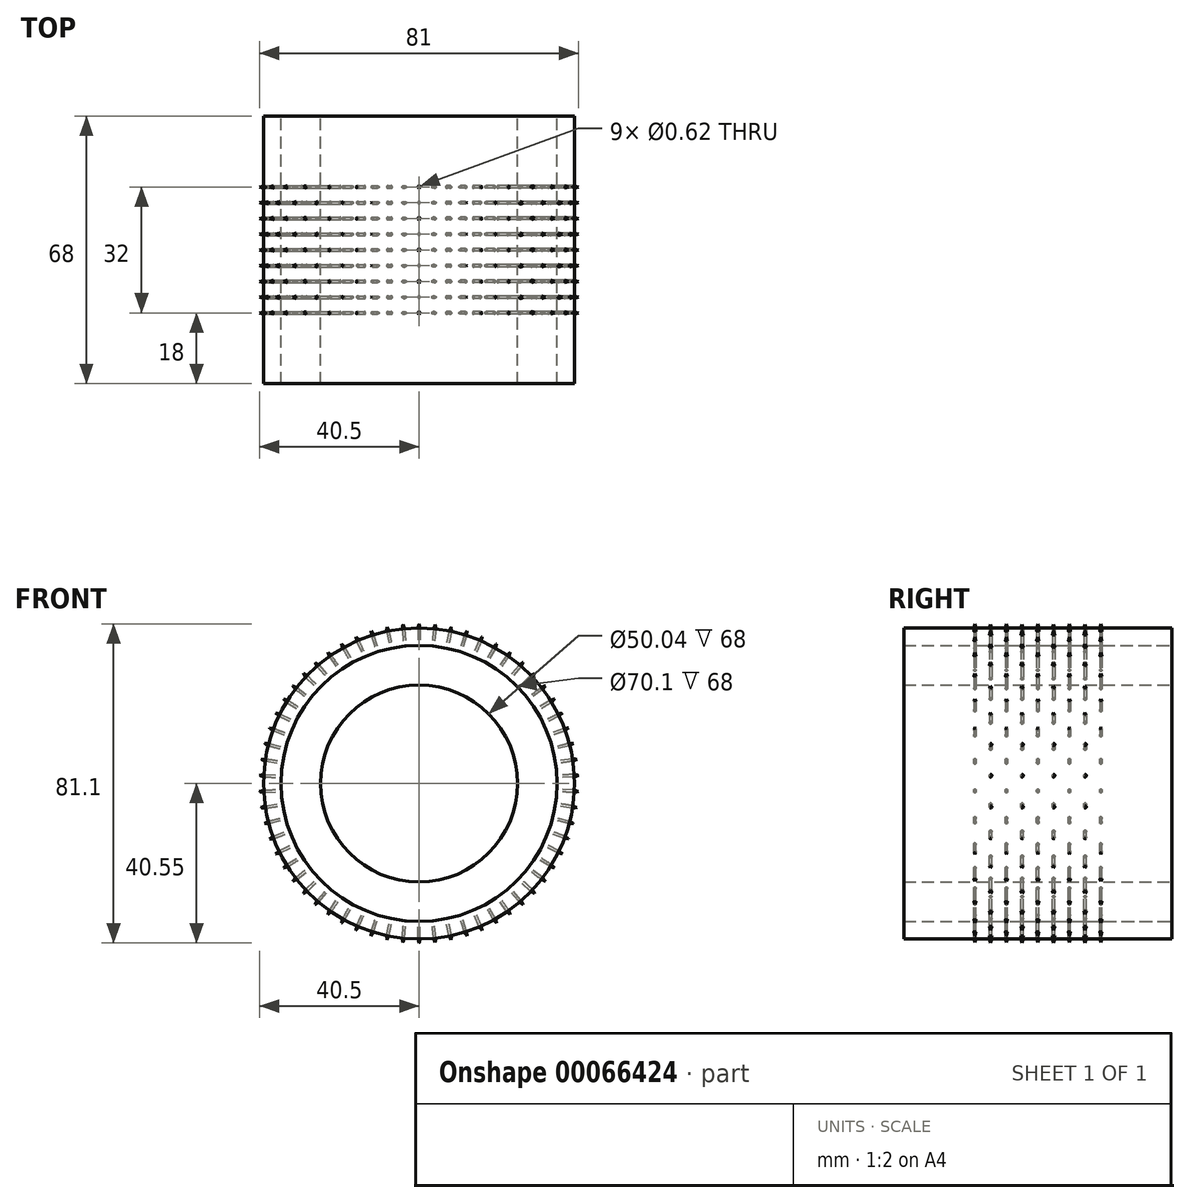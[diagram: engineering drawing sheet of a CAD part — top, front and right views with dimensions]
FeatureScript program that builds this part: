
annotation { "Feature Type Name" : "Feature", "Feature Type Description" : "" }
export const myFeature = defineFeature(function(context is Context, id is Id, definition is map)
    precondition{}
    {
        {
            var Q0;
            Q0=qCreatedBy(makeId("Front.planeOp"),FACE);
            var sketch = newSketch(context, id + "F0", { "sketchPlane" : qUnion([Q0])});
            skCircle(sketch, "E0", {"center": v(0, 0) * mm, "radius": 25.02 * mm});
            skCircle(sketch, "E1", {"center": v(0, 0) * mm, "radius": 35.05 * mm});
            skSolve(sketch);
        }
        {
            var Q0;
            Q0=makeQuery(id+"F0.imprint","IMPRINT",FACE,{"disambiguationData":[TD([[makeQuery(id+"F0.imprint","IMPRINT",EDGE,{"derivedFrom":sQuery(id+"F0.wireOp",EDGE,"E0")}),-1.0]])]});
            extrude(context, id + "F1", {"entities" : qUnion([Q0]), "endBound" : BoundingType.SYMMETRIC, "depth" : 68 * mm});
        }
        {
            var Q0;
            Q0=qCreatedBy(makeId("Front.planeOp"),FACE);
            var sketch = newSketch(context, id + "F2", { "sketchPlane" : qUnion([Q0])});
            skCircle(sketch, "E2.0", {"center": v(0, 0) * mm, "radius": 35.05 * mm});
            skCircle(sketch, "E3", {"center": v(0, 0) * mm, "radius": 39.5 * mm});
            skSolve(sketch);
        }
        {
            var Q0;
            Q0=makeQuery(id+"F2.imprint","IMPRINT",FACE,{"disambiguationData":[TD([[makeQuery(id+"F2.imprint","IMPRINT",EDGE,{"derivedFrom":sQuery(id+"F2.wireOp",EDGE,"E2.0")}),-1.0]])]});
            extrude(context, id + "F3", {"entities" : qUnion([Q0]), "endBound" : BoundingType.SYMMETRIC, "depth" : 68 * mm});
        }
        {
            var Q0;
            Q0=qCreatedBy(makeId("Top.planeOp"),FACE);
            cPlane(context, id + "F4", {"entities" : qUnion([Q0]), "cplaneType" : CPlaneType.OFFSET, "offset" : 70.1 / 2 * mm, "width" : 152.4 * mm, "height" : 152.4 * mm});
        }
        {
            var Q0;
            Q0=qCreatedBy(id+"F4.planeOp",FACE);
            var sketch = newSketch(context, id + "F5", { "sketchPlane" : qUnion([Q0])});
            skCircle(sketch, "E4", {"center": v(0, 0) * mm, "radius": 0.31 * mm});
            skCircle(sketch, "E5.0.1.0", {"center": v(0, 8) * mm, "radius": 0.31 * mm});
            skCircle(sketch, "E5.0.2.0", {"center": v(0, 16) * mm, "radius": 0.31 * mm});
            skCircle(sketch, "E5.0.3.0", {"center": v(0, 24) * mm, "radius": 0.31 * mm});
            skCircle(sketch, "E5.0.4.0", {"center": v(0, 32) * mm, "radius": 0.31 * mm});
            skLineSegment(sketch, "E5.direction1", {"start": v(0, 0) * mm, "end": v(25.4, 0) * mm, "construction": true});
            skLineSegment(sketch, "E5.direction2", {"start": v(0, 0) * mm, "end": v(0, 8) * mm, "construction": true});
            skCircle(sketch, "E6.0.1.0", {"center": v(0, -8) * mm, "radius": 0.31 * mm});
            skCircle(sketch, "E6.0.2.0", {"center": v(0, -16) * mm, "radius": 0.31 * mm});
            skCircle(sketch, "E6.0.3.0", {"center": v(0, -24) * mm, "radius": 0.31 * mm});
            skCircle(sketch, "E6.0.4.0", {"center": v(0, -32) * mm, "radius": 0.31 * mm});
            skLineSegment(sketch, "E6.direction2", {"start": v(0, 0) * mm, "end": v(0, -8) * mm, "construction": true});
            skSolve(sketch);
        }
        {
            var Q0;
            Q0=makeQuery(id+"F5.imprint","IMPRINT",FACE,{"disambiguationData":[TD([[makeQuery(id+"F5.imprint","IMPRINT",EDGE,{"derivedFrom":sQuery(id+"F5.wireOp",EDGE,"E6.0.2.0")}),1.0]])]});
            var Q1;
            Q1=makeQuery(id+"F5.imprint","IMPRINT",FACE,{"disambiguationData":[TD([[makeQuery(id+"F5.imprint","IMPRINT",EDGE,{"derivedFrom":sQuery(id+"F5.wireOp",EDGE,"E6.0.1.0")}),1.0]])]});
            var Q2;
            Q2=makeQuery(id+"F5.imprint","IMPRINT",FACE,{"disambiguationData":[TD([[makeQuery(id+"F5.imprint","IMPRINT",EDGE,{"derivedFrom":sQuery(id+"F5.wireOp",EDGE,"E4")}),1.0]])]});
            var Q3;
            Q3=makeQuery(id+"F5.imprint","IMPRINT",FACE,{"disambiguationData":[TD([[makeQuery(id+"F5.imprint","IMPRINT",EDGE,{"derivedFrom":sQuery(id+"F5.wireOp",EDGE,"E5.0.2.0")}),1.0]])]});
            var Q4;
            Q4=makeQuery(id+"F5.imprint","IMPRINT",FACE,{"disambiguationData":[TD([[makeQuery(id+"F5.imprint","IMPRINT",EDGE,{"derivedFrom":sQuery(id+"F5.wireOp",EDGE,"E5.0.1.0")}),1.0]])]});
            extrude(context, id + "F6", {"entities" : qUnion([Q0, Q1, Q2, Q3, Q4]), "operationType" : NewBodyOperationType.REMOVE, "depth" : 25.4 * mm});
        }
        {
            var Q0;
            Q0=qCreatedBy(makeId("Top.planeOp"),FACE);
            var sketch = newSketch(context, id + "F7", { "sketchPlane" : qUnion([Q0])});
            skLineSegment(sketch, "E7", {"start": v(0, 66.25) * mm, "end": v(0, -72.1) * mm, "construction": true});
            skSolve(sketch);
        }
        {
            var Q0;
            Q0=makeQuery(id+"F5.imprint","IMPRINT",FACE,{"disambiguationData":[TD([[makeQuery(id+"F5.imprint","IMPRINT",EDGE,{"derivedFrom":sQuery(id+"F5.wireOp",EDGE,"E5.0.2.0")}),1.0]])]});
            var Q1;
            Q1=makeQuery(id+"F5.imprint","IMPRINT",FACE,{"disambiguationData":[TD([[makeQuery(id+"F5.imprint","IMPRINT",EDGE,{"derivedFrom":sQuery(id+"F5.wireOp",EDGE,"E5.0.1.0")}),1.0]])]});
            var Q2;
            Q2=makeQuery(id+"F5.imprint","IMPRINT",FACE,{"disambiguationData":[TD([[makeQuery(id+"F5.imprint","IMPRINT",EDGE,{"derivedFrom":sQuery(id+"F5.wireOp",EDGE,"E6.0.1.0")}),1.0]])]});
            var Q3;
            Q3=makeQuery(id+"F5.imprint","IMPRINT",FACE,{"disambiguationData":[TD([[makeQuery(id+"F5.imprint","IMPRINT",EDGE,{"derivedFrom":sQuery(id+"F5.wireOp",EDGE,"E6.0.2.0")}),1.0]])]});
            var Q4;
            Q4=makeQuery(id+"F5.imprint","IMPRINT",FACE,{"disambiguationData":[TD([[makeQuery(id+"F5.imprint","IMPRINT",EDGE,{"derivedFrom":sQuery(id+"F5.wireOp",EDGE,"E4")}),1.0]])]});
            extrude(context, id + "F8", {"entities" : qUnion([Q0, Q1, Q2, Q3, Q4]), "depth" : 5.5 * mm});
        }
        {
            var Q0;
            Q0=makeQuery(id+"F8.opExtrude","CAP_EDGE",EDGE,{"disambiguationData":[OSD([sQuery(id+"F5.wireOp",EDGE,"E6.0.4.0")])],"isStart":false});
            var Q1;
            Q1=makeQuery(id+"F8.opExtrude","CAP_EDGE",EDGE,{"disambiguationData":[OSD([sQuery(id+"F5.wireOp",EDGE,"E6.0.3.0")])],"isStart":false});
            var Q2;
            Q2=makeQuery(id+"F8.opExtrude","CAP_EDGE",EDGE,{"disambiguationData":[OSD([sQuery(id+"F5.wireOp",EDGE,"E6.0.2.0")])],"isStart":false});
            var Q3;
            Q3=makeQuery(id+"F8.opExtrude","CAP_EDGE",EDGE,{"disambiguationData":[OSD([sQuery(id+"F5.wireOp",EDGE,"E6.0.1.0")])],"isStart":false});
            var Q4;
            Q4=makeQuery(id+"F8.opExtrude","CAP_EDGE",EDGE,{"disambiguationData":[OSD([sQuery(id+"F5.wireOp",EDGE,"E4")])],"isStart":false});
            var Q5;
            Q5=makeQuery(id+"F8.opExtrude","CAP_EDGE",EDGE,{"disambiguationData":[OSD([sQuery(id+"F5.wireOp",EDGE,"E5.0.1.0")])],"isStart":false});
            var Q6;
            Q6=makeQuery(id+"F8.opExtrude","CAP_EDGE",EDGE,{"disambiguationData":[OSD([sQuery(id+"F5.wireOp",EDGE,"E5.0.2.0")])],"isStart":false});
            var Q7;
            Q7=makeQuery(id+"F8.opExtrude","CAP_EDGE",EDGE,{"disambiguationData":[OSD([sQuery(id+"F5.wireOp",EDGE,"E5.0.3.0")])],"isStart":false});
            var Q8;
            Q8=makeQuery(id+"F8.opExtrude","CAP_EDGE",EDGE,{"disambiguationData":[OSD([sQuery(id+"F5.wireOp",EDGE,"E5.0.4.0")])],"isStart":false});
            chamfer(context, id + "F9", {"entities" : qUnion([Q0, Q1, Q2, Q3, Q4, Q5, Q6, Q7, Q8]), "chamferType" : ChamferType.TWO_OFFSETS, "width1" : 0.31 * mm, "oppositeDirection" : false, "width2" : 1.1 * mm});
        }
        {
            var Q0;
            Q0=qCreatedBy(makeId("Top.planeOp"),FACE);
            cPlane(context, id + "F10", {"entities" : qUnion([Q0]), "cplaneType" : CPlaneType.OFFSET, "offset" : 70.1 * mm / 2, "oppositeDirection" : true, "width" : 152.4 * mm, "height" : 152.4 * mm});
        }
        {
            var Q0;
            Q0=qCreatedBy(id+"F10.planeOp",FACE);
            var sketch = newSketch(context, id + "F11", { "sketchPlane" : qUnion([Q0])});
            skCircle(sketch, "E8", {"center": v(0, -4) * mm, "radius": 0.31 * mm});
            skCircle(sketch, "E9", {"center": v(0, 4) * mm, "radius": 0.31 * mm});
            skCircle(sketch, "E10.0.1.0", {"center": v(0, -12) * mm, "radius": 0.31 * mm});
            skCircle(sketch, "E10.0.2.0", {"center": v(0, -20) * mm, "radius": 0.31 * mm});
            skCircle(sketch, "E10.0.3.0", {"center": v(0, -28) * mm, "radius": 0.31 * mm});
            skLineSegment(sketch, "E10.direction1", {"start": v(0, -4) * mm, "end": v(20.95, -4) * mm, "construction": true});
            skLineSegment(sketch, "E10.direction2", {"start": v(0, -4) * mm, "end": v(0, -12) * mm, "construction": true});
            skCircle(sketch, "E11.0.1.0", {"center": v(0, 12) * mm, "radius": 0.31 * mm});
            skCircle(sketch, "E11.0.2.0", {"center": v(0, 20) * mm, "radius": 0.31 * mm});
            skCircle(sketch, "E11.0.3.0", {"center": v(0, 28) * mm, "radius": 0.31 * mm});
            skLineSegment(sketch, "E11.direction1", {"start": v(0, 4) * mm, "end": v(25.4, 4) * mm, "construction": true});
            skLineSegment(sketch, "E11.direction2", {"start": v(0, 4) * mm, "end": v(0, 12) * mm, "construction": true});
            skSolve(sketch);
        }
        {
            var Q0;
            Q0=makeQuery(id+"F11.imprint","IMPRINT",FACE,{"disambiguationData":[TD([[makeQuery(id+"F11.imprint","IMPRINT",EDGE,{"derivedFrom":sQuery(id+"F11.wireOp",EDGE,"E8")}),1.0]])]});
            var Q1;
            Q1=makeQuery(id+"F11.imprint","IMPRINT",FACE,{"disambiguationData":[TD([[makeQuery(id+"F11.imprint","IMPRINT",EDGE,{"derivedFrom":sQuery(id+"F11.wireOp",EDGE,"E10.0.1.0")}),1.0]])]});
            var Q2;
            Q2=makeQuery(id+"F11.imprint","IMPRINT",FACE,{"disambiguationData":[TD([[makeQuery(id+"F11.imprint","IMPRINT",EDGE,{"derivedFrom":sQuery(id+"F11.wireOp",EDGE,"E11.0.1.0")}),1.0]])]});
            var Q3;
            Q3=makeQuery(id+"F11.imprint","IMPRINT",FACE,{"disambiguationData":[TD([[makeQuery(id+"F11.imprint","IMPRINT",EDGE,{"derivedFrom":sQuery(id+"F11.wireOp",EDGE,"E9")}),1.0]])]});
            extrude(context, id + "F12", {"entities" : qUnion([Q0, Q1, Q2, Q3]), "operationType" : NewBodyOperationType.REMOVE, "oppositeDirection" : true, "depth" : 25.4 * mm});
        }
        {
            var Q0;
            Q0=makeQuery(id+"F11.imprint","IMPRINT",FACE,{"disambiguationData":[TD([[makeQuery(id+"F11.imprint","IMPRINT",EDGE,{"derivedFrom":sQuery(id+"F11.wireOp",EDGE,"E10.0.1.0")}),1.0]])]});
            var Q1;
            Q1=makeQuery(id+"F11.imprint","IMPRINT",FACE,{"disambiguationData":[TD([[makeQuery(id+"F11.imprint","IMPRINT",EDGE,{"derivedFrom":sQuery(id+"F11.wireOp",EDGE,"E8")}),1.0]])]});
            var Q2;
            Q2=makeQuery(id+"F11.imprint","IMPRINT",FACE,{"disambiguationData":[TD([[makeQuery(id+"F11.imprint","IMPRINT",EDGE,{"derivedFrom":sQuery(id+"F11.wireOp",EDGE,"E9")}),1.0]])]});
            var Q3;
            Q3=makeQuery(id+"F11.imprint","IMPRINT",FACE,{"disambiguationData":[TD([[makeQuery(id+"F11.imprint","IMPRINT",EDGE,{"derivedFrom":sQuery(id+"F11.wireOp",EDGE,"E11.0.1.0")}),1.0]])]});
            extrude(context, id + "F13", {"entities" : qUnion([Q0, Q1, Q2, Q3]), "oppositeDirection" : true, "depth" : 5.5 * mm});
        }
        {
            var Q0;
            Q0=makeQuery(id+"F13.opExtrude","CAP_EDGE",EDGE,{"disambiguationData":[OSD([sQuery(id+"F11.wireOp",EDGE,"E10.0.3.0")])],"isStart":false});
            var Q1;
            Q1=makeQuery(id+"F13.opExtrude","CAP_EDGE",EDGE,{"disambiguationData":[OSD([sQuery(id+"F11.wireOp",EDGE,"E10.0.2.0")])],"isStart":false});
            var Q2;
            Q2=makeQuery(id+"F13.opExtrude","CAP_EDGE",EDGE,{"disambiguationData":[OSD([sQuery(id+"F11.wireOp",EDGE,"E10.0.1.0")])],"isStart":false});
            var Q3;
            Q3=makeQuery(id+"F13.opExtrude","CAP_EDGE",EDGE,{"disambiguationData":[OSD([sQuery(id+"F11.wireOp",EDGE,"E8")])],"isStart":false});
            var Q4;
            Q4=makeQuery(id+"F13.opExtrude","CAP_EDGE",EDGE,{"disambiguationData":[OSD([sQuery(id+"F11.wireOp",EDGE,"E9")])],"isStart":false});
            var Q5;
            Q5=makeQuery(id+"F13.opExtrude","CAP_EDGE",EDGE,{"disambiguationData":[OSD([sQuery(id+"F11.wireOp",EDGE,"E11.0.1.0")])],"isStart":false});
            var Q6;
            Q6=makeQuery(id+"F13.opExtrude","CAP_EDGE",EDGE,{"disambiguationData":[OSD([sQuery(id+"F11.wireOp",EDGE,"E11.0.2.0")])],"isStart":false});
            var Q7;
            Q7=makeQuery(id+"F13.opExtrude","CAP_EDGE",EDGE,{"disambiguationData":[OSD([sQuery(id+"F11.wireOp",EDGE,"E11.0.3.0")])],"isStart":false});
            chamfer(context, id + "F14", {"entities" : qUnion([Q0, Q1, Q2, Q3, Q4, Q5, Q6, Q7]), "chamferType" : ChamferType.TWO_OFFSETS, "width1" : 1.1 * mm, "oppositeDirection" : false, "width2" : 0.31 * mm, "tangentPropagation" : true});
        }
        {
            var Q0;
            Q0=makeQuery(id+"F8.opExtrude","SWEPT_BODY",BODY,{"disambiguationData":[OSD([sQuery(id+"F5.wireOp",EDGE,"E4")])]});
            var Q1;
            Q1=makeQuery(id+"F8.opExtrude","SWEPT_BODY",BODY,{"disambiguationData":[OSD([sQuery(id+"F5.wireOp",EDGE,"E5.0.1.0")])]});
            var Q2;
            Q2=makeQuery(id+"F8.opExtrude","SWEPT_BODY",BODY,{"disambiguationData":[OSD([sQuery(id+"F5.wireOp",EDGE,"E5.0.2.0")])]});
            var Q3;
            Q3=makeQuery(id+"F8.opExtrude","SWEPT_BODY",BODY,{"disambiguationData":[OSD([sQuery(id+"F5.wireOp",EDGE,"E5.0.3.0")])]});
            var Q4;
            Q4=makeQuery(id+"F8.opExtrude","SWEPT_BODY",BODY,{"disambiguationData":[OSD([sQuery(id+"F5.wireOp",EDGE,"E5.0.4.0")])]});
            var Q5;
            Q5=makeQuery(id+"F8.opExtrude","SWEPT_BODY",BODY,{"disambiguationData":[OSD([sQuery(id+"F5.wireOp",EDGE,"E6.0.1.0")])]});
            var Q6;
            Q6=makeQuery(id+"F8.opExtrude","SWEPT_BODY",BODY,{"disambiguationData":[OSD([sQuery(id+"F5.wireOp",EDGE,"E6.0.2.0")])]});
            var Q7;
            Q7=makeQuery(id+"F8.opExtrude","SWEPT_BODY",BODY,{"disambiguationData":[OSD([sQuery(id+"F5.wireOp",EDGE,"E6.0.3.0")])]});
            var Q8;
            Q8=makeQuery(id+"F8.opExtrude","SWEPT_BODY",BODY,{"disambiguationData":[OSD([sQuery(id+"F5.wireOp",EDGE,"E6.0.4.0")])]});
            var Q9;
            Q9=makeQuery(id+"F13.opExtrude","SWEPT_BODY",BODY,{"disambiguationData":[OSD([sQuery(id+"F11.wireOp",EDGE,"E8")])]});
            var Q10;
            Q10=makeQuery(id+"F13.opExtrude","SWEPT_BODY",BODY,{"disambiguationData":[OSD([sQuery(id+"F11.wireOp",EDGE,"E9")])]});
            var Q11;
            Q11=makeQuery(id+"F13.opExtrude","SWEPT_BODY",BODY,{"disambiguationData":[OSD([sQuery(id+"F11.wireOp",EDGE,"E10.0.1.0")])]});
            var Q12;
            Q12=makeQuery(id+"F13.opExtrude","SWEPT_BODY",BODY,{"disambiguationData":[OSD([sQuery(id+"F11.wireOp",EDGE,"E10.0.2.0")])]});
            var Q13;
            Q13=makeQuery(id+"F13.opExtrude","SWEPT_BODY",BODY,{"disambiguationData":[OSD([sQuery(id+"F11.wireOp",EDGE,"E10.0.3.0")])]});
            var Q14;
            Q14=makeQuery(id+"F13.opExtrude","SWEPT_BODY",BODY,{"disambiguationData":[OSD([sQuery(id+"F11.wireOp",EDGE,"E11.0.1.0")])]});
            var Q15;
            Q15=makeQuery(id+"F13.opExtrude","SWEPT_BODY",BODY,{"disambiguationData":[OSD([sQuery(id+"F11.wireOp",EDGE,"E11.0.2.0")])]});
            var Q16;
            Q16=makeQuery(id+"F13.opExtrude","SWEPT_BODY",BODY,{"disambiguationData":[OSD([sQuery(id+"F11.wireOp",EDGE,"E11.0.3.0")])]});
            var Q17;
            Q17=sQuery(id+"F7.wireOp",EDGE,"E7");
            circularPattern(context, id + "F15", {"entities" : qUnion([Q0, Q1, Q2, Q3, Q4, Q5, Q6, Q7, Q8, Q9, Q10, Q11, Q12, Q13, Q14, Q15, Q16]), "axis" : qUnion([Q17]), "angle" : 11.6 * degree, "instanceCount" : round(31)});
        }
        {
            var Q0;
            Q0=makeQuery(id+"F15.opPattern","COPY",BODY,{"derivedFrom":makeQuery(id+"F13.opExtrude","SWEPT_BODY",BODY,{"disambiguationData":[OSD([sQuery(id+"F11.wireOp",EDGE,"E11.0.3.0")])]}),"instanceName":"2"});
            var Q1;
            Q1=makeQuery(id+"F15.opPattern","COPY",BODY,{"derivedFrom":makeQuery(id+"F8.opExtrude","SWEPT_BODY",BODY,{"disambiguationData":[OSD([sQuery(id+"F5.wireOp",EDGE,"E4")])]}),"instanceName":"3"});
            var Q2;
            Q2=makeQuery(id+"F15.opPattern","COPY",BODY,{"derivedFrom":makeQuery(id+"F8.opExtrude","SWEPT_BODY",BODY,{"disambiguationData":[OSD([sQuery(id+"F5.wireOp",EDGE,"E5.0.2.0")])]}),"instanceName":"3"});
            var Q3;
            Q3=makeQuery(id+"F15.opPattern","COPY",BODY,{"derivedFrom":makeQuery(id+"F8.opExtrude","SWEPT_BODY",BODY,{"disambiguationData":[OSD([sQuery(id+"F5.wireOp",EDGE,"E5.0.4.0")])]}),"instanceName":"3"});
            var Q4;
            Q4=makeQuery(id+"F15.opPattern","COPY",BODY,{"derivedFrom":makeQuery(id+"F13.opExtrude","SWEPT_BODY",BODY,{"disambiguationData":[OSD([sQuery(id+"F11.wireOp",EDGE,"E11.0.2.0")])]}),"instanceName":"3"});
            var Q5;
            Q5=makeQuery(id+"F15.opPattern","COPY",BODY,{"derivedFrom":makeQuery(id+"F8.opExtrude","SWEPT_BODY",BODY,{"disambiguationData":[OSD([sQuery(id+"F5.wireOp",EDGE,"E4")])]}),"instanceName":"4"});
            var Q6;
            Q6=makeQuery(id+"F15.opPattern","COPY",BODY,{"derivedFrom":makeQuery(id+"F8.opExtrude","SWEPT_BODY",BODY,{"disambiguationData":[OSD([sQuery(id+"F5.wireOp",EDGE,"E5.0.1.0")])]}),"instanceName":"4"});
            var Q7;
            Q7=makeQuery(id+"F15.opPattern","COPY",BODY,{"derivedFrom":makeQuery(id+"F8.opExtrude","SWEPT_BODY",BODY,{"disambiguationData":[OSD([sQuery(id+"F5.wireOp",EDGE,"E5.0.2.0")])]}),"instanceName":"4"});
            var Q8;
            Q8=makeQuery(id+"F15.opPattern","COPY",BODY,{"derivedFrom":makeQuery(id+"F8.opExtrude","SWEPT_BODY",BODY,{"disambiguationData":[OSD([sQuery(id+"F5.wireOp",EDGE,"E6.0.1.0")])]}),"instanceName":"4"});
            var Q9;
            Q9=makeQuery(id+"F15.opPattern","COPY",BODY,{"derivedFrom":makeQuery(id+"F13.opExtrude","SWEPT_BODY",BODY,{"disambiguationData":[OSD([sQuery(id+"F11.wireOp",EDGE,"E9")])]}),"instanceName":"1"});
            var Q10;
            Q10=makeQuery(id+"F15.opPattern","COPY",BODY,{"derivedFrom":makeQuery(id+"F13.opExtrude","SWEPT_BODY",BODY,{"disambiguationData":[OSD([sQuery(id+"F11.wireOp",EDGE,"E10.0.1.0")])]}),"instanceName":"1"});
            var Q11;
            Q11=makeQuery(id+"F15.opPattern","COPY",BODY,{"derivedFrom":makeQuery(id+"F13.opExtrude","SWEPT_BODY",BODY,{"disambiguationData":[OSD([sQuery(id+"F11.wireOp",EDGE,"E10.0.2.0")])]}),"instanceName":"1"});
            var Q12;
            Q12=makeQuery(id+"F15.opPattern","COPY",BODY,{"derivedFrom":makeQuery(id+"F13.opExtrude","SWEPT_BODY",BODY,{"disambiguationData":[OSD([sQuery(id+"F11.wireOp",EDGE,"E10.0.3.0")])]}),"instanceName":"1"});
            var Q13;
            Q13=makeQuery(id+"F15.opPattern","COPY",BODY,{"derivedFrom":makeQuery(id+"F13.opExtrude","SWEPT_BODY",BODY,{"disambiguationData":[OSD([sQuery(id+"F11.wireOp",EDGE,"E11.0.1.0")])]}),"instanceName":"1"});
            var Q14;
            Q14=makeQuery(id+"F15.opPattern","COPY",BODY,{"derivedFrom":makeQuery(id+"F13.opExtrude","SWEPT_BODY",BODY,{"disambiguationData":[OSD([sQuery(id+"F11.wireOp",EDGE,"E11.0.2.0")])]}),"instanceName":"1"});
            var Q15;
            Q15=makeQuery(id+"F15.opPattern","COPY",BODY,{"derivedFrom":makeQuery(id+"F13.opExtrude","SWEPT_BODY",BODY,{"disambiguationData":[OSD([sQuery(id+"F11.wireOp",EDGE,"E11.0.3.0")])]}),"instanceName":"1"});
            var Q16;
            Q16=makeQuery(id+"F15.opPattern","COPY",BODY,{"derivedFrom":makeQuery(id+"F8.opExtrude","SWEPT_BODY",BODY,{"disambiguationData":[OSD([sQuery(id+"F5.wireOp",EDGE,"E4")])]}),"instanceName":"2"});
            var Q17;
            Q17=makeQuery(id+"F15.opPattern","COPY",BODY,{"derivedFrom":makeQuery(id+"F8.opExtrude","SWEPT_BODY",BODY,{"disambiguationData":[OSD([sQuery(id+"F5.wireOp",EDGE,"E5.0.1.0")])]}),"instanceName":"2"});
            var Q18;
            Q18=makeQuery(id+"F15.opPattern","COPY",BODY,{"derivedFrom":makeQuery(id+"F8.opExtrude","SWEPT_BODY",BODY,{"disambiguationData":[OSD([sQuery(id+"F5.wireOp",EDGE,"E5.0.2.0")])]}),"instanceName":"2"});
            var Q19;
            Q19=makeQuery(id+"F15.opPattern","COPY",BODY,{"derivedFrom":makeQuery(id+"F8.opExtrude","SWEPT_BODY",BODY,{"disambiguationData":[OSD([sQuery(id+"F5.wireOp",EDGE,"E5.0.3.0")])]}),"instanceName":"2"});
            var Q20;
            Q20=makeQuery(id+"F15.opPattern","COPY",BODY,{"derivedFrom":makeQuery(id+"F8.opExtrude","SWEPT_BODY",BODY,{"disambiguationData":[OSD([sQuery(id+"F5.wireOp",EDGE,"E5.0.3.0")])]}),"instanceName":"2"});
            var Q21;
            Q21=makeQuery(id+"F15.opPattern","COPY",BODY,{"derivedFrom":makeQuery(id+"F8.opExtrude","SWEPT_BODY",BODY,{"disambiguationData":[OSD([sQuery(id+"F5.wireOp",EDGE,"E5.0.4.0")])]}),"instanceName":"2"});
            var Q22;
            Q22=makeQuery(id+"F15.opPattern","COPY",BODY,{"derivedFrom":makeQuery(id+"F8.opExtrude","SWEPT_BODY",BODY,{"disambiguationData":[OSD([sQuery(id+"F5.wireOp",EDGE,"E6.0.1.0")])]}),"instanceName":"2"});
            var Q23;
            Q23=makeQuery(id+"F15.opPattern","COPY",BODY,{"derivedFrom":makeQuery(id+"F8.opExtrude","SWEPT_BODY",BODY,{"disambiguationData":[OSD([sQuery(id+"F5.wireOp",EDGE,"E6.0.2.0")])]}),"instanceName":"2"});
            var Q24;
            Q24=makeQuery(id+"F15.opPattern","COPY",BODY,{"derivedFrom":makeQuery(id+"F8.opExtrude","SWEPT_BODY",BODY,{"disambiguationData":[OSD([sQuery(id+"F5.wireOp",EDGE,"E6.0.3.0")])]}),"instanceName":"2"});
            var Q25;
            Q25=makeQuery(id+"F15.opPattern","COPY",BODY,{"derivedFrom":makeQuery(id+"F8.opExtrude","SWEPT_BODY",BODY,{"disambiguationData":[OSD([sQuery(id+"F5.wireOp",EDGE,"E6.0.4.0")])]}),"instanceName":"2"});
            var Q26;
            Q26=makeQuery(id+"F15.opPattern","COPY",BODY,{"derivedFrom":makeQuery(id+"F13.opExtrude","SWEPT_BODY",BODY,{"disambiguationData":[OSD([sQuery(id+"F11.wireOp",EDGE,"E8")])]}),"instanceName":"2"});
            var Q27;
            Q27=makeQuery(id+"F15.opPattern","COPY",BODY,{"derivedFrom":makeQuery(id+"F13.opExtrude","SWEPT_BODY",BODY,{"disambiguationData":[OSD([sQuery(id+"F11.wireOp",EDGE,"E9")])]}),"instanceName":"2"});
            var Q28;
            Q28=makeQuery(id+"F15.opPattern","COPY",BODY,{"derivedFrom":makeQuery(id+"F13.opExtrude","SWEPT_BODY",BODY,{"disambiguationData":[OSD([sQuery(id+"F11.wireOp",EDGE,"E10.0.1.0")])]}),"instanceName":"2"});
            var Q29;
            Q29=makeQuery(id+"F15.opPattern","COPY",BODY,{"derivedFrom":makeQuery(id+"F13.opExtrude","SWEPT_BODY",BODY,{"disambiguationData":[OSD([sQuery(id+"F11.wireOp",EDGE,"E10.0.2.0")])]}),"instanceName":"2"});
            var Q30;
            Q30=makeQuery(id+"F15.opPattern","COPY",BODY,{"derivedFrom":makeQuery(id+"F13.opExtrude","SWEPT_BODY",BODY,{"disambiguationData":[OSD([sQuery(id+"F11.wireOp",EDGE,"E10.0.3.0")])]}),"instanceName":"2"});
            var Q31;
            Q31=makeQuery(id+"F15.opPattern","COPY",BODY,{"derivedFrom":makeQuery(id+"F13.opExtrude","SWEPT_BODY",BODY,{"disambiguationData":[OSD([sQuery(id+"F11.wireOp",EDGE,"E11.0.1.0")])]}),"instanceName":"2"});
            var Q32;
            Q32=makeQuery(id+"F15.opPattern","COPY",BODY,{"derivedFrom":makeQuery(id+"F13.opExtrude","SWEPT_BODY",BODY,{"disambiguationData":[OSD([sQuery(id+"F11.wireOp",EDGE,"E11.0.2.0")])]}),"instanceName":"2"});
            var Q33;
            Q33=makeQuery(id+"F15.opPattern","COPY",BODY,{"derivedFrom":makeQuery(id+"F8.opExtrude","SWEPT_BODY",BODY,{"disambiguationData":[OSD([sQuery(id+"F5.wireOp",EDGE,"E5.0.1.0")])]}),"instanceName":"3"});
            var Q34;
            Q34=makeQuery(id+"F15.opPattern","COPY",BODY,{"derivedFrom":makeQuery(id+"F8.opExtrude","SWEPT_BODY",BODY,{"disambiguationData":[OSD([sQuery(id+"F5.wireOp",EDGE,"E5.0.3.0")])]}),"instanceName":"3"});
            var Q35;
            Q35=makeQuery(id+"F15.opPattern","COPY",BODY,{"derivedFrom":makeQuery(id+"F8.opExtrude","SWEPT_BODY",BODY,{"disambiguationData":[OSD([sQuery(id+"F5.wireOp",EDGE,"E6.0.1.0")])]}),"instanceName":"3"});
            var Q36;
            Q36=makeQuery(id+"F15.opPattern","COPY",BODY,{"derivedFrom":makeQuery(id+"F8.opExtrude","SWEPT_BODY",BODY,{"disambiguationData":[OSD([sQuery(id+"F5.wireOp",EDGE,"E6.0.2.0")])]}),"instanceName":"3"});
            var Q37;
            Q37=makeQuery(id+"F15.opPattern","COPY",BODY,{"derivedFrom":makeQuery(id+"F8.opExtrude","SWEPT_BODY",BODY,{"disambiguationData":[OSD([sQuery(id+"F5.wireOp",EDGE,"E6.0.3.0")])]}),"instanceName":"3"});
            var Q38;
            Q38=makeQuery(id+"F15.opPattern","COPY",BODY,{"derivedFrom":makeQuery(id+"F8.opExtrude","SWEPT_BODY",BODY,{"disambiguationData":[OSD([sQuery(id+"F5.wireOp",EDGE,"E6.0.4.0")])]}),"instanceName":"3"});
            var Q39;
            Q39=makeQuery(id+"F15.opPattern","COPY",BODY,{"derivedFrom":makeQuery(id+"F13.opExtrude","SWEPT_BODY",BODY,{"disambiguationData":[OSD([sQuery(id+"F11.wireOp",EDGE,"E8")])]}),"instanceName":"3"});
            var Q40;
            Q40=makeQuery(id+"F15.opPattern","COPY",BODY,{"derivedFrom":makeQuery(id+"F13.opExtrude","SWEPT_BODY",BODY,{"disambiguationData":[OSD([sQuery(id+"F11.wireOp",EDGE,"E9")])]}),"instanceName":"3"});
            var Q41;
            Q41=makeQuery(id+"F15.opPattern","COPY",BODY,{"derivedFrom":makeQuery(id+"F13.opExtrude","SWEPT_BODY",BODY,{"disambiguationData":[OSD([sQuery(id+"F11.wireOp",EDGE,"E10.0.1.0")])]}),"instanceName":"3"});
            var Q42;
            Q42=makeQuery(id+"F15.opPattern","COPY",BODY,{"derivedFrom":makeQuery(id+"F13.opExtrude","SWEPT_BODY",BODY,{"disambiguationData":[OSD([sQuery(id+"F11.wireOp",EDGE,"E10.0.2.0")])]}),"instanceName":"3"});
            var Q43;
            Q43=makeQuery(id+"F15.opPattern","COPY",BODY,{"derivedFrom":makeQuery(id+"F13.opExtrude","SWEPT_BODY",BODY,{"disambiguationData":[OSD([sQuery(id+"F11.wireOp",EDGE,"E10.0.3.0")])]}),"instanceName":"3"});
            var Q44;
            Q44=makeQuery(id+"F15.opPattern","COPY",BODY,{"derivedFrom":makeQuery(id+"F8.opExtrude","SWEPT_BODY",BODY,{"disambiguationData":[OSD([sQuery(id+"F5.wireOp",EDGE,"E5.0.3.0")])]}),"instanceName":"4"});
            var Q45;
            Q45=makeQuery(id+"F15.opPattern","COPY",BODY,{"derivedFrom":makeQuery(id+"F8.opExtrude","SWEPT_BODY",BODY,{"disambiguationData":[OSD([sQuery(id+"F5.wireOp",EDGE,"E5.0.4.0")])]}),"instanceName":"4"});
            var Q46;
            Q46=makeQuery(id+"F15.opPattern","COPY",BODY,{"derivedFrom":makeQuery(id+"F8.opExtrude","SWEPT_BODY",BODY,{"disambiguationData":[OSD([sQuery(id+"F5.wireOp",EDGE,"E6.0.2.0")])]}),"instanceName":"4"});
            var Q47;
            Q47=makeQuery(id+"F15.opPattern","COPY",BODY,{"derivedFrom":makeQuery(id+"F8.opExtrude","SWEPT_BODY",BODY,{"disambiguationData":[OSD([sQuery(id+"F5.wireOp",EDGE,"E6.0.3.0")])]}),"instanceName":"4"});
            var Q48;
            Q48=makeQuery(id+"F15.opPattern","COPY",BODY,{"derivedFrom":makeQuery(id+"F8.opExtrude","SWEPT_BODY",BODY,{"disambiguationData":[OSD([sQuery(id+"F5.wireOp",EDGE,"E6.0.4.0")])]}),"instanceName":"4"});
            var Q49;
            Q49=makeQuery(id+"F15.opPattern","COPY",BODY,{"derivedFrom":makeQuery(id+"F13.opExtrude","SWEPT_BODY",BODY,{"disambiguationData":[OSD([sQuery(id+"F11.wireOp",EDGE,"E8")])]}),"instanceName":"4"});
            var Q50;
            Q50=makeQuery(id+"F15.opPattern","COPY",BODY,{"derivedFrom":makeQuery(id+"F13.opExtrude","SWEPT_BODY",BODY,{"disambiguationData":[OSD([sQuery(id+"F11.wireOp",EDGE,"E9")])]}),"instanceName":"4"});
            var Q51;
            Q51=makeQuery(id+"F15.opPattern","COPY",BODY,{"derivedFrom":makeQuery(id+"F13.opExtrude","SWEPT_BODY",BODY,{"disambiguationData":[OSD([sQuery(id+"F11.wireOp",EDGE,"E10.0.1.0")])]}),"instanceName":"4"});
            var Q52;
            Q52=makeQuery(id+"F15.opPattern","COPY",BODY,{"derivedFrom":makeQuery(id+"F13.opExtrude","SWEPT_BODY",BODY,{"disambiguationData":[OSD([sQuery(id+"F11.wireOp",EDGE,"E10.0.2.0")])]}),"instanceName":"4"});
            var Q53;
            Q53=makeQuery(id+"F15.opPattern","COPY",BODY,{"derivedFrom":makeQuery(id+"F13.opExtrude","SWEPT_BODY",BODY,{"disambiguationData":[OSD([sQuery(id+"F11.wireOp",EDGE,"E10.0.3.0")])]}),"instanceName":"4"});
            var Q54;
            Q54=makeQuery(id+"F15.opPattern","COPY",BODY,{"derivedFrom":makeQuery(id+"F13.opExtrude","SWEPT_BODY",BODY,{"disambiguationData":[OSD([sQuery(id+"F11.wireOp",EDGE,"E11.0.1.0")])]}),"instanceName":"4"});
            var Q55;
            Q55=makeQuery(id+"F15.opPattern","COPY",BODY,{"derivedFrom":makeQuery(id+"F13.opExtrude","SWEPT_BODY",BODY,{"disambiguationData":[OSD([sQuery(id+"F11.wireOp",EDGE,"E11.0.3.0")])]}),"instanceName":"4"});
            var Q56;
            Q56=makeQuery(id+"F15.opPattern","COPY",BODY,{"derivedFrom":makeQuery(id+"F13.opExtrude","SWEPT_BODY",BODY,{"disambiguationData":[OSD([sQuery(id+"F11.wireOp",EDGE,"E11.0.2.0")])]}),"instanceName":"4"});
            var Q57;
            Q57=makeQuery(id+"F15.opPattern","COPY",BODY,{"derivedFrom":makeQuery(id+"F8.opExtrude","SWEPT_BODY",BODY,{"disambiguationData":[OSD([sQuery(id+"F5.wireOp",EDGE,"E5.0.4.0")])]}),"instanceName":"5"});
            var Q58;
            Q58=makeQuery(id+"F15.opPattern","COPY",BODY,{"derivedFrom":makeQuery(id+"F8.opExtrude","SWEPT_BODY",BODY,{"disambiguationData":[OSD([sQuery(id+"F5.wireOp",EDGE,"E5.0.1.0")])]}),"instanceName":"5"});
            var Q59;
            Q59=makeQuery(id+"F15.opPattern","COPY",BODY,{"derivedFrom":makeQuery(id+"F13.opExtrude","SWEPT_BODY",BODY,{"disambiguationData":[OSD([sQuery(id+"F11.wireOp",EDGE,"E11.0.1.0")])]}),"instanceName":"5"});
            var Q60;
            Q60=makeQuery(id+"F15.opPattern","COPY",BODY,{"derivedFrom":makeQuery(id+"F8.opExtrude","SWEPT_BODY",BODY,{"disambiguationData":[OSD([sQuery(id+"F5.wireOp",EDGE,"E5.0.4.0")])]}),"instanceName":"6"});
            var Q61;
            Q61=makeQuery(id+"F15.opPattern","COPY",BODY,{"derivedFrom":makeQuery(id+"F8.opExtrude","SWEPT_BODY",BODY,{"disambiguationData":[OSD([sQuery(id+"F5.wireOp",EDGE,"E6.0.4.0")])]}),"instanceName":"6"});
            var Q62;
            Q62=makeQuery(id+"F15.opPattern","COPY",BODY,{"derivedFrom":makeQuery(id+"F8.opExtrude","SWEPT_BODY",BODY,{"disambiguationData":[OSD([sQuery(id+"F5.wireOp",EDGE,"E5.0.4.0")])]}),"instanceName":"17"});
            var Q63;
            Q63=makeQuery(id+"F15.opPattern","COPY",BODY,{"derivedFrom":makeQuery(id+"F8.opExtrude","SWEPT_BODY",BODY,{"disambiguationData":[OSD([sQuery(id+"F5.wireOp",EDGE,"E5.0.3.0")])]}),"instanceName":"17"});
            var Q64;
            Q64=makeQuery(id+"F15.opPattern","COPY",BODY,{"derivedFrom":makeQuery(id+"F8.opExtrude","SWEPT_BODY",BODY,{"disambiguationData":[OSD([sQuery(id+"F5.wireOp",EDGE,"E5.0.2.0")])]}),"instanceName":"17"});
            var Q65;
            Q65=makeQuery(id+"F15.opPattern","COPY",BODY,{"derivedFrom":makeQuery(id+"F8.opExtrude","SWEPT_BODY",BODY,{"disambiguationData":[OSD([sQuery(id+"F5.wireOp",EDGE,"E5.0.1.0")])]}),"instanceName":"17"});
            var Q66;
            Q66=makeQuery(id+"F15.opPattern","COPY",BODY,{"derivedFrom":makeQuery(id+"F8.opExtrude","SWEPT_BODY",BODY,{"disambiguationData":[OSD([sQuery(id+"F5.wireOp",EDGE,"E4")])]}),"instanceName":"17"});
            var Q67;
            Q67=makeQuery(id+"F15.opPattern","COPY",BODY,{"derivedFrom":makeQuery(id+"F8.opExtrude","SWEPT_BODY",BODY,{"disambiguationData":[OSD([sQuery(id+"F5.wireOp",EDGE,"E6.0.1.0")])]}),"instanceName":"17"});
            var Q68;
            Q68=makeQuery(id+"F15.opPattern","COPY",BODY,{"derivedFrom":makeQuery(id+"F8.opExtrude","SWEPT_BODY",BODY,{"disambiguationData":[OSD([sQuery(id+"F5.wireOp",EDGE,"E6.0.2.0")])]}),"instanceName":"17"});
            var Q69;
            Q69=makeQuery(id+"F15.opPattern","COPY",BODY,{"derivedFrom":makeQuery(id+"F8.opExtrude","SWEPT_BODY",BODY,{"disambiguationData":[OSD([sQuery(id+"F5.wireOp",EDGE,"E6.0.3.0")])]}),"instanceName":"17"});
            var Q70;
            Q70=makeQuery(id+"F15.opPattern","COPY",BODY,{"derivedFrom":makeQuery(id+"F8.opExtrude","SWEPT_BODY",BODY,{"disambiguationData":[OSD([sQuery(id+"F5.wireOp",EDGE,"E6.0.4.0")])]}),"instanceName":"17"});
            var Q71;
            Q71=makeQuery(id+"F15.opPattern","COPY",BODY,{"derivedFrom":makeQuery(id+"F13.opExtrude","SWEPT_BODY",BODY,{"disambiguationData":[OSD([sQuery(id+"F11.wireOp",EDGE,"E11.0.3.0")])]}),"instanceName":"30"});
            var Q72;
            Q72=makeQuery(id+"F15.opPattern","COPY",BODY,{"derivedFrom":makeQuery(id+"F13.opExtrude","SWEPT_BODY",BODY,{"disambiguationData":[OSD([sQuery(id+"F11.wireOp",EDGE,"E11.0.2.0")])]}),"instanceName":"30"});
            var Q73;
            Q73=makeQuery(id+"F15.opPattern","COPY",BODY,{"derivedFrom":makeQuery(id+"F13.opExtrude","SWEPT_BODY",BODY,{"disambiguationData":[OSD([sQuery(id+"F11.wireOp",EDGE,"E11.0.1.0")])]}),"instanceName":"30"});
            var Q74;
            Q74=makeQuery(id+"F15.opPattern","COPY",BODY,{"derivedFrom":makeQuery(id+"F13.opExtrude","SWEPT_BODY",BODY,{"disambiguationData":[OSD([sQuery(id+"F11.wireOp",EDGE,"E10.0.3.0")])]}),"instanceName":"30"});
            var Q75;
            Q75=makeQuery(id+"F15.opPattern","COPY",BODY,{"derivedFrom":makeQuery(id+"F13.opExtrude","SWEPT_BODY",BODY,{"disambiguationData":[OSD([sQuery(id+"F11.wireOp",EDGE,"E10.0.2.0")])]}),"instanceName":"30"});
            var Q76;
            Q76=makeQuery(id+"F15.opPattern","COPY",BODY,{"derivedFrom":makeQuery(id+"F13.opExtrude","SWEPT_BODY",BODY,{"disambiguationData":[OSD([sQuery(id+"F11.wireOp",EDGE,"E10.0.1.0")])]}),"instanceName":"30"});
            var Q77;
            Q77=makeQuery(id+"F15.opPattern","COPY",BODY,{"derivedFrom":makeQuery(id+"F13.opExtrude","SWEPT_BODY",BODY,{"disambiguationData":[OSD([sQuery(id+"F11.wireOp",EDGE,"E9")])]}),"instanceName":"30"});
            var Q78;
            Q78=makeQuery(id+"F15.opPattern","COPY",BODY,{"derivedFrom":makeQuery(id+"F13.opExtrude","SWEPT_BODY",BODY,{"disambiguationData":[OSD([sQuery(id+"F11.wireOp",EDGE,"E8")])]}),"instanceName":"30"});
            var Q79;
            Q79=makeQuery(id+"F15.opPattern","COPY",BODY,{"derivedFrom":makeQuery(id+"F8.opExtrude","SWEPT_BODY",BODY,{"disambiguationData":[OSD([sQuery(id+"F5.wireOp",EDGE,"E6.0.4.0")])]}),"instanceName":"30"});
            var Q80;
            Q80=makeQuery(id+"F15.opPattern","COPY",BODY,{"derivedFrom":makeQuery(id+"F8.opExtrude","SWEPT_BODY",BODY,{"disambiguationData":[OSD([sQuery(id+"F5.wireOp",EDGE,"E6.0.3.0")])]}),"instanceName":"30"});
            var Q81;
            Q81=makeQuery(id+"F15.opPattern","COPY",BODY,{"derivedFrom":makeQuery(id+"F8.opExtrude","SWEPT_BODY",BODY,{"disambiguationData":[OSD([sQuery(id+"F5.wireOp",EDGE,"E6.0.2.0")])]}),"instanceName":"30"});
            var Q82;
            Q82=makeQuery(id+"F15.opPattern","COPY",BODY,{"derivedFrom":makeQuery(id+"F8.opExtrude","SWEPT_BODY",BODY,{"disambiguationData":[OSD([sQuery(id+"F5.wireOp",EDGE,"E6.0.1.0")])]}),"instanceName":"30"});
            var Q83;
            Q83=makeQuery(id+"F15.opPattern","COPY",BODY,{"derivedFrom":makeQuery(id+"F8.opExtrude","SWEPT_BODY",BODY,{"disambiguationData":[OSD([sQuery(id+"F5.wireOp",EDGE,"E5.0.4.0")])]}),"instanceName":"30"});
            var Q84;
            Q84=makeQuery(id+"F15.opPattern","COPY",BODY,{"derivedFrom":makeQuery(id+"F8.opExtrude","SWEPT_BODY",BODY,{"disambiguationData":[OSD([sQuery(id+"F5.wireOp",EDGE,"E5.0.3.0")])]}),"instanceName":"30"});
            var Q85;
            Q85=makeQuery(id+"F15.opPattern","COPY",BODY,{"derivedFrom":makeQuery(id+"F8.opExtrude","SWEPT_BODY",BODY,{"disambiguationData":[OSD([sQuery(id+"F5.wireOp",EDGE,"E5.0.2.0")])]}),"instanceName":"30"});
            var Q86;
            Q86=makeQuery(id+"F15.opPattern","COPY",BODY,{"derivedFrom":makeQuery(id+"F8.opExtrude","SWEPT_BODY",BODY,{"disambiguationData":[OSD([sQuery(id+"F5.wireOp",EDGE,"E5.0.1.0")])]}),"instanceName":"30"});
            var Q87;
            Q87=makeQuery(id+"F15.opPattern","COPY",BODY,{"derivedFrom":makeQuery(id+"F8.opExtrude","SWEPT_BODY",BODY,{"disambiguationData":[OSD([sQuery(id+"F5.wireOp",EDGE,"E4")])]}),"instanceName":"30"});
            var Q88;
            Q88=makeQuery(id+"F15.opPattern","COPY",BODY,{"derivedFrom":makeQuery(id+"F13.opExtrude","SWEPT_BODY",BODY,{"disambiguationData":[OSD([sQuery(id+"F11.wireOp",EDGE,"E11.0.3.0")])]}),"instanceName":"29"});
            var Q89;
            Q89=makeQuery(id+"F15.opPattern","COPY",BODY,{"derivedFrom":makeQuery(id+"F13.opExtrude","SWEPT_BODY",BODY,{"disambiguationData":[OSD([sQuery(id+"F11.wireOp",EDGE,"E11.0.2.0")])]}),"instanceName":"29"});
            var Q90;
            Q90=makeQuery(id+"F15.opPattern","COPY",BODY,{"derivedFrom":makeQuery(id+"F13.opExtrude","SWEPT_BODY",BODY,{"disambiguationData":[OSD([sQuery(id+"F11.wireOp",EDGE,"E11.0.1.0")])]}),"instanceName":"29"});
            var Q91;
            Q91=makeQuery(id+"F15.opPattern","COPY",BODY,{"derivedFrom":makeQuery(id+"F13.opExtrude","SWEPT_BODY",BODY,{"disambiguationData":[OSD([sQuery(id+"F11.wireOp",EDGE,"E10.0.3.0")])]}),"instanceName":"29"});
            var Q92;
            Q92=makeQuery(id+"F15.opPattern","COPY",BODY,{"derivedFrom":makeQuery(id+"F13.opExtrude","SWEPT_BODY",BODY,{"disambiguationData":[OSD([sQuery(id+"F11.wireOp",EDGE,"E10.0.2.0")])]}),"instanceName":"29"});
            var Q93;
            Q93=makeQuery(id+"F15.opPattern","COPY",BODY,{"derivedFrom":makeQuery(id+"F13.opExtrude","SWEPT_BODY",BODY,{"disambiguationData":[OSD([sQuery(id+"F11.wireOp",EDGE,"E10.0.1.0")])]}),"instanceName":"29"});
            var Q94;
            Q94=makeQuery(id+"F15.opPattern","COPY",BODY,{"derivedFrom":makeQuery(id+"F13.opExtrude","SWEPT_BODY",BODY,{"disambiguationData":[OSD([sQuery(id+"F11.wireOp",EDGE,"E9")])]}),"instanceName":"29"});
            var Q95;
            Q95=makeQuery(id+"F15.opPattern","COPY",BODY,{"derivedFrom":makeQuery(id+"F13.opExtrude","SWEPT_BODY",BODY,{"disambiguationData":[OSD([sQuery(id+"F11.wireOp",EDGE,"E8")])]}),"instanceName":"29"});
            var Q96;
            Q96=makeQuery(id+"F15.opPattern","COPY",BODY,{"derivedFrom":makeQuery(id+"F8.opExtrude","SWEPT_BODY",BODY,{"disambiguationData":[OSD([sQuery(id+"F5.wireOp",EDGE,"E6.0.4.0")])]}),"instanceName":"29"});
            var Q97;
            Q97=makeQuery(id+"F15.opPattern","COPY",BODY,{"derivedFrom":makeQuery(id+"F8.opExtrude","SWEPT_BODY",BODY,{"disambiguationData":[OSD([sQuery(id+"F5.wireOp",EDGE,"E6.0.3.0")])]}),"instanceName":"29"});
            var Q98;
            Q98=makeQuery(id+"F15.opPattern","COPY",BODY,{"derivedFrom":makeQuery(id+"F8.opExtrude","SWEPT_BODY",BODY,{"disambiguationData":[OSD([sQuery(id+"F5.wireOp",EDGE,"E6.0.2.0")])]}),"instanceName":"29"});
            var Q99;
            Q99=makeQuery(id+"F15.opPattern","COPY",BODY,{"derivedFrom":makeQuery(id+"F8.opExtrude","SWEPT_BODY",BODY,{"disambiguationData":[OSD([sQuery(id+"F5.wireOp",EDGE,"E6.0.1.0")])]}),"instanceName":"29"});
            var Q100;
            Q100=makeQuery(id+"F15.opPattern","COPY",BODY,{"derivedFrom":makeQuery(id+"F8.opExtrude","SWEPT_BODY",BODY,{"disambiguationData":[OSD([sQuery(id+"F5.wireOp",EDGE,"E5.0.4.0")])]}),"instanceName":"29"});
            var Q101;
            Q101=makeQuery(id+"F15.opPattern","COPY",BODY,{"derivedFrom":makeQuery(id+"F8.opExtrude","SWEPT_BODY",BODY,{"disambiguationData":[OSD([sQuery(id+"F5.wireOp",EDGE,"E5.0.3.0")])]}),"instanceName":"29"});
            var Q102;
            Q102=makeQuery(id+"F15.opPattern","COPY",BODY,{"derivedFrom":makeQuery(id+"F8.opExtrude","SWEPT_BODY",BODY,{"disambiguationData":[OSD([sQuery(id+"F5.wireOp",EDGE,"E5.0.2.0")])]}),"instanceName":"29"});
            var Q103;
            Q103=makeQuery(id+"F15.opPattern","COPY",BODY,{"derivedFrom":makeQuery(id+"F8.opExtrude","SWEPT_BODY",BODY,{"disambiguationData":[OSD([sQuery(id+"F5.wireOp",EDGE,"E5.0.1.0")])]}),"instanceName":"29"});
            var Q104;
            Q104=makeQuery(id+"F15.opPattern","COPY",BODY,{"derivedFrom":makeQuery(id+"F8.opExtrude","SWEPT_BODY",BODY,{"disambiguationData":[OSD([sQuery(id+"F5.wireOp",EDGE,"E4")])]}),"instanceName":"29"});
            var Q105;
            Q105=makeQuery(id+"F15.opPattern","COPY",BODY,{"derivedFrom":makeQuery(id+"F13.opExtrude","SWEPT_BODY",BODY,{"disambiguationData":[OSD([sQuery(id+"F11.wireOp",EDGE,"E11.0.3.0")])]}),"instanceName":"28"});
            var Q106;
            Q106=makeQuery(id+"F15.opPattern","COPY",BODY,{"derivedFrom":makeQuery(id+"F13.opExtrude","SWEPT_BODY",BODY,{"disambiguationData":[OSD([sQuery(id+"F11.wireOp",EDGE,"E11.0.2.0")])]}),"instanceName":"28"});
            var Q107;
            Q107=makeQuery(id+"F15.opPattern","COPY",BODY,{"derivedFrom":makeQuery(id+"F13.opExtrude","SWEPT_BODY",BODY,{"disambiguationData":[OSD([sQuery(id+"F11.wireOp",EDGE,"E11.0.1.0")])]}),"instanceName":"28"});
            var Q108;
            Q108=makeQuery(id+"F15.opPattern","COPY",BODY,{"derivedFrom":makeQuery(id+"F13.opExtrude","SWEPT_BODY",BODY,{"disambiguationData":[OSD([sQuery(id+"F11.wireOp",EDGE,"E10.0.3.0")])]}),"instanceName":"28"});
            var Q109;
            Q109=makeQuery(id+"F15.opPattern","COPY",BODY,{"derivedFrom":makeQuery(id+"F13.opExtrude","SWEPT_BODY",BODY,{"disambiguationData":[OSD([sQuery(id+"F11.wireOp",EDGE,"E10.0.2.0")])]}),"instanceName":"28"});
            var Q110;
            Q110=makeQuery(id+"F15.opPattern","COPY",BODY,{"derivedFrom":makeQuery(id+"F13.opExtrude","SWEPT_BODY",BODY,{"disambiguationData":[OSD([sQuery(id+"F11.wireOp",EDGE,"E10.0.1.0")])]}),"instanceName":"28"});
            var Q111;
            Q111=makeQuery(id+"F15.opPattern","COPY",BODY,{"derivedFrom":makeQuery(id+"F13.opExtrude","SWEPT_BODY",BODY,{"disambiguationData":[OSD([sQuery(id+"F11.wireOp",EDGE,"E9")])]}),"instanceName":"28"});
            var Q112;
            Q112=makeQuery(id+"F15.opPattern","COPY",BODY,{"derivedFrom":makeQuery(id+"F13.opExtrude","SWEPT_BODY",BODY,{"disambiguationData":[OSD([sQuery(id+"F11.wireOp",EDGE,"E8")])]}),"instanceName":"28"});
            var Q113;
            Q113=makeQuery(id+"F15.opPattern","COPY",BODY,{"derivedFrom":makeQuery(id+"F8.opExtrude","SWEPT_BODY",BODY,{"disambiguationData":[OSD([sQuery(id+"F5.wireOp",EDGE,"E6.0.4.0")])]}),"instanceName":"28"});
            var Q114;
            Q114=makeQuery(id+"F15.opPattern","COPY",BODY,{"derivedFrom":makeQuery(id+"F8.opExtrude","SWEPT_BODY",BODY,{"disambiguationData":[OSD([sQuery(id+"F5.wireOp",EDGE,"E6.0.3.0")])]}),"instanceName":"28"});
            var Q115;
            Q115=makeQuery(id+"F15.opPattern","COPY",BODY,{"derivedFrom":makeQuery(id+"F8.opExtrude","SWEPT_BODY",BODY,{"disambiguationData":[OSD([sQuery(id+"F5.wireOp",EDGE,"E6.0.2.0")])]}),"instanceName":"28"});
            var Q116;
            Q116=makeQuery(id+"F15.opPattern","COPY",BODY,{"derivedFrom":makeQuery(id+"F8.opExtrude","SWEPT_BODY",BODY,{"disambiguationData":[OSD([sQuery(id+"F5.wireOp",EDGE,"E6.0.1.0")])]}),"instanceName":"28"});
            var Q117;
            Q117=makeQuery(id+"F15.opPattern","COPY",BODY,{"derivedFrom":makeQuery(id+"F8.opExtrude","SWEPT_BODY",BODY,{"disambiguationData":[OSD([sQuery(id+"F5.wireOp",EDGE,"E5.0.4.0")])]}),"instanceName":"28"});
            var Q118;
            Q118=makeQuery(id+"F15.opPattern","COPY",BODY,{"derivedFrom":makeQuery(id+"F8.opExtrude","SWEPT_BODY",BODY,{"disambiguationData":[OSD([sQuery(id+"F5.wireOp",EDGE,"E5.0.3.0")])]}),"instanceName":"28"});
            var Q119;
            Q119=makeQuery(id+"F15.opPattern","COPY",BODY,{"derivedFrom":makeQuery(id+"F8.opExtrude","SWEPT_BODY",BODY,{"disambiguationData":[OSD([sQuery(id+"F5.wireOp",EDGE,"E5.0.2.0")])]}),"instanceName":"28"});
            var Q120;
            Q120=makeQuery(id+"F15.opPattern","COPY",BODY,{"derivedFrom":makeQuery(id+"F8.opExtrude","SWEPT_BODY",BODY,{"disambiguationData":[OSD([sQuery(id+"F5.wireOp",EDGE,"E5.0.1.0")])]}),"instanceName":"28"});
            var Q121;
            Q121=makeQuery(id+"F15.opPattern","COPY",BODY,{"derivedFrom":makeQuery(id+"F8.opExtrude","SWEPT_BODY",BODY,{"disambiguationData":[OSD([sQuery(id+"F5.wireOp",EDGE,"E4")])]}),"instanceName":"28"});
            var Q122;
            Q122=makeQuery(id+"F15.opPattern","COPY",BODY,{"derivedFrom":makeQuery(id+"F13.opExtrude","SWEPT_BODY",BODY,{"disambiguationData":[OSD([sQuery(id+"F11.wireOp",EDGE,"E11.0.3.0")])]}),"instanceName":"27"});
            var Q123;
            Q123=makeQuery(id+"F15.opPattern","COPY",BODY,{"derivedFrom":makeQuery(id+"F13.opExtrude","SWEPT_BODY",BODY,{"disambiguationData":[OSD([sQuery(id+"F11.wireOp",EDGE,"E11.0.2.0")])]}),"instanceName":"27"});
            var Q124;
            Q124=makeQuery(id+"F15.opPattern","COPY",BODY,{"derivedFrom":makeQuery(id+"F13.opExtrude","SWEPT_BODY",BODY,{"disambiguationData":[OSD([sQuery(id+"F11.wireOp",EDGE,"E11.0.1.0")])]}),"instanceName":"27"});
            var Q125;
            Q125=makeQuery(id+"F15.opPattern","COPY",BODY,{"derivedFrom":makeQuery(id+"F13.opExtrude","SWEPT_BODY",BODY,{"disambiguationData":[OSD([sQuery(id+"F11.wireOp",EDGE,"E10.0.3.0")])]}),"instanceName":"27"});
            var Q126;
            Q126=makeQuery(id+"F15.opPattern","COPY",BODY,{"derivedFrom":makeQuery(id+"F13.opExtrude","SWEPT_BODY",BODY,{"disambiguationData":[OSD([sQuery(id+"F11.wireOp",EDGE,"E10.0.2.0")])]}),"instanceName":"27"});
            var Q127;
            Q127=makeQuery(id+"F15.opPattern","COPY",BODY,{"derivedFrom":makeQuery(id+"F13.opExtrude","SWEPT_BODY",BODY,{"disambiguationData":[OSD([sQuery(id+"F11.wireOp",EDGE,"E10.0.1.0")])]}),"instanceName":"27"});
            var Q128;
            Q128=makeQuery(id+"F15.opPattern","COPY",BODY,{"derivedFrom":makeQuery(id+"F13.opExtrude","SWEPT_BODY",BODY,{"disambiguationData":[OSD([sQuery(id+"F11.wireOp",EDGE,"E9")])]}),"instanceName":"27"});
            var Q129;
            Q129=makeQuery(id+"F15.opPattern","COPY",BODY,{"derivedFrom":makeQuery(id+"F13.opExtrude","SWEPT_BODY",BODY,{"disambiguationData":[OSD([sQuery(id+"F11.wireOp",EDGE,"E8")])]}),"instanceName":"27"});
            var Q130;
            Q130=makeQuery(id+"F15.opPattern","COPY",BODY,{"derivedFrom":makeQuery(id+"F8.opExtrude","SWEPT_BODY",BODY,{"disambiguationData":[OSD([sQuery(id+"F5.wireOp",EDGE,"E6.0.4.0")])]}),"instanceName":"27"});
            var Q131;
            Q131=makeQuery(id+"F15.opPattern","COPY",BODY,{"derivedFrom":makeQuery(id+"F8.opExtrude","SWEPT_BODY",BODY,{"disambiguationData":[OSD([sQuery(id+"F5.wireOp",EDGE,"E6.0.3.0")])]}),"instanceName":"27"});
            var Q132;
            Q132=makeQuery(id+"F15.opPattern","COPY",BODY,{"derivedFrom":makeQuery(id+"F8.opExtrude","SWEPT_BODY",BODY,{"disambiguationData":[OSD([sQuery(id+"F5.wireOp",EDGE,"E6.0.2.0")])]}),"instanceName":"27"});
            var Q133;
            Q133=makeQuery(id+"F15.opPattern","COPY",BODY,{"derivedFrom":makeQuery(id+"F8.opExtrude","SWEPT_BODY",BODY,{"disambiguationData":[OSD([sQuery(id+"F5.wireOp",EDGE,"E6.0.1.0")])]}),"instanceName":"27"});
            var Q134;
            Q134=makeQuery(id+"F15.opPattern","COPY",BODY,{"derivedFrom":makeQuery(id+"F8.opExtrude","SWEPT_BODY",BODY,{"disambiguationData":[OSD([sQuery(id+"F5.wireOp",EDGE,"E5.0.4.0")])]}),"instanceName":"27"});
            var Q135;
            Q135=makeQuery(id+"F15.opPattern","COPY",BODY,{"derivedFrom":makeQuery(id+"F8.opExtrude","SWEPT_BODY",BODY,{"disambiguationData":[OSD([sQuery(id+"F5.wireOp",EDGE,"E5.0.3.0")])]}),"instanceName":"27"});
            var Q136;
            Q136=makeQuery(id+"F15.opPattern","COPY",BODY,{"derivedFrom":makeQuery(id+"F8.opExtrude","SWEPT_BODY",BODY,{"disambiguationData":[OSD([sQuery(id+"F5.wireOp",EDGE,"E5.0.2.0")])]}),"instanceName":"27"});
            var Q137;
            Q137=makeQuery(id+"F15.opPattern","COPY",BODY,{"derivedFrom":makeQuery(id+"F8.opExtrude","SWEPT_BODY",BODY,{"disambiguationData":[OSD([sQuery(id+"F5.wireOp",EDGE,"E5.0.1.0")])]}),"instanceName":"27"});
            var Q138;
            Q138=makeQuery(id+"F15.opPattern","COPY",BODY,{"derivedFrom":makeQuery(id+"F8.opExtrude","SWEPT_BODY",BODY,{"disambiguationData":[OSD([sQuery(id+"F5.wireOp",EDGE,"E4")])]}),"instanceName":"27"});
            var Q139;
            Q139=makeQuery(id+"F15.opPattern","COPY",BODY,{"derivedFrom":makeQuery(id+"F13.opExtrude","SWEPT_BODY",BODY,{"disambiguationData":[OSD([sQuery(id+"F11.wireOp",EDGE,"E11.0.3.0")])]}),"instanceName":"26"});
            var Q140;
            Q140=makeQuery(id+"F15.opPattern","COPY",BODY,{"derivedFrom":makeQuery(id+"F13.opExtrude","SWEPT_BODY",BODY,{"disambiguationData":[OSD([sQuery(id+"F11.wireOp",EDGE,"E11.0.2.0")])]}),"instanceName":"26"});
            var Q141;
            Q141=makeQuery(id+"F15.opPattern","COPY",BODY,{"derivedFrom":makeQuery(id+"F13.opExtrude","SWEPT_BODY",BODY,{"disambiguationData":[OSD([sQuery(id+"F11.wireOp",EDGE,"E11.0.1.0")])]}),"instanceName":"26"});
            var Q142;
            Q142=makeQuery(id+"F15.opPattern","COPY",BODY,{"derivedFrom":makeQuery(id+"F13.opExtrude","SWEPT_BODY",BODY,{"disambiguationData":[OSD([sQuery(id+"F11.wireOp",EDGE,"E10.0.3.0")])]}),"instanceName":"26"});
            var Q143;
            Q143=makeQuery(id+"F15.opPattern","COPY",BODY,{"derivedFrom":makeQuery(id+"F13.opExtrude","SWEPT_BODY",BODY,{"disambiguationData":[OSD([sQuery(id+"F11.wireOp",EDGE,"E10.0.2.0")])]}),"instanceName":"26"});
            var Q144;
            Q144=makeQuery(id+"F15.opPattern","COPY",BODY,{"derivedFrom":makeQuery(id+"F13.opExtrude","SWEPT_BODY",BODY,{"disambiguationData":[OSD([sQuery(id+"F11.wireOp",EDGE,"E10.0.1.0")])]}),"instanceName":"26"});
            var Q145;
            Q145=makeQuery(id+"F15.opPattern","COPY",BODY,{"derivedFrom":makeQuery(id+"F13.opExtrude","SWEPT_BODY",BODY,{"disambiguationData":[OSD([sQuery(id+"F11.wireOp",EDGE,"E9")])]}),"instanceName":"26"});
            var Q146;
            Q146=makeQuery(id+"F15.opPattern","COPY",BODY,{"derivedFrom":makeQuery(id+"F13.opExtrude","SWEPT_BODY",BODY,{"disambiguationData":[OSD([sQuery(id+"F11.wireOp",EDGE,"E8")])]}),"instanceName":"26"});
            var Q147;
            Q147=makeQuery(id+"F15.opPattern","COPY",BODY,{"derivedFrom":makeQuery(id+"F8.opExtrude","SWEPT_BODY",BODY,{"disambiguationData":[OSD([sQuery(id+"F5.wireOp",EDGE,"E6.0.4.0")])]}),"instanceName":"26"});
            var Q148;
            Q148=makeQuery(id+"F15.opPattern","COPY",BODY,{"derivedFrom":makeQuery(id+"F8.opExtrude","SWEPT_BODY",BODY,{"disambiguationData":[OSD([sQuery(id+"F5.wireOp",EDGE,"E6.0.3.0")])]}),"instanceName":"26"});
            var Q149;
            Q149=makeQuery(id+"F15.opPattern","COPY",BODY,{"derivedFrom":makeQuery(id+"F8.opExtrude","SWEPT_BODY",BODY,{"disambiguationData":[OSD([sQuery(id+"F5.wireOp",EDGE,"E6.0.2.0")])]}),"instanceName":"26"});
            var Q150;
            Q150=makeQuery(id+"F15.opPattern","COPY",BODY,{"derivedFrom":makeQuery(id+"F8.opExtrude","SWEPT_BODY",BODY,{"disambiguationData":[OSD([sQuery(id+"F5.wireOp",EDGE,"E6.0.1.0")])]}),"instanceName":"26"});
            var Q151;
            Q151=makeQuery(id+"F15.opPattern","COPY",BODY,{"derivedFrom":makeQuery(id+"F8.opExtrude","SWEPT_BODY",BODY,{"disambiguationData":[OSD([sQuery(id+"F5.wireOp",EDGE,"E5.0.4.0")])]}),"instanceName":"26"});
            var Q152;
            Q152=makeQuery(id+"F15.opPattern","COPY",BODY,{"derivedFrom":makeQuery(id+"F8.opExtrude","SWEPT_BODY",BODY,{"disambiguationData":[OSD([sQuery(id+"F5.wireOp",EDGE,"E5.0.3.0")])]}),"instanceName":"26"});
            var Q153;
            Q153=makeQuery(id+"F15.opPattern","COPY",BODY,{"derivedFrom":makeQuery(id+"F8.opExtrude","SWEPT_BODY",BODY,{"disambiguationData":[OSD([sQuery(id+"F5.wireOp",EDGE,"E5.0.2.0")])]}),"instanceName":"26"});
            var Q154;
            Q154=makeQuery(id+"F15.opPattern","COPY",BODY,{"derivedFrom":makeQuery(id+"F8.opExtrude","SWEPT_BODY",BODY,{"disambiguationData":[OSD([sQuery(id+"F5.wireOp",EDGE,"E5.0.1.0")])]}),"instanceName":"26"});
            var Q155;
            Q155=makeQuery(id+"F15.opPattern","COPY",BODY,{"derivedFrom":makeQuery(id+"F8.opExtrude","SWEPT_BODY",BODY,{"disambiguationData":[OSD([sQuery(id+"F5.wireOp",EDGE,"E4")])]}),"instanceName":"26"});
            var Q156;
            Q156=makeQuery(id+"F15.opPattern","COPY",BODY,{"derivedFrom":makeQuery(id+"F13.opExtrude","SWEPT_BODY",BODY,{"disambiguationData":[OSD([sQuery(id+"F11.wireOp",EDGE,"E11.0.3.0")])]}),"instanceName":"25"});
            var Q157;
            Q157=makeQuery(id+"F15.opPattern","COPY",BODY,{"derivedFrom":makeQuery(id+"F13.opExtrude","SWEPT_BODY",BODY,{"disambiguationData":[OSD([sQuery(id+"F11.wireOp",EDGE,"E11.0.2.0")])]}),"instanceName":"25"});
            var Q158;
            Q158=makeQuery(id+"F15.opPattern","COPY",BODY,{"derivedFrom":makeQuery(id+"F13.opExtrude","SWEPT_BODY",BODY,{"disambiguationData":[OSD([sQuery(id+"F11.wireOp",EDGE,"E11.0.1.0")])]}),"instanceName":"25"});
            var Q159;
            Q159=makeQuery(id+"F15.opPattern","COPY",BODY,{"derivedFrom":makeQuery(id+"F13.opExtrude","SWEPT_BODY",BODY,{"disambiguationData":[OSD([sQuery(id+"F11.wireOp",EDGE,"E10.0.3.0")])]}),"instanceName":"25"});
            var Q160;
            Q160=makeQuery(id+"F15.opPattern","COPY",BODY,{"derivedFrom":makeQuery(id+"F13.opExtrude","SWEPT_BODY",BODY,{"disambiguationData":[OSD([sQuery(id+"F11.wireOp",EDGE,"E10.0.2.0")])]}),"instanceName":"25"});
            var Q161;
            Q161=makeQuery(id+"F15.opPattern","COPY",BODY,{"derivedFrom":makeQuery(id+"F13.opExtrude","SWEPT_BODY",BODY,{"disambiguationData":[OSD([sQuery(id+"F11.wireOp",EDGE,"E10.0.1.0")])]}),"instanceName":"25"});
            var Q162;
            Q162=makeQuery(id+"F15.opPattern","COPY",BODY,{"derivedFrom":makeQuery(id+"F13.opExtrude","SWEPT_BODY",BODY,{"disambiguationData":[OSD([sQuery(id+"F11.wireOp",EDGE,"E9")])]}),"instanceName":"25"});
            var Q163;
            Q163=makeQuery(id+"F15.opPattern","COPY",BODY,{"derivedFrom":makeQuery(id+"F13.opExtrude","SWEPT_BODY",BODY,{"disambiguationData":[OSD([sQuery(id+"F11.wireOp",EDGE,"E8")])]}),"instanceName":"25"});
            var Q164;
            Q164=makeQuery(id+"F15.opPattern","COPY",BODY,{"derivedFrom":makeQuery(id+"F8.opExtrude","SWEPT_BODY",BODY,{"disambiguationData":[OSD([sQuery(id+"F5.wireOp",EDGE,"E6.0.4.0")])]}),"instanceName":"25"});
            var Q165;
            Q165=makeQuery(id+"F15.opPattern","COPY",BODY,{"derivedFrom":makeQuery(id+"F8.opExtrude","SWEPT_BODY",BODY,{"disambiguationData":[OSD([sQuery(id+"F5.wireOp",EDGE,"E6.0.3.0")])]}),"instanceName":"25"});
            var Q166;
            Q166=makeQuery(id+"F15.opPattern","COPY",BODY,{"derivedFrom":makeQuery(id+"F8.opExtrude","SWEPT_BODY",BODY,{"disambiguationData":[OSD([sQuery(id+"F5.wireOp",EDGE,"E6.0.2.0")])]}),"instanceName":"25"});
            var Q167;
            Q167=makeQuery(id+"F15.opPattern","COPY",BODY,{"derivedFrom":makeQuery(id+"F8.opExtrude","SWEPT_BODY",BODY,{"disambiguationData":[OSD([sQuery(id+"F5.wireOp",EDGE,"E6.0.1.0")])]}),"instanceName":"25"});
            var Q168;
            Q168=makeQuery(id+"F15.opPattern","COPY",BODY,{"derivedFrom":makeQuery(id+"F8.opExtrude","SWEPT_BODY",BODY,{"disambiguationData":[OSD([sQuery(id+"F5.wireOp",EDGE,"E5.0.3.0")])]}),"instanceName":"25"});
            var Q169;
            Q169=makeQuery(id+"F15.opPattern","COPY",BODY,{"derivedFrom":makeQuery(id+"F8.opExtrude","SWEPT_BODY",BODY,{"disambiguationData":[OSD([sQuery(id+"F5.wireOp",EDGE,"E5.0.2.0")])]}),"instanceName":"25"});
            var Q170;
            Q170=makeQuery(id+"F15.opPattern","COPY",BODY,{"derivedFrom":makeQuery(id+"F8.opExtrude","SWEPT_BODY",BODY,{"disambiguationData":[OSD([sQuery(id+"F5.wireOp",EDGE,"E5.0.1.0")])]}),"instanceName":"25"});
            var Q171;
            Q171=makeQuery(id+"F15.opPattern","COPY",BODY,{"derivedFrom":makeQuery(id+"F8.opExtrude","SWEPT_BODY",BODY,{"disambiguationData":[OSD([sQuery(id+"F5.wireOp",EDGE,"E4")])]}),"instanceName":"25"});
            var Q172;
            Q172=makeQuery(id+"F15.opPattern","COPY",BODY,{"derivedFrom":makeQuery(id+"F13.opExtrude","SWEPT_BODY",BODY,{"disambiguationData":[OSD([sQuery(id+"F11.wireOp",EDGE,"E11.0.3.0")])]}),"instanceName":"24"});
            var Q173;
            Q173=makeQuery(id+"F15.opPattern","COPY",BODY,{"derivedFrom":makeQuery(id+"F13.opExtrude","SWEPT_BODY",BODY,{"disambiguationData":[OSD([sQuery(id+"F11.wireOp",EDGE,"E11.0.2.0")])]}),"instanceName":"24"});
            var Q174;
            Q174=makeQuery(id+"F15.opPattern","COPY",BODY,{"derivedFrom":makeQuery(id+"F13.opExtrude","SWEPT_BODY",BODY,{"disambiguationData":[OSD([sQuery(id+"F11.wireOp",EDGE,"E11.0.1.0")])]}),"instanceName":"24"});
            var Q175;
            Q175=makeQuery(id+"F15.opPattern","COPY",BODY,{"derivedFrom":makeQuery(id+"F13.opExtrude","SWEPT_BODY",BODY,{"disambiguationData":[OSD([sQuery(id+"F11.wireOp",EDGE,"E10.0.3.0")])]}),"instanceName":"24"});
            var Q176;
            Q176=makeQuery(id+"F15.opPattern","COPY",BODY,{"derivedFrom":makeQuery(id+"F13.opExtrude","SWEPT_BODY",BODY,{"disambiguationData":[OSD([sQuery(id+"F11.wireOp",EDGE,"E10.0.2.0")])]}),"instanceName":"24"});
            var Q177;
            Q177=makeQuery(id+"F15.opPattern","COPY",BODY,{"derivedFrom":makeQuery(id+"F13.opExtrude","SWEPT_BODY",BODY,{"disambiguationData":[OSD([sQuery(id+"F11.wireOp",EDGE,"E10.0.1.0")])]}),"instanceName":"24"});
            var Q178;
            Q178=makeQuery(id+"F15.opPattern","COPY",BODY,{"derivedFrom":makeQuery(id+"F13.opExtrude","SWEPT_BODY",BODY,{"disambiguationData":[OSD([sQuery(id+"F11.wireOp",EDGE,"E9")])]}),"instanceName":"24"});
            var Q179;
            Q179=makeQuery(id+"F15.opPattern","COPY",BODY,{"derivedFrom":makeQuery(id+"F13.opExtrude","SWEPT_BODY",BODY,{"disambiguationData":[OSD([sQuery(id+"F11.wireOp",EDGE,"E8")])]}),"instanceName":"24"});
            var Q180;
            Q180=makeQuery(id+"F15.opPattern","COPY",BODY,{"derivedFrom":makeQuery(id+"F8.opExtrude","SWEPT_BODY",BODY,{"disambiguationData":[OSD([sQuery(id+"F5.wireOp",EDGE,"E6.0.4.0")])]}),"instanceName":"24"});
            var Q181;
            Q181=makeQuery(id+"F15.opPattern","COPY",BODY,{"derivedFrom":makeQuery(id+"F8.opExtrude","SWEPT_BODY",BODY,{"disambiguationData":[OSD([sQuery(id+"F5.wireOp",EDGE,"E6.0.3.0")])]}),"instanceName":"24"});
            var Q182;
            Q182=makeQuery(id+"F15.opPattern","COPY",BODY,{"derivedFrom":makeQuery(id+"F8.opExtrude","SWEPT_BODY",BODY,{"disambiguationData":[OSD([sQuery(id+"F5.wireOp",EDGE,"E6.0.2.0")])]}),"instanceName":"24"});
            var Q183;
            Q183=makeQuery(id+"F15.opPattern","COPY",BODY,{"derivedFrom":makeQuery(id+"F8.opExtrude","SWEPT_BODY",BODY,{"disambiguationData":[OSD([sQuery(id+"F5.wireOp",EDGE,"E5.0.2.0")])]}),"instanceName":"24"});
            var Q184;
            Q184=makeQuery(id+"F15.opPattern","COPY",BODY,{"derivedFrom":makeQuery(id+"F8.opExtrude","SWEPT_BODY",BODY,{"disambiguationData":[OSD([sQuery(id+"F5.wireOp",EDGE,"E5.0.1.0")])]}),"instanceName":"24"});
            var Q185;
            Q185=makeQuery(id+"F15.opPattern","COPY",BODY,{"derivedFrom":makeQuery(id+"F8.opExtrude","SWEPT_BODY",BODY,{"disambiguationData":[OSD([sQuery(id+"F5.wireOp",EDGE,"E4")])]}),"instanceName":"24"});
            var Q186;
            Q186=makeQuery(id+"F15.opPattern","COPY",BODY,{"derivedFrom":makeQuery(id+"F13.opExtrude","SWEPT_BODY",BODY,{"disambiguationData":[OSD([sQuery(id+"F11.wireOp",EDGE,"E11.0.3.0")])]}),"instanceName":"23"});
            var Q187;
            Q187=makeQuery(id+"F15.opPattern","COPY",BODY,{"derivedFrom":makeQuery(id+"F13.opExtrude","SWEPT_BODY",BODY,{"disambiguationData":[OSD([sQuery(id+"F11.wireOp",EDGE,"E11.0.2.0")])]}),"instanceName":"23"});
            var Q188;
            Q188=makeQuery(id+"F15.opPattern","COPY",BODY,{"derivedFrom":makeQuery(id+"F13.opExtrude","SWEPT_BODY",BODY,{"disambiguationData":[OSD([sQuery(id+"F11.wireOp",EDGE,"E11.0.1.0")])]}),"instanceName":"23"});
            var Q189;
            Q189=makeQuery(id+"F15.opPattern","COPY",BODY,{"derivedFrom":makeQuery(id+"F13.opExtrude","SWEPT_BODY",BODY,{"disambiguationData":[OSD([sQuery(id+"F11.wireOp",EDGE,"E10.0.2.0")])]}),"instanceName":"23"});
            var Q190;
            Q190=makeQuery(id+"F15.opPattern","COPY",BODY,{"derivedFrom":makeQuery(id+"F13.opExtrude","SWEPT_BODY",BODY,{"disambiguationData":[OSD([sQuery(id+"F11.wireOp",EDGE,"E10.0.1.0")])]}),"instanceName":"23"});
            var Q191;
            Q191=makeQuery(id+"F15.opPattern","COPY",BODY,{"derivedFrom":makeQuery(id+"F13.opExtrude","SWEPT_BODY",BODY,{"disambiguationData":[OSD([sQuery(id+"F11.wireOp",EDGE,"E9")])]}),"instanceName":"23"});
            var Q192;
            Q192=makeQuery(id+"F15.opPattern","COPY",BODY,{"derivedFrom":makeQuery(id+"F13.opExtrude","SWEPT_BODY",BODY,{"disambiguationData":[OSD([sQuery(id+"F11.wireOp",EDGE,"E8")])]}),"instanceName":"23"});
            var Q193;
            Q193=makeQuery(id+"F15.opPattern","COPY",BODY,{"derivedFrom":makeQuery(id+"F8.opExtrude","SWEPT_BODY",BODY,{"disambiguationData":[OSD([sQuery(id+"F5.wireOp",EDGE,"E6.0.4.0")])]}),"instanceName":"23"});
            var Q194;
            Q194=makeQuery(id+"F15.opPattern","COPY",BODY,{"derivedFrom":makeQuery(id+"F8.opExtrude","SWEPT_BODY",BODY,{"disambiguationData":[OSD([sQuery(id+"F5.wireOp",EDGE,"E6.0.3.0")])]}),"instanceName":"23"});
            var Q195;
            Q195=makeQuery(id+"F15.opPattern","COPY",BODY,{"derivedFrom":makeQuery(id+"F8.opExtrude","SWEPT_BODY",BODY,{"disambiguationData":[OSD([sQuery(id+"F5.wireOp",EDGE,"E6.0.2.0")])]}),"instanceName":"23"});
            var Q196;
            Q196=makeQuery(id+"F15.opPattern","COPY",BODY,{"derivedFrom":makeQuery(id+"F13.opExtrude","SWEPT_BODY",BODY,{"disambiguationData":[OSD([sQuery(id+"F11.wireOp",EDGE,"E10.0.3.0")])]}),"instanceName":"23"});
            var Q197;
            Q197=makeQuery(id+"F15.opPattern","COPY",BODY,{"derivedFrom":makeQuery(id+"F8.opExtrude","SWEPT_BODY",BODY,{"disambiguationData":[OSD([sQuery(id+"F5.wireOp",EDGE,"E5.0.3.0")])]}),"instanceName":"24"});
            var Q198;
            Q198=makeQuery(id+"F15.opPattern","COPY",BODY,{"derivedFrom":makeQuery(id+"F8.opExtrude","SWEPT_BODY",BODY,{"disambiguationData":[OSD([sQuery(id+"F5.wireOp",EDGE,"E5.0.4.0")])]}),"instanceName":"24"});
            var Q199;
            Q199=makeQuery(id+"F15.opPattern","COPY",BODY,{"derivedFrom":makeQuery(id+"F8.opExtrude","SWEPT_BODY",BODY,{"disambiguationData":[OSD([sQuery(id+"F5.wireOp",EDGE,"E6.0.1.0")])]}),"instanceName":"24"});
            var Q200;
            Q200=makeQuery(id+"F15.opPattern","COPY",BODY,{"derivedFrom":makeQuery(id+"F8.opExtrude","SWEPT_BODY",BODY,{"disambiguationData":[OSD([sQuery(id+"F5.wireOp",EDGE,"E6.0.1.0")])]}),"instanceName":"23"});
            var Q201;
            Q201=makeQuery(id+"F15.opPattern","COPY",BODY,{"derivedFrom":makeQuery(id+"F8.opExtrude","SWEPT_BODY",BODY,{"disambiguationData":[OSD([sQuery(id+"F5.wireOp",EDGE,"E5.0.4.0")])]}),"instanceName":"23"});
            var Q202;
            Q202=makeQuery(id+"F15.opPattern","COPY",BODY,{"derivedFrom":makeQuery(id+"F8.opExtrude","SWEPT_BODY",BODY,{"disambiguationData":[OSD([sQuery(id+"F5.wireOp",EDGE,"E5.0.3.0")])]}),"instanceName":"23"});
            var Q203;
            Q203=makeQuery(id+"F15.opPattern","COPY",BODY,{"derivedFrom":makeQuery(id+"F8.opExtrude","SWEPT_BODY",BODY,{"disambiguationData":[OSD([sQuery(id+"F5.wireOp",EDGE,"E5.0.2.0")])]}),"instanceName":"23"});
            var Q204;
            Q204=makeQuery(id+"F15.opPattern","COPY",BODY,{"derivedFrom":makeQuery(id+"F8.opExtrude","SWEPT_BODY",BODY,{"disambiguationData":[OSD([sQuery(id+"F5.wireOp",EDGE,"E5.0.1.0")])]}),"instanceName":"23"});
            var Q205;
            Q205=makeQuery(id+"F15.opPattern","COPY",BODY,{"derivedFrom":makeQuery(id+"F8.opExtrude","SWEPT_BODY",BODY,{"disambiguationData":[OSD([sQuery(id+"F5.wireOp",EDGE,"E4")])]}),"instanceName":"23"});
            var Q206;
            Q206=makeQuery(id+"F15.opPattern","COPY",BODY,{"derivedFrom":makeQuery(id+"F13.opExtrude","SWEPT_BODY",BODY,{"disambiguationData":[OSD([sQuery(id+"F11.wireOp",EDGE,"E11.0.3.0")])]}),"instanceName":"22"});
            var Q207;
            Q207=makeQuery(id+"F15.opPattern","COPY",BODY,{"derivedFrom":makeQuery(id+"F13.opExtrude","SWEPT_BODY",BODY,{"disambiguationData":[OSD([sQuery(id+"F11.wireOp",EDGE,"E11.0.2.0")])]}),"instanceName":"22"});
            var Q208;
            Q208=makeQuery(id+"F15.opPattern","COPY",BODY,{"derivedFrom":makeQuery(id+"F13.opExtrude","SWEPT_BODY",BODY,{"disambiguationData":[OSD([sQuery(id+"F11.wireOp",EDGE,"E11.0.1.0")])]}),"instanceName":"22"});
            var Q209;
            Q209=makeQuery(id+"F15.opPattern","COPY",BODY,{"derivedFrom":makeQuery(id+"F13.opExtrude","SWEPT_BODY",BODY,{"disambiguationData":[OSD([sQuery(id+"F11.wireOp",EDGE,"E10.0.3.0")])]}),"instanceName":"22"});
            var Q210;
            Q210=makeQuery(id+"F15.opPattern","COPY",BODY,{"derivedFrom":makeQuery(id+"F13.opExtrude","SWEPT_BODY",BODY,{"disambiguationData":[OSD([sQuery(id+"F11.wireOp",EDGE,"E10.0.2.0")])]}),"instanceName":"22"});
            var Q211;
            Q211=makeQuery(id+"F15.opPattern","COPY",BODY,{"derivedFrom":makeQuery(id+"F13.opExtrude","SWEPT_BODY",BODY,{"disambiguationData":[OSD([sQuery(id+"F11.wireOp",EDGE,"E10.0.1.0")])]}),"instanceName":"22"});
            var Q212;
            Q212=makeQuery(id+"F15.opPattern","COPY",BODY,{"derivedFrom":makeQuery(id+"F13.opExtrude","SWEPT_BODY",BODY,{"disambiguationData":[OSD([sQuery(id+"F11.wireOp",EDGE,"E9")])]}),"instanceName":"22"});
            var Q213;
            Q213=makeQuery(id+"F15.opPattern","COPY",BODY,{"derivedFrom":makeQuery(id+"F13.opExtrude","SWEPT_BODY",BODY,{"disambiguationData":[OSD([sQuery(id+"F11.wireOp",EDGE,"E8")])]}),"instanceName":"22"});
            var Q214;
            Q214=makeQuery(id+"F15.opPattern","COPY",BODY,{"derivedFrom":makeQuery(id+"F8.opExtrude","SWEPT_BODY",BODY,{"disambiguationData":[OSD([sQuery(id+"F5.wireOp",EDGE,"E6.0.4.0")])]}),"instanceName":"22"});
            var Q215;
            Q215=makeQuery(id+"F15.opPattern","COPY",BODY,{"derivedFrom":makeQuery(id+"F8.opExtrude","SWEPT_BODY",BODY,{"disambiguationData":[OSD([sQuery(id+"F5.wireOp",EDGE,"E6.0.3.0")])]}),"instanceName":"22"});
            var Q216;
            Q216=makeQuery(id+"F15.opPattern","COPY",BODY,{"derivedFrom":makeQuery(id+"F8.opExtrude","SWEPT_BODY",BODY,{"disambiguationData":[OSD([sQuery(id+"F5.wireOp",EDGE,"E6.0.2.0")])]}),"instanceName":"22"});
            var Q217;
            Q217=makeQuery(id+"F15.opPattern","COPY",BODY,{"derivedFrom":makeQuery(id+"F8.opExtrude","SWEPT_BODY",BODY,{"disambiguationData":[OSD([sQuery(id+"F5.wireOp",EDGE,"E6.0.1.0")])]}),"instanceName":"22"});
            var Q218;
            Q218=makeQuery(id+"F15.opPattern","COPY",BODY,{"derivedFrom":makeQuery(id+"F8.opExtrude","SWEPT_BODY",BODY,{"disambiguationData":[OSD([sQuery(id+"F5.wireOp",EDGE,"E5.0.4.0")])]}),"instanceName":"22"});
            var Q219;
            Q219=makeQuery(id+"F15.opPattern","COPY",BODY,{"derivedFrom":makeQuery(id+"F8.opExtrude","SWEPT_BODY",BODY,{"disambiguationData":[OSD([sQuery(id+"F5.wireOp",EDGE,"E5.0.3.0")])]}),"instanceName":"22"});
            var Q220;
            Q220=makeQuery(id+"F15.opPattern","COPY",BODY,{"derivedFrom":makeQuery(id+"F8.opExtrude","SWEPT_BODY",BODY,{"disambiguationData":[OSD([sQuery(id+"F5.wireOp",EDGE,"E5.0.2.0")])]}),"instanceName":"22"});
            var Q221;
            Q221=makeQuery(id+"F15.opPattern","COPY",BODY,{"derivedFrom":makeQuery(id+"F8.opExtrude","SWEPT_BODY",BODY,{"disambiguationData":[OSD([sQuery(id+"F5.wireOp",EDGE,"E5.0.1.0")])]}),"instanceName":"22"});
            var Q222;
            Q222=makeQuery(id+"F15.opPattern","COPY",BODY,{"derivedFrom":makeQuery(id+"F8.opExtrude","SWEPT_BODY",BODY,{"disambiguationData":[OSD([sQuery(id+"F5.wireOp",EDGE,"E4")])]}),"instanceName":"22"});
            var Q223;
            Q223=makeQuery(id+"F15.opPattern","COPY",BODY,{"derivedFrom":makeQuery(id+"F13.opExtrude","SWEPT_BODY",BODY,{"disambiguationData":[OSD([sQuery(id+"F11.wireOp",EDGE,"E11.0.3.0")])]}),"instanceName":"21"});
            var Q224;
            Q224=makeQuery(id+"F15.opPattern","COPY",BODY,{"derivedFrom":makeQuery(id+"F13.opExtrude","SWEPT_BODY",BODY,{"disambiguationData":[OSD([sQuery(id+"F11.wireOp",EDGE,"E11.0.2.0")])]}),"instanceName":"21"});
            var Q225;
            Q225=makeQuery(id+"F15.opPattern","COPY",BODY,{"derivedFrom":makeQuery(id+"F13.opExtrude","SWEPT_BODY",BODY,{"disambiguationData":[OSD([sQuery(id+"F11.wireOp",EDGE,"E11.0.1.0")])]}),"instanceName":"21"});
            var Q226;
            Q226=makeQuery(id+"F15.opPattern","COPY",BODY,{"derivedFrom":makeQuery(id+"F13.opExtrude","SWEPT_BODY",BODY,{"disambiguationData":[OSD([sQuery(id+"F11.wireOp",EDGE,"E10.0.3.0")])]}),"instanceName":"21"});
            var Q227;
            Q227=makeQuery(id+"F15.opPattern","COPY",BODY,{"derivedFrom":makeQuery(id+"F13.opExtrude","SWEPT_BODY",BODY,{"disambiguationData":[OSD([sQuery(id+"F11.wireOp",EDGE,"E10.0.2.0")])]}),"instanceName":"21"});
            var Q228;
            Q228=makeQuery(id+"F15.opPattern","COPY",BODY,{"derivedFrom":makeQuery(id+"F13.opExtrude","SWEPT_BODY",BODY,{"disambiguationData":[OSD([sQuery(id+"F11.wireOp",EDGE,"E10.0.1.0")])]}),"instanceName":"21"});
            var Q229;
            Q229=makeQuery(id+"F15.opPattern","COPY",BODY,{"derivedFrom":makeQuery(id+"F13.opExtrude","SWEPT_BODY",BODY,{"disambiguationData":[OSD([sQuery(id+"F11.wireOp",EDGE,"E9")])]}),"instanceName":"21"});
            var Q230;
            Q230=makeQuery(id+"F15.opPattern","COPY",BODY,{"derivedFrom":makeQuery(id+"F13.opExtrude","SWEPT_BODY",BODY,{"disambiguationData":[OSD([sQuery(id+"F11.wireOp",EDGE,"E8")])]}),"instanceName":"21"});
            var Q231;
            Q231=makeQuery(id+"F15.opPattern","COPY",BODY,{"derivedFrom":makeQuery(id+"F8.opExtrude","SWEPT_BODY",BODY,{"disambiguationData":[OSD([sQuery(id+"F5.wireOp",EDGE,"E6.0.4.0")])]}),"instanceName":"21"});
            var Q232;
            Q232=makeQuery(id+"F15.opPattern","COPY",BODY,{"derivedFrom":makeQuery(id+"F8.opExtrude","SWEPT_BODY",BODY,{"disambiguationData":[OSD([sQuery(id+"F5.wireOp",EDGE,"E6.0.3.0")])]}),"instanceName":"21"});
            var Q233;
            Q233=makeQuery(id+"F15.opPattern","COPY",BODY,{"derivedFrom":makeQuery(id+"F8.opExtrude","SWEPT_BODY",BODY,{"disambiguationData":[OSD([sQuery(id+"F5.wireOp",EDGE,"E6.0.2.0")])]}),"instanceName":"21"});
            var Q234;
            Q234=makeQuery(id+"F15.opPattern","COPY",BODY,{"derivedFrom":makeQuery(id+"F8.opExtrude","SWEPT_BODY",BODY,{"disambiguationData":[OSD([sQuery(id+"F5.wireOp",EDGE,"E6.0.1.0")])]}),"instanceName":"21"});
            var Q235;
            Q235=makeQuery(id+"F15.opPattern","COPY",BODY,{"derivedFrom":makeQuery(id+"F8.opExtrude","SWEPT_BODY",BODY,{"disambiguationData":[OSD([sQuery(id+"F5.wireOp",EDGE,"E5.0.4.0")])]}),"instanceName":"21"});
            var Q236;
            Q236=makeQuery(id+"F15.opPattern","COPY",BODY,{"derivedFrom":makeQuery(id+"F8.opExtrude","SWEPT_BODY",BODY,{"disambiguationData":[OSD([sQuery(id+"F5.wireOp",EDGE,"E5.0.3.0")])]}),"instanceName":"21"});
            var Q237;
            Q237=makeQuery(id+"F15.opPattern","COPY",BODY,{"derivedFrom":makeQuery(id+"F8.opExtrude","SWEPT_BODY",BODY,{"disambiguationData":[OSD([sQuery(id+"F5.wireOp",EDGE,"E5.0.2.0")])]}),"instanceName":"21"});
            var Q238;
            Q238=makeQuery(id+"F15.opPattern","COPY",BODY,{"derivedFrom":makeQuery(id+"F8.opExtrude","SWEPT_BODY",BODY,{"disambiguationData":[OSD([sQuery(id+"F5.wireOp",EDGE,"E5.0.1.0")])]}),"instanceName":"21"});
            var Q239;
            Q239=makeQuery(id+"F15.opPattern","COPY",BODY,{"derivedFrom":makeQuery(id+"F8.opExtrude","SWEPT_BODY",BODY,{"disambiguationData":[OSD([sQuery(id+"F5.wireOp",EDGE,"E4")])]}),"instanceName":"21"});
            var Q240;
            Q240=makeQuery(id+"F15.opPattern","COPY",BODY,{"derivedFrom":makeQuery(id+"F13.opExtrude","SWEPT_BODY",BODY,{"disambiguationData":[OSD([sQuery(id+"F11.wireOp",EDGE,"E11.0.3.0")])]}),"instanceName":"20"});
            var Q241;
            Q241=makeQuery(id+"F15.opPattern","COPY",BODY,{"derivedFrom":makeQuery(id+"F13.opExtrude","SWEPT_BODY",BODY,{"disambiguationData":[OSD([sQuery(id+"F11.wireOp",EDGE,"E11.0.2.0")])]}),"instanceName":"20"});
            var Q242;
            Q242=makeQuery(id+"F15.opPattern","COPY",BODY,{"derivedFrom":makeQuery(id+"F13.opExtrude","SWEPT_BODY",BODY,{"disambiguationData":[OSD([sQuery(id+"F11.wireOp",EDGE,"E11.0.1.0")])]}),"instanceName":"20"});
            var Q243;
            Q243=makeQuery(id+"F15.opPattern","COPY",BODY,{"derivedFrom":makeQuery(id+"F13.opExtrude","SWEPT_BODY",BODY,{"disambiguationData":[OSD([sQuery(id+"F11.wireOp",EDGE,"E10.0.3.0")])]}),"instanceName":"20"});
            var Q244;
            Q244=makeQuery(id+"F15.opPattern","COPY",BODY,{"derivedFrom":makeQuery(id+"F13.opExtrude","SWEPT_BODY",BODY,{"disambiguationData":[OSD([sQuery(id+"F11.wireOp",EDGE,"E10.0.2.0")])]}),"instanceName":"20"});
            var Q245;
            Q245=makeQuery(id+"F15.opPattern","COPY",BODY,{"derivedFrom":makeQuery(id+"F13.opExtrude","SWEPT_BODY",BODY,{"disambiguationData":[OSD([sQuery(id+"F11.wireOp",EDGE,"E10.0.1.0")])]}),"instanceName":"20"});
            var Q246;
            Q246=makeQuery(id+"F15.opPattern","COPY",BODY,{"derivedFrom":makeQuery(id+"F13.opExtrude","SWEPT_BODY",BODY,{"disambiguationData":[OSD([sQuery(id+"F11.wireOp",EDGE,"E9")])]}),"instanceName":"20"});
            var Q247;
            Q247=makeQuery(id+"F15.opPattern","COPY",BODY,{"derivedFrom":makeQuery(id+"F8.opExtrude","SWEPT_BODY",BODY,{"disambiguationData":[OSD([sQuery(id+"F5.wireOp",EDGE,"E6.0.4.0")])]}),"instanceName":"20"});
            var Q248;
            Q248=makeQuery(id+"F15.opPattern","COPY",BODY,{"derivedFrom":makeQuery(id+"F8.opExtrude","SWEPT_BODY",BODY,{"disambiguationData":[OSD([sQuery(id+"F5.wireOp",EDGE,"E6.0.3.0")])]}),"instanceName":"20"});
            var Q249;
            Q249=makeQuery(id+"F15.opPattern","COPY",BODY,{"derivedFrom":makeQuery(id+"F8.opExtrude","SWEPT_BODY",BODY,{"disambiguationData":[OSD([sQuery(id+"F5.wireOp",EDGE,"E6.0.2.0")])]}),"instanceName":"20"});
            var Q250;
            Q250=makeQuery(id+"F15.opPattern","COPY",BODY,{"derivedFrom":makeQuery(id+"F8.opExtrude","SWEPT_BODY",BODY,{"disambiguationData":[OSD([sQuery(id+"F5.wireOp",EDGE,"E6.0.1.0")])]}),"instanceName":"20"});
            var Q251;
            Q251=makeQuery(id+"F15.opPattern","COPY",BODY,{"derivedFrom":makeQuery(id+"F13.opExtrude","SWEPT_BODY",BODY,{"disambiguationData":[OSD([sQuery(id+"F11.wireOp",EDGE,"E8")])]}),"instanceName":"20"});
            var Q252;
            Q252=makeQuery(id+"F15.opPattern","COPY",BODY,{"derivedFrom":makeQuery(id+"F8.opExtrude","SWEPT_BODY",BODY,{"disambiguationData":[OSD([sQuery(id+"F5.wireOp",EDGE,"E5.0.4.0")])]}),"instanceName":"20"});
            var Q253;
            Q253=makeQuery(id+"F15.opPattern","COPY",BODY,{"derivedFrom":makeQuery(id+"F8.opExtrude","SWEPT_BODY",BODY,{"disambiguationData":[OSD([sQuery(id+"F5.wireOp",EDGE,"E5.0.3.0")])]}),"instanceName":"20"});
            var Q254;
            Q254=makeQuery(id+"F15.opPattern","COPY",BODY,{"derivedFrom":makeQuery(id+"F8.opExtrude","SWEPT_BODY",BODY,{"disambiguationData":[OSD([sQuery(id+"F5.wireOp",EDGE,"E5.0.2.0")])]}),"instanceName":"20"});
            var Q255;
            Q255=makeQuery(id+"F15.opPattern","COPY",BODY,{"derivedFrom":makeQuery(id+"F8.opExtrude","SWEPT_BODY",BODY,{"disambiguationData":[OSD([sQuery(id+"F5.wireOp",EDGE,"E5.0.1.0")])]}),"instanceName":"20"});
            var Q256;
            Q256=makeQuery(id+"F15.opPattern","COPY",BODY,{"derivedFrom":makeQuery(id+"F8.opExtrude","SWEPT_BODY",BODY,{"disambiguationData":[OSD([sQuery(id+"F5.wireOp",EDGE,"E4")])]}),"instanceName":"20"});
            var Q257;
            Q257=makeQuery(id+"F15.opPattern","COPY",BODY,{"derivedFrom":makeQuery(id+"F13.opExtrude","SWEPT_BODY",BODY,{"disambiguationData":[OSD([sQuery(id+"F11.wireOp",EDGE,"E11.0.3.0")])]}),"instanceName":"19"});
            var Q258;
            Q258=makeQuery(id+"F15.opPattern","COPY",BODY,{"derivedFrom":makeQuery(id+"F13.opExtrude","SWEPT_BODY",BODY,{"disambiguationData":[OSD([sQuery(id+"F11.wireOp",EDGE,"E11.0.2.0")])]}),"instanceName":"19"});
            var Q259;
            Q259=makeQuery(id+"F15.opPattern","COPY",BODY,{"derivedFrom":makeQuery(id+"F13.opExtrude","SWEPT_BODY",BODY,{"disambiguationData":[OSD([sQuery(id+"F11.wireOp",EDGE,"E11.0.1.0")])]}),"instanceName":"19"});
            var Q260;
            Q260=makeQuery(id+"F15.opPattern","COPY",BODY,{"derivedFrom":makeQuery(id+"F13.opExtrude","SWEPT_BODY",BODY,{"disambiguationData":[OSD([sQuery(id+"F11.wireOp",EDGE,"E10.0.3.0")])]}),"instanceName":"19"});
            var Q261;
            Q261=makeQuery(id+"F15.opPattern","COPY",BODY,{"derivedFrom":makeQuery(id+"F13.opExtrude","SWEPT_BODY",BODY,{"disambiguationData":[OSD([sQuery(id+"F11.wireOp",EDGE,"E10.0.2.0")])]}),"instanceName":"19"});
            var Q262;
            Q262=makeQuery(id+"F15.opPattern","COPY",BODY,{"derivedFrom":makeQuery(id+"F13.opExtrude","SWEPT_BODY",BODY,{"disambiguationData":[OSD([sQuery(id+"F11.wireOp",EDGE,"E10.0.1.0")])]}),"instanceName":"19"});
            var Q263;
            Q263=makeQuery(id+"F15.opPattern","COPY",BODY,{"derivedFrom":makeQuery(id+"F13.opExtrude","SWEPT_BODY",BODY,{"disambiguationData":[OSD([sQuery(id+"F11.wireOp",EDGE,"E9")])]}),"instanceName":"19"});
            var Q264;
            Q264=makeQuery(id+"F15.opPattern","COPY",BODY,{"derivedFrom":makeQuery(id+"F13.opExtrude","SWEPT_BODY",BODY,{"disambiguationData":[OSD([sQuery(id+"F11.wireOp",EDGE,"E8")])]}),"instanceName":"19"});
            var Q265;
            Q265=makeQuery(id+"F15.opPattern","COPY",BODY,{"derivedFrom":makeQuery(id+"F8.opExtrude","SWEPT_BODY",BODY,{"disambiguationData":[OSD([sQuery(id+"F5.wireOp",EDGE,"E6.0.4.0")])]}),"instanceName":"19"});
            var Q266;
            Q266=makeQuery(id+"F15.opPattern","COPY",BODY,{"derivedFrom":makeQuery(id+"F8.opExtrude","SWEPT_BODY",BODY,{"disambiguationData":[OSD([sQuery(id+"F5.wireOp",EDGE,"E6.0.3.0")])]}),"instanceName":"19"});
            var Q267;
            Q267=makeQuery(id+"F15.opPattern","COPY",BODY,{"derivedFrom":makeQuery(id+"F8.opExtrude","SWEPT_BODY",BODY,{"disambiguationData":[OSD([sQuery(id+"F5.wireOp",EDGE,"E6.0.2.0")])]}),"instanceName":"19"});
            var Q268;
            Q268=makeQuery(id+"F15.opPattern","COPY",BODY,{"derivedFrom":makeQuery(id+"F8.opExtrude","SWEPT_BODY",BODY,{"disambiguationData":[OSD([sQuery(id+"F5.wireOp",EDGE,"E6.0.1.0")])]}),"instanceName":"19"});
            var Q269;
            Q269=makeQuery(id+"F15.opPattern","COPY",BODY,{"derivedFrom":makeQuery(id+"F8.opExtrude","SWEPT_BODY",BODY,{"disambiguationData":[OSD([sQuery(id+"F5.wireOp",EDGE,"E5.0.3.0")])]}),"instanceName":"19"});
            var Q270;
            Q270=makeQuery(id+"F15.opPattern","COPY",BODY,{"derivedFrom":makeQuery(id+"F8.opExtrude","SWEPT_BODY",BODY,{"disambiguationData":[OSD([sQuery(id+"F5.wireOp",EDGE,"E5.0.2.0")])]}),"instanceName":"19"});
            var Q271;
            Q271=makeQuery(id+"F15.opPattern","COPY",BODY,{"derivedFrom":makeQuery(id+"F8.opExtrude","SWEPT_BODY",BODY,{"disambiguationData":[OSD([sQuery(id+"F5.wireOp",EDGE,"E5.0.1.0")])]}),"instanceName":"19"});
            var Q272;
            Q272=makeQuery(id+"F15.opPattern","COPY",BODY,{"derivedFrom":makeQuery(id+"F8.opExtrude","SWEPT_BODY",BODY,{"disambiguationData":[OSD([sQuery(id+"F5.wireOp",EDGE,"E4")])]}),"instanceName":"19"});
            var Q273;
            Q273=makeQuery(id+"F15.opPattern","COPY",BODY,{"derivedFrom":makeQuery(id+"F13.opExtrude","SWEPT_BODY",BODY,{"disambiguationData":[OSD([sQuery(id+"F11.wireOp",EDGE,"E11.0.3.0")])]}),"instanceName":"18"});
            var Q274;
            Q274=makeQuery(id+"F15.opPattern","COPY",BODY,{"derivedFrom":makeQuery(id+"F13.opExtrude","SWEPT_BODY",BODY,{"disambiguationData":[OSD([sQuery(id+"F11.wireOp",EDGE,"E11.0.2.0")])]}),"instanceName":"18"});
            var Q275;
            Q275=makeQuery(id+"F15.opPattern","COPY",BODY,{"derivedFrom":makeQuery(id+"F13.opExtrude","SWEPT_BODY",BODY,{"disambiguationData":[OSD([sQuery(id+"F11.wireOp",EDGE,"E11.0.1.0")])]}),"instanceName":"18"});
            var Q276;
            Q276=makeQuery(id+"F15.opPattern","COPY",BODY,{"derivedFrom":makeQuery(id+"F13.opExtrude","SWEPT_BODY",BODY,{"disambiguationData":[OSD([sQuery(id+"F11.wireOp",EDGE,"E10.0.3.0")])]}),"instanceName":"18"});
            var Q277;
            Q277=makeQuery(id+"F15.opPattern","COPY",BODY,{"derivedFrom":makeQuery(id+"F13.opExtrude","SWEPT_BODY",BODY,{"disambiguationData":[OSD([sQuery(id+"F11.wireOp",EDGE,"E10.0.2.0")])]}),"instanceName":"18"});
            var Q278;
            Q278=makeQuery(id+"F15.opPattern","COPY",BODY,{"derivedFrom":makeQuery(id+"F8.opExtrude","SWEPT_BODY",BODY,{"disambiguationData":[OSD([sQuery(id+"F5.wireOp",EDGE,"E5.0.4.0")])]}),"instanceName":"19"});
            var Q279;
            Q279=makeQuery(id+"F15.opPattern","COPY",BODY,{"derivedFrom":makeQuery(id+"F13.opExtrude","SWEPT_BODY",BODY,{"disambiguationData":[OSD([sQuery(id+"F11.wireOp",EDGE,"E10.0.1.0")])]}),"instanceName":"18"});
            var Q280;
            Q280=makeQuery(id+"F15.opPattern","COPY",BODY,{"derivedFrom":makeQuery(id+"F13.opExtrude","SWEPT_BODY",BODY,{"disambiguationData":[OSD([sQuery(id+"F11.wireOp",EDGE,"E9")])]}),"instanceName":"18"});
            var Q281;
            Q281=makeQuery(id+"F15.opPattern","COPY",BODY,{"derivedFrom":makeQuery(id+"F13.opExtrude","SWEPT_BODY",BODY,{"disambiguationData":[OSD([sQuery(id+"F11.wireOp",EDGE,"E8")])]}),"instanceName":"18"});
            var Q282;
            Q282=makeQuery(id+"F15.opPattern","COPY",BODY,{"derivedFrom":makeQuery(id+"F8.opExtrude","SWEPT_BODY",BODY,{"disambiguationData":[OSD([sQuery(id+"F5.wireOp",EDGE,"E6.0.4.0")])]}),"instanceName":"18"});
            var Q283;
            Q283=makeQuery(id+"F15.opPattern","COPY",BODY,{"derivedFrom":makeQuery(id+"F8.opExtrude","SWEPT_BODY",BODY,{"disambiguationData":[OSD([sQuery(id+"F5.wireOp",EDGE,"E6.0.3.0")])]}),"instanceName":"18"});
            var Q284;
            Q284=makeQuery(id+"F15.opPattern","COPY",BODY,{"derivedFrom":makeQuery(id+"F8.opExtrude","SWEPT_BODY",BODY,{"disambiguationData":[OSD([sQuery(id+"F5.wireOp",EDGE,"E6.0.2.0")])]}),"instanceName":"18"});
            var Q285;
            Q285=makeQuery(id+"F15.opPattern","COPY",BODY,{"derivedFrom":makeQuery(id+"F8.opExtrude","SWEPT_BODY",BODY,{"disambiguationData":[OSD([sQuery(id+"F5.wireOp",EDGE,"E6.0.1.0")])]}),"instanceName":"18"});
            var Q286;
            Q286=makeQuery(id+"F15.opPattern","COPY",BODY,{"derivedFrom":makeQuery(id+"F13.opExtrude","SWEPT_BODY",BODY,{"disambiguationData":[OSD([sQuery(id+"F11.wireOp",EDGE,"E8")])]}),"instanceName":"17"});
            var Q287;
            Q287=makeQuery(id+"F15.opPattern","COPY",BODY,{"derivedFrom":makeQuery(id+"F13.opExtrude","SWEPT_BODY",BODY,{"disambiguationData":[OSD([sQuery(id+"F11.wireOp",EDGE,"E9")])]}),"instanceName":"17"});
            var Q288;
            Q288=makeQuery(id+"F15.opPattern","COPY",BODY,{"derivedFrom":makeQuery(id+"F13.opExtrude","SWEPT_BODY",BODY,{"disambiguationData":[OSD([sQuery(id+"F11.wireOp",EDGE,"E10.0.1.0")])]}),"instanceName":"17"});
            var Q289;
            Q289=makeQuery(id+"F15.opPattern","COPY",BODY,{"derivedFrom":makeQuery(id+"F13.opExtrude","SWEPT_BODY",BODY,{"disambiguationData":[OSD([sQuery(id+"F11.wireOp",EDGE,"E10.0.2.0")])]}),"instanceName":"17"});
            var Q290;
            Q290=makeQuery(id+"F15.opPattern","COPY",BODY,{"derivedFrom":makeQuery(id+"F13.opExtrude","SWEPT_BODY",BODY,{"disambiguationData":[OSD([sQuery(id+"F11.wireOp",EDGE,"E10.0.3.0")])]}),"instanceName":"17"});
            var Q291;
            Q291=makeQuery(id+"F15.opPattern","COPY",BODY,{"derivedFrom":makeQuery(id+"F13.opExtrude","SWEPT_BODY",BODY,{"disambiguationData":[OSD([sQuery(id+"F11.wireOp",EDGE,"E11.0.1.0")])]}),"instanceName":"17"});
            var Q292;
            Q292=makeQuery(id+"F15.opPattern","COPY",BODY,{"derivedFrom":makeQuery(id+"F13.opExtrude","SWEPT_BODY",BODY,{"disambiguationData":[OSD([sQuery(id+"F11.wireOp",EDGE,"E11.0.2.0")])]}),"instanceName":"17"});
            var Q293;
            Q293=makeQuery(id+"F15.opPattern","COPY",BODY,{"derivedFrom":makeQuery(id+"F13.opExtrude","SWEPT_BODY",BODY,{"disambiguationData":[OSD([sQuery(id+"F11.wireOp",EDGE,"E11.0.3.0")])]}),"instanceName":"17"});
            var Q294;
            Q294=makeQuery(id+"F15.opPattern","COPY",BODY,{"derivedFrom":makeQuery(id+"F8.opExtrude","SWEPT_BODY",BODY,{"disambiguationData":[OSD([sQuery(id+"F5.wireOp",EDGE,"E4")])]}),"instanceName":"18"});
            var Q295;
            Q295=makeQuery(id+"F15.opPattern","COPY",BODY,{"derivedFrom":makeQuery(id+"F8.opExtrude","SWEPT_BODY",BODY,{"disambiguationData":[OSD([sQuery(id+"F5.wireOp",EDGE,"E5.0.1.0")])]}),"instanceName":"18"});
            var Q296;
            Q296=makeQuery(id+"F15.opPattern","COPY",BODY,{"derivedFrom":makeQuery(id+"F8.opExtrude","SWEPT_BODY",BODY,{"disambiguationData":[OSD([sQuery(id+"F5.wireOp",EDGE,"E5.0.2.0")])]}),"instanceName":"18"});
            var Q297;
            Q297=makeQuery(id+"F15.opPattern","COPY",BODY,{"derivedFrom":makeQuery(id+"F8.opExtrude","SWEPT_BODY",BODY,{"disambiguationData":[OSD([sQuery(id+"F5.wireOp",EDGE,"E5.0.3.0")])]}),"instanceName":"18"});
            var Q298;
            Q298=makeQuery(id+"F15.opPattern","COPY",BODY,{"derivedFrom":makeQuery(id+"F8.opExtrude","SWEPT_BODY",BODY,{"disambiguationData":[OSD([sQuery(id+"F5.wireOp",EDGE,"E5.0.4.0")])]}),"instanceName":"18"});
            var Q299;
            Q299=makeQuery(id+"F15.opPattern","COPY",BODY,{"derivedFrom":makeQuery(id+"F13.opExtrude","SWEPT_BODY",BODY,{"disambiguationData":[OSD([sQuery(id+"F11.wireOp",EDGE,"E11.0.3.0")])]}),"instanceName":"16"});
            var Q300;
            Q300=makeQuery(id+"F15.opPattern","COPY",BODY,{"derivedFrom":makeQuery(id+"F13.opExtrude","SWEPT_BODY",BODY,{"disambiguationData":[OSD([sQuery(id+"F11.wireOp",EDGE,"E11.0.2.0")])]}),"instanceName":"16"});
            var Q301;
            Q301=makeQuery(id+"F15.opPattern","COPY",BODY,{"derivedFrom":makeQuery(id+"F13.opExtrude","SWEPT_BODY",BODY,{"disambiguationData":[OSD([sQuery(id+"F11.wireOp",EDGE,"E11.0.1.0")])]}),"instanceName":"16"});
            var Q302;
            Q302=makeQuery(id+"F15.opPattern","COPY",BODY,{"derivedFrom":makeQuery(id+"F13.opExtrude","SWEPT_BODY",BODY,{"disambiguationData":[OSD([sQuery(id+"F11.wireOp",EDGE,"E10.0.3.0")])]}),"instanceName":"16"});
            var Q303;
            Q303=makeQuery(id+"F15.opPattern","COPY",BODY,{"derivedFrom":makeQuery(id+"F13.opExtrude","SWEPT_BODY",BODY,{"disambiguationData":[OSD([sQuery(id+"F11.wireOp",EDGE,"E10.0.2.0")])]}),"instanceName":"16"});
            var Q304;
            Q304=makeQuery(id+"F15.opPattern","COPY",BODY,{"derivedFrom":makeQuery(id+"F13.opExtrude","SWEPT_BODY",BODY,{"disambiguationData":[OSD([sQuery(id+"F11.wireOp",EDGE,"E10.0.1.0")])]}),"instanceName":"16"});
            var Q305;
            Q305=makeQuery(id+"F15.opPattern","COPY",BODY,{"derivedFrom":makeQuery(id+"F13.opExtrude","SWEPT_BODY",BODY,{"disambiguationData":[OSD([sQuery(id+"F11.wireOp",EDGE,"E9")])]}),"instanceName":"16"});
            var Q306;
            Q306=makeQuery(id+"F15.opPattern","COPY",BODY,{"derivedFrom":makeQuery(id+"F13.opExtrude","SWEPT_BODY",BODY,{"disambiguationData":[OSD([sQuery(id+"F11.wireOp",EDGE,"E8")])]}),"instanceName":"16"});
            var Q307;
            Q307=makeQuery(id+"F15.opPattern","COPY",BODY,{"derivedFrom":makeQuery(id+"F8.opExtrude","SWEPT_BODY",BODY,{"disambiguationData":[OSD([sQuery(id+"F5.wireOp",EDGE,"E6.0.4.0")])]}),"instanceName":"16"});
            var Q308;
            Q308=makeQuery(id+"F15.opPattern","COPY",BODY,{"derivedFrom":makeQuery(id+"F8.opExtrude","SWEPT_BODY",BODY,{"disambiguationData":[OSD([sQuery(id+"F5.wireOp",EDGE,"E6.0.3.0")])]}),"instanceName":"16"});
            var Q309;
            Q309=makeQuery(id+"F15.opPattern","COPY",BODY,{"derivedFrom":makeQuery(id+"F8.opExtrude","SWEPT_BODY",BODY,{"disambiguationData":[OSD([sQuery(id+"F5.wireOp",EDGE,"E6.0.2.0")])]}),"instanceName":"16"});
            var Q310;
            Q310=makeQuery(id+"F15.opPattern","COPY",BODY,{"derivedFrom":makeQuery(id+"F8.opExtrude","SWEPT_BODY",BODY,{"disambiguationData":[OSD([sQuery(id+"F5.wireOp",EDGE,"E6.0.1.0")])]}),"instanceName":"16"});
            var Q311;
            Q311=makeQuery(id+"F15.opPattern","COPY",BODY,{"derivedFrom":makeQuery(id+"F8.opExtrude","SWEPT_BODY",BODY,{"disambiguationData":[OSD([sQuery(id+"F5.wireOp",EDGE,"E5.0.4.0")])]}),"instanceName":"16"});
            var Q312;
            Q312=makeQuery(id+"F15.opPattern","COPY",BODY,{"derivedFrom":makeQuery(id+"F8.opExtrude","SWEPT_BODY",BODY,{"disambiguationData":[OSD([sQuery(id+"F5.wireOp",EDGE,"E5.0.3.0")])]}),"instanceName":"16"});
            var Q313;
            Q313=makeQuery(id+"F15.opPattern","COPY",BODY,{"derivedFrom":makeQuery(id+"F8.opExtrude","SWEPT_BODY",BODY,{"disambiguationData":[OSD([sQuery(id+"F5.wireOp",EDGE,"E5.0.2.0")])]}),"instanceName":"16"});
            var Q314;
            Q314=makeQuery(id+"F15.opPattern","COPY",BODY,{"derivedFrom":makeQuery(id+"F8.opExtrude","SWEPT_BODY",BODY,{"disambiguationData":[OSD([sQuery(id+"F5.wireOp",EDGE,"E5.0.1.0")])]}),"instanceName":"16"});
            var Q315;
            Q315=makeQuery(id+"F15.opPattern","COPY",BODY,{"derivedFrom":makeQuery(id+"F8.opExtrude","SWEPT_BODY",BODY,{"disambiguationData":[OSD([sQuery(id+"F5.wireOp",EDGE,"E4")])]}),"instanceName":"16"});
            var Q316;
            Q316=makeQuery(id+"F15.opPattern","COPY",BODY,{"derivedFrom":makeQuery(id+"F13.opExtrude","SWEPT_BODY",BODY,{"disambiguationData":[OSD([sQuery(id+"F11.wireOp",EDGE,"E11.0.3.0")])]}),"instanceName":"15"});
            var Q317;
            Q317=makeQuery(id+"F15.opPattern","COPY",BODY,{"derivedFrom":makeQuery(id+"F13.opExtrude","SWEPT_BODY",BODY,{"disambiguationData":[OSD([sQuery(id+"F11.wireOp",EDGE,"E11.0.2.0")])]}),"instanceName":"15"});
            var Q318;
            Q318=makeQuery(id+"F15.opPattern","COPY",BODY,{"derivedFrom":makeQuery(id+"F13.opExtrude","SWEPT_BODY",BODY,{"disambiguationData":[OSD([sQuery(id+"F11.wireOp",EDGE,"E11.0.1.0")])]}),"instanceName":"15"});
            var Q319;
            Q319=makeQuery(id+"F15.opPattern","COPY",BODY,{"derivedFrom":makeQuery(id+"F13.opExtrude","SWEPT_BODY",BODY,{"disambiguationData":[OSD([sQuery(id+"F11.wireOp",EDGE,"E10.0.3.0")])]}),"instanceName":"15"});
            var Q320;
            Q320=makeQuery(id+"F15.opPattern","COPY",BODY,{"derivedFrom":makeQuery(id+"F13.opExtrude","SWEPT_BODY",BODY,{"disambiguationData":[OSD([sQuery(id+"F11.wireOp",EDGE,"E10.0.2.0")])]}),"instanceName":"15"});
            var Q321;
            Q321=makeQuery(id+"F15.opPattern","COPY",BODY,{"derivedFrom":makeQuery(id+"F13.opExtrude","SWEPT_BODY",BODY,{"disambiguationData":[OSD([sQuery(id+"F11.wireOp",EDGE,"E10.0.1.0")])]}),"instanceName":"15"});
            var Q322;
            Q322=makeQuery(id+"F15.opPattern","COPY",BODY,{"derivedFrom":makeQuery(id+"F13.opExtrude","SWEPT_BODY",BODY,{"disambiguationData":[OSD([sQuery(id+"F11.wireOp",EDGE,"E9")])]}),"instanceName":"15"});
            var Q323;
            Q323=makeQuery(id+"F15.opPattern","COPY",BODY,{"derivedFrom":makeQuery(id+"F13.opExtrude","SWEPT_BODY",BODY,{"disambiguationData":[OSD([sQuery(id+"F11.wireOp",EDGE,"E8")])]}),"instanceName":"15"});
            var Q324;
            Q324=makeQuery(id+"F15.opPattern","COPY",BODY,{"derivedFrom":makeQuery(id+"F8.opExtrude","SWEPT_BODY",BODY,{"disambiguationData":[OSD([sQuery(id+"F5.wireOp",EDGE,"E6.0.4.0")])]}),"instanceName":"15"});
            var Q325;
            Q325=makeQuery(id+"F15.opPattern","COPY",BODY,{"derivedFrom":makeQuery(id+"F8.opExtrude","SWEPT_BODY",BODY,{"disambiguationData":[OSD([sQuery(id+"F5.wireOp",EDGE,"E6.0.3.0")])]}),"instanceName":"15"});
            var Q326;
            Q326=makeQuery(id+"F15.opPattern","COPY",BODY,{"derivedFrom":makeQuery(id+"F8.opExtrude","SWEPT_BODY",BODY,{"disambiguationData":[OSD([sQuery(id+"F5.wireOp",EDGE,"E6.0.2.0")])]}),"instanceName":"15"});
            var Q327;
            Q327=makeQuery(id+"F15.opPattern","COPY",BODY,{"derivedFrom":makeQuery(id+"F8.opExtrude","SWEPT_BODY",BODY,{"disambiguationData":[OSD([sQuery(id+"F5.wireOp",EDGE,"E6.0.1.0")])]}),"instanceName":"15"});
            var Q328;
            Q328=makeQuery(id+"F15.opPattern","COPY",BODY,{"derivedFrom":makeQuery(id+"F8.opExtrude","SWEPT_BODY",BODY,{"disambiguationData":[OSD([sQuery(id+"F5.wireOp",EDGE,"E5.0.4.0")])]}),"instanceName":"15"});
            var Q329;
            Q329=makeQuery(id+"F15.opPattern","COPY",BODY,{"derivedFrom":makeQuery(id+"F8.opExtrude","SWEPT_BODY",BODY,{"disambiguationData":[OSD([sQuery(id+"F5.wireOp",EDGE,"E5.0.3.0")])]}),"instanceName":"15"});
            var Q330;
            Q330=makeQuery(id+"F15.opPattern","COPY",BODY,{"derivedFrom":makeQuery(id+"F8.opExtrude","SWEPT_BODY",BODY,{"disambiguationData":[OSD([sQuery(id+"F5.wireOp",EDGE,"E5.0.2.0")])]}),"instanceName":"15"});
            var Q331;
            Q331=makeQuery(id+"F15.opPattern","COPY",BODY,{"derivedFrom":makeQuery(id+"F8.opExtrude","SWEPT_BODY",BODY,{"disambiguationData":[OSD([sQuery(id+"F5.wireOp",EDGE,"E5.0.1.0")])]}),"instanceName":"15"});
            var Q332;
            Q332=makeQuery(id+"F15.opPattern","COPY",BODY,{"derivedFrom":makeQuery(id+"F8.opExtrude","SWEPT_BODY",BODY,{"disambiguationData":[OSD([sQuery(id+"F5.wireOp",EDGE,"E4")])]}),"instanceName":"15"});
            var Q333;
            Q333=makeQuery(id+"F15.opPattern","COPY",BODY,{"derivedFrom":makeQuery(id+"F13.opExtrude","SWEPT_BODY",BODY,{"disambiguationData":[OSD([sQuery(id+"F11.wireOp",EDGE,"E11.0.3.0")])]}),"instanceName":"14"});
            var Q334;
            Q334=makeQuery(id+"F15.opPattern","COPY",BODY,{"derivedFrom":makeQuery(id+"F13.opExtrude","SWEPT_BODY",BODY,{"disambiguationData":[OSD([sQuery(id+"F11.wireOp",EDGE,"E11.0.2.0")])]}),"instanceName":"14"});
            var Q335;
            Q335=makeQuery(id+"F15.opPattern","COPY",BODY,{"derivedFrom":makeQuery(id+"F13.opExtrude","SWEPT_BODY",BODY,{"disambiguationData":[OSD([sQuery(id+"F11.wireOp",EDGE,"E11.0.1.0")])]}),"instanceName":"14"});
            var Q336;
            Q336=makeQuery(id+"F15.opPattern","COPY",BODY,{"derivedFrom":makeQuery(id+"F13.opExtrude","SWEPT_BODY",BODY,{"disambiguationData":[OSD([sQuery(id+"F11.wireOp",EDGE,"E10.0.3.0")])]}),"instanceName":"14"});
            var Q337;
            Q337=makeQuery(id+"F15.opPattern","COPY",BODY,{"derivedFrom":makeQuery(id+"F13.opExtrude","SWEPT_BODY",BODY,{"disambiguationData":[OSD([sQuery(id+"F11.wireOp",EDGE,"E10.0.2.0")])]}),"instanceName":"14"});
            var Q338;
            Q338=makeQuery(id+"F15.opPattern","COPY",BODY,{"derivedFrom":makeQuery(id+"F13.opExtrude","SWEPT_BODY",BODY,{"disambiguationData":[OSD([sQuery(id+"F11.wireOp",EDGE,"E10.0.1.0")])]}),"instanceName":"14"});
            var Q339;
            Q339=makeQuery(id+"F15.opPattern","COPY",BODY,{"derivedFrom":makeQuery(id+"F13.opExtrude","SWEPT_BODY",BODY,{"disambiguationData":[OSD([sQuery(id+"F11.wireOp",EDGE,"E9")])]}),"instanceName":"14"});
            var Q340;
            Q340=makeQuery(id+"F15.opPattern","COPY",BODY,{"derivedFrom":makeQuery(id+"F13.opExtrude","SWEPT_BODY",BODY,{"disambiguationData":[OSD([sQuery(id+"F11.wireOp",EDGE,"E8")])]}),"instanceName":"14"});
            var Q341;
            Q341=makeQuery(id+"F15.opPattern","COPY",BODY,{"derivedFrom":makeQuery(id+"F8.opExtrude","SWEPT_BODY",BODY,{"disambiguationData":[OSD([sQuery(id+"F5.wireOp",EDGE,"E6.0.4.0")])]}),"instanceName":"14"});
            var Q342;
            Q342=makeQuery(id+"F15.opPattern","COPY",BODY,{"derivedFrom":makeQuery(id+"F8.opExtrude","SWEPT_BODY",BODY,{"disambiguationData":[OSD([sQuery(id+"F5.wireOp",EDGE,"E6.0.3.0")])]}),"instanceName":"14"});
            var Q343;
            Q343=makeQuery(id+"F15.opPattern","COPY",BODY,{"derivedFrom":makeQuery(id+"F8.opExtrude","SWEPT_BODY",BODY,{"disambiguationData":[OSD([sQuery(id+"F5.wireOp",EDGE,"E6.0.2.0")])]}),"instanceName":"14"});
            var Q344;
            Q344=makeQuery(id+"F15.opPattern","COPY",BODY,{"derivedFrom":makeQuery(id+"F8.opExtrude","SWEPT_BODY",BODY,{"disambiguationData":[OSD([sQuery(id+"F5.wireOp",EDGE,"E6.0.1.0")])]}),"instanceName":"14"});
            var Q345;
            Q345=makeQuery(id+"F15.opPattern","COPY",BODY,{"derivedFrom":makeQuery(id+"F8.opExtrude","SWEPT_BODY",BODY,{"disambiguationData":[OSD([sQuery(id+"F5.wireOp",EDGE,"E5.0.4.0")])]}),"instanceName":"14"});
            var Q346;
            Q346=makeQuery(id+"F15.opPattern","COPY",BODY,{"derivedFrom":makeQuery(id+"F8.opExtrude","SWEPT_BODY",BODY,{"disambiguationData":[OSD([sQuery(id+"F5.wireOp",EDGE,"E5.0.3.0")])]}),"instanceName":"14"});
            var Q347;
            Q347=makeQuery(id+"F15.opPattern","COPY",BODY,{"derivedFrom":makeQuery(id+"F8.opExtrude","SWEPT_BODY",BODY,{"disambiguationData":[OSD([sQuery(id+"F5.wireOp",EDGE,"E5.0.2.0")])]}),"instanceName":"14"});
            var Q348;
            Q348=makeQuery(id+"F15.opPattern","COPY",BODY,{"derivedFrom":makeQuery(id+"F8.opExtrude","SWEPT_BODY",BODY,{"disambiguationData":[OSD([sQuery(id+"F5.wireOp",EDGE,"E5.0.1.0")])]}),"instanceName":"14"});
            var Q349;
            Q349=makeQuery(id+"F15.opPattern","COPY",BODY,{"derivedFrom":makeQuery(id+"F8.opExtrude","SWEPT_BODY",BODY,{"disambiguationData":[OSD([sQuery(id+"F5.wireOp",EDGE,"E4")])]}),"instanceName":"14"});
            var Q350;
            Q350=makeQuery(id+"F15.opPattern","COPY",BODY,{"derivedFrom":makeQuery(id+"F13.opExtrude","SWEPT_BODY",BODY,{"disambiguationData":[OSD([sQuery(id+"F11.wireOp",EDGE,"E11.0.3.0")])]}),"instanceName":"13"});
            var Q351;
            Q351=makeQuery(id+"F15.opPattern","COPY",BODY,{"derivedFrom":makeQuery(id+"F13.opExtrude","SWEPT_BODY",BODY,{"disambiguationData":[OSD([sQuery(id+"F11.wireOp",EDGE,"E11.0.2.0")])]}),"instanceName":"13"});
            var Q352;
            Q352=makeQuery(id+"F15.opPattern","COPY",BODY,{"derivedFrom":makeQuery(id+"F13.opExtrude","SWEPT_BODY",BODY,{"disambiguationData":[OSD([sQuery(id+"F11.wireOp",EDGE,"E11.0.1.0")])]}),"instanceName":"13"});
            var Q353;
            Q353=makeQuery(id+"F15.opPattern","COPY",BODY,{"derivedFrom":makeQuery(id+"F13.opExtrude","SWEPT_BODY",BODY,{"disambiguationData":[OSD([sQuery(id+"F11.wireOp",EDGE,"E10.0.3.0")])]}),"instanceName":"13"});
            var Q354;
            Q354=makeQuery(id+"F15.opPattern","COPY",BODY,{"derivedFrom":makeQuery(id+"F13.opExtrude","SWEPT_BODY",BODY,{"disambiguationData":[OSD([sQuery(id+"F11.wireOp",EDGE,"E10.0.2.0")])]}),"instanceName":"13"});
            var Q355;
            Q355=makeQuery(id+"F15.opPattern","COPY",BODY,{"derivedFrom":makeQuery(id+"F13.opExtrude","SWEPT_BODY",BODY,{"disambiguationData":[OSD([sQuery(id+"F11.wireOp",EDGE,"E10.0.1.0")])]}),"instanceName":"13"});
            var Q356;
            Q356=makeQuery(id+"F15.opPattern","COPY",BODY,{"derivedFrom":makeQuery(id+"F13.opExtrude","SWEPT_BODY",BODY,{"disambiguationData":[OSD([sQuery(id+"F11.wireOp",EDGE,"E9")])]}),"instanceName":"13"});
            var Q357;
            Q357=makeQuery(id+"F15.opPattern","COPY",BODY,{"derivedFrom":makeQuery(id+"F13.opExtrude","SWEPT_BODY",BODY,{"disambiguationData":[OSD([sQuery(id+"F11.wireOp",EDGE,"E8")])]}),"instanceName":"13"});
            var Q358;
            Q358=makeQuery(id+"F15.opPattern","COPY",BODY,{"derivedFrom":makeQuery(id+"F8.opExtrude","SWEPT_BODY",BODY,{"disambiguationData":[OSD([sQuery(id+"F5.wireOp",EDGE,"E6.0.4.0")])]}),"instanceName":"13"});
            var Q359;
            Q359=makeQuery(id+"F15.opPattern","COPY",BODY,{"derivedFrom":makeQuery(id+"F8.opExtrude","SWEPT_BODY",BODY,{"disambiguationData":[OSD([sQuery(id+"F5.wireOp",EDGE,"E6.0.3.0")])]}),"instanceName":"13"});
            var Q360;
            Q360=makeQuery(id+"F15.opPattern","COPY",BODY,{"derivedFrom":makeQuery(id+"F8.opExtrude","SWEPT_BODY",BODY,{"disambiguationData":[OSD([sQuery(id+"F5.wireOp",EDGE,"E6.0.2.0")])]}),"instanceName":"13"});
            var Q361;
            Q361=makeQuery(id+"F15.opPattern","COPY",BODY,{"derivedFrom":makeQuery(id+"F8.opExtrude","SWEPT_BODY",BODY,{"disambiguationData":[OSD([sQuery(id+"F5.wireOp",EDGE,"E6.0.1.0")])]}),"instanceName":"13"});
            var Q362;
            Q362=makeQuery(id+"F15.opPattern","COPY",BODY,{"derivedFrom":makeQuery(id+"F13.opExtrude","SWEPT_BODY",BODY,{"disambiguationData":[OSD([sQuery(id+"F11.wireOp",EDGE,"E10.0.3.0")])]}),"instanceName":"9"});
            var Q363;
            Q363=makeQuery(id+"F15.opPattern","COPY",BODY,{"derivedFrom":makeQuery(id+"F13.opExtrude","SWEPT_BODY",BODY,{"disambiguationData":[OSD([sQuery(id+"F11.wireOp",EDGE,"E10.0.2.0")])]}),"instanceName":"9"});
            var Q364;
            Q364=makeQuery(id+"F15.opPattern","COPY",BODY,{"derivedFrom":makeQuery(id+"F13.opExtrude","SWEPT_BODY",BODY,{"disambiguationData":[OSD([sQuery(id+"F11.wireOp",EDGE,"E10.0.1.0")])]}),"instanceName":"9"});
            var Q365;
            Q365=makeQuery(id+"F15.opPattern","COPY",BODY,{"derivedFrom":makeQuery(id+"F13.opExtrude","SWEPT_BODY",BODY,{"disambiguationData":[OSD([sQuery(id+"F11.wireOp",EDGE,"E8")])]}),"instanceName":"9"});
            var Q366;
            Q366=makeQuery(id+"F15.opPattern","COPY",BODY,{"derivedFrom":makeQuery(id+"F13.opExtrude","SWEPT_BODY",BODY,{"disambiguationData":[OSD([sQuery(id+"F11.wireOp",EDGE,"E9")])]}),"instanceName":"9"});
            var Q367;
            Q367=makeQuery(id+"F15.opPattern","COPY",BODY,{"derivedFrom":makeQuery(id+"F13.opExtrude","SWEPT_BODY",BODY,{"disambiguationData":[OSD([sQuery(id+"F11.wireOp",EDGE,"E11.0.1.0")])]}),"instanceName":"9"});
            var Q368;
            Q368=makeQuery(id+"F15.opPattern","COPY",BODY,{"derivedFrom":makeQuery(id+"F13.opExtrude","SWEPT_BODY",BODY,{"disambiguationData":[OSD([sQuery(id+"F11.wireOp",EDGE,"E11.0.2.0")])]}),"instanceName":"9"});
            var Q369;
            Q369=makeQuery(id+"F15.opPattern","COPY",BODY,{"derivedFrom":makeQuery(id+"F13.opExtrude","SWEPT_BODY",BODY,{"disambiguationData":[OSD([sQuery(id+"F11.wireOp",EDGE,"E11.0.3.0")])]}),"instanceName":"9"});
            var Q370;
            Q370=makeQuery(id+"F15.opPattern","COPY",BODY,{"derivedFrom":makeQuery(id+"F13.opExtrude","SWEPT_BODY",BODY,{"disambiguationData":[OSD([sQuery(id+"F11.wireOp",EDGE,"E10.0.3.0")])]}),"instanceName":"8"});
            var Q371;
            Q371=makeQuery(id+"F15.opPattern","COPY",BODY,{"derivedFrom":makeQuery(id+"F13.opExtrude","SWEPT_BODY",BODY,{"disambiguationData":[OSD([sQuery(id+"F11.wireOp",EDGE,"E10.0.2.0")])]}),"instanceName":"8"});
            var Q372;
            Q372=makeQuery(id+"F15.opPattern","COPY",BODY,{"derivedFrom":makeQuery(id+"F13.opExtrude","SWEPT_BODY",BODY,{"disambiguationData":[OSD([sQuery(id+"F11.wireOp",EDGE,"E10.0.1.0")])]}),"instanceName":"8"});
            var Q373;
            Q373=makeQuery(id+"F15.opPattern","COPY",BODY,{"derivedFrom":makeQuery(id+"F13.opExtrude","SWEPT_BODY",BODY,{"disambiguationData":[OSD([sQuery(id+"F11.wireOp",EDGE,"E8")])]}),"instanceName":"8"});
            var Q374;
            Q374=makeQuery(id+"F15.opPattern","COPY",BODY,{"derivedFrom":makeQuery(id+"F13.opExtrude","SWEPT_BODY",BODY,{"disambiguationData":[OSD([sQuery(id+"F11.wireOp",EDGE,"E9")])]}),"instanceName":"8"});
            var Q375;
            Q375=makeQuery(id+"F15.opPattern","COPY",BODY,{"derivedFrom":makeQuery(id+"F13.opExtrude","SWEPT_BODY",BODY,{"disambiguationData":[OSD([sQuery(id+"F11.wireOp",EDGE,"E11.0.1.0")])]}),"instanceName":"8"});
            var Q376;
            Q376=makeQuery(id+"F15.opPattern","COPY",BODY,{"derivedFrom":makeQuery(id+"F13.opExtrude","SWEPT_BODY",BODY,{"disambiguationData":[OSD([sQuery(id+"F11.wireOp",EDGE,"E11.0.2.0")])]}),"instanceName":"8"});
            var Q377;
            Q377=makeQuery(id+"F15.opPattern","COPY",BODY,{"derivedFrom":makeQuery(id+"F13.opExtrude","SWEPT_BODY",BODY,{"disambiguationData":[OSD([sQuery(id+"F11.wireOp",EDGE,"E11.0.3.0")])]}),"instanceName":"8"});
            var Q378;
            Q378=makeQuery(id+"F15.opPattern","COPY",BODY,{"derivedFrom":makeQuery(id+"F13.opExtrude","SWEPT_BODY",BODY,{"disambiguationData":[OSD([sQuery(id+"F11.wireOp",EDGE,"E11.0.3.0")])]}),"instanceName":"7"});
            var Q379;
            Q379=makeQuery(id+"F15.opPattern","COPY",BODY,{"derivedFrom":makeQuery(id+"F13.opExtrude","SWEPT_BODY",BODY,{"disambiguationData":[OSD([sQuery(id+"F11.wireOp",EDGE,"E11.0.2.0")])]}),"instanceName":"7"});
            var Q380;
            Q380=makeQuery(id+"F15.opPattern","COPY",BODY,{"derivedFrom":makeQuery(id+"F13.opExtrude","SWEPT_BODY",BODY,{"disambiguationData":[OSD([sQuery(id+"F11.wireOp",EDGE,"E11.0.1.0")])]}),"instanceName":"7"});
            var Q381;
            Q381=makeQuery(id+"F15.opPattern","COPY",BODY,{"derivedFrom":makeQuery(id+"F13.opExtrude","SWEPT_BODY",BODY,{"disambiguationData":[OSD([sQuery(id+"F11.wireOp",EDGE,"E9")])]}),"instanceName":"7"});
            var Q382;
            Q382=makeQuery(id+"F15.opPattern","COPY",BODY,{"derivedFrom":makeQuery(id+"F13.opExtrude","SWEPT_BODY",BODY,{"disambiguationData":[OSD([sQuery(id+"F11.wireOp",EDGE,"E8")])]}),"instanceName":"7"});
            var Q383;
            Q383=makeQuery(id+"F15.opPattern","COPY",BODY,{"derivedFrom":makeQuery(id+"F13.opExtrude","SWEPT_BODY",BODY,{"disambiguationData":[OSD([sQuery(id+"F11.wireOp",EDGE,"E10.0.1.0")])]}),"instanceName":"7"});
            var Q384;
            Q384=makeQuery(id+"F15.opPattern","COPY",BODY,{"derivedFrom":makeQuery(id+"F13.opExtrude","SWEPT_BODY",BODY,{"disambiguationData":[OSD([sQuery(id+"F11.wireOp",EDGE,"E10.0.2.0")])]}),"instanceName":"7"});
            var Q385;
            Q385=makeQuery(id+"F15.opPattern","COPY",BODY,{"derivedFrom":makeQuery(id+"F13.opExtrude","SWEPT_BODY",BODY,{"disambiguationData":[OSD([sQuery(id+"F11.wireOp",EDGE,"E10.0.3.0")])]}),"instanceName":"7"});
            var Q386;
            Q386=makeQuery(id+"F15.opPattern","COPY",BODY,{"derivedFrom":makeQuery(id+"F13.opExtrude","SWEPT_BODY",BODY,{"disambiguationData":[OSD([sQuery(id+"F11.wireOp",EDGE,"E11.0.3.0")])]}),"instanceName":"6"});
            var Q387;
            Q387=makeQuery(id+"F15.opPattern","COPY",BODY,{"derivedFrom":makeQuery(id+"F13.opExtrude","SWEPT_BODY",BODY,{"disambiguationData":[OSD([sQuery(id+"F11.wireOp",EDGE,"E11.0.2.0")])]}),"instanceName":"6"});
            var Q388;
            Q388=makeQuery(id+"F15.opPattern","COPY",BODY,{"derivedFrom":makeQuery(id+"F13.opExtrude","SWEPT_BODY",BODY,{"disambiguationData":[OSD([sQuery(id+"F11.wireOp",EDGE,"E11.0.1.0")])]}),"instanceName":"6"});
            var Q389;
            Q389=makeQuery(id+"F15.opPattern","COPY",BODY,{"derivedFrom":makeQuery(id+"F13.opExtrude","SWEPT_BODY",BODY,{"disambiguationData":[OSD([sQuery(id+"F11.wireOp",EDGE,"E9")])]}),"instanceName":"6"});
            var Q390;
            Q390=makeQuery(id+"F15.opPattern","COPY",BODY,{"derivedFrom":makeQuery(id+"F13.opExtrude","SWEPT_BODY",BODY,{"disambiguationData":[OSD([sQuery(id+"F11.wireOp",EDGE,"E8")])]}),"instanceName":"6"});
            var Q391;
            Q391=makeQuery(id+"F15.opPattern","COPY",BODY,{"derivedFrom":makeQuery(id+"F13.opExtrude","SWEPT_BODY",BODY,{"disambiguationData":[OSD([sQuery(id+"F11.wireOp",EDGE,"E10.0.1.0")])]}),"instanceName":"6"});
            var Q392;
            Q392=makeQuery(id+"F15.opPattern","COPY",BODY,{"derivedFrom":makeQuery(id+"F13.opExtrude","SWEPT_BODY",BODY,{"disambiguationData":[OSD([sQuery(id+"F11.wireOp",EDGE,"E10.0.2.0")])]}),"instanceName":"6"});
            var Q393;
            Q393=makeQuery(id+"F15.opPattern","COPY",BODY,{"derivedFrom":makeQuery(id+"F13.opExtrude","SWEPT_BODY",BODY,{"disambiguationData":[OSD([sQuery(id+"F11.wireOp",EDGE,"E10.0.3.0")])]}),"instanceName":"6"});
            var Q394;
            Q394=makeQuery(id+"F15.opPattern","COPY",BODY,{"derivedFrom":makeQuery(id+"F13.opExtrude","SWEPT_BODY",BODY,{"disambiguationData":[OSD([sQuery(id+"F11.wireOp",EDGE,"E10.0.3.0")])]}),"instanceName":"10"});
            var Q395;
            Q395=makeQuery(id+"F15.opPattern","COPY",BODY,{"derivedFrom":makeQuery(id+"F13.opExtrude","SWEPT_BODY",BODY,{"disambiguationData":[OSD([sQuery(id+"F11.wireOp",EDGE,"E10.0.2.0")])]}),"instanceName":"10"});
            var Q396;
            Q396=makeQuery(id+"F15.opPattern","COPY",BODY,{"derivedFrom":makeQuery(id+"F13.opExtrude","SWEPT_BODY",BODY,{"disambiguationData":[OSD([sQuery(id+"F11.wireOp",EDGE,"E10.0.1.0")])]}),"instanceName":"10"});
            var Q397;
            Q397=makeQuery(id+"F15.opPattern","COPY",BODY,{"derivedFrom":makeQuery(id+"F13.opExtrude","SWEPT_BODY",BODY,{"disambiguationData":[OSD([sQuery(id+"F11.wireOp",EDGE,"E8")])]}),"instanceName":"10"});
            var Q398;
            Q398=makeQuery(id+"F15.opPattern","COPY",BODY,{"derivedFrom":makeQuery(id+"F13.opExtrude","SWEPT_BODY",BODY,{"disambiguationData":[OSD([sQuery(id+"F11.wireOp",EDGE,"E9")])]}),"instanceName":"10"});
            var Q399;
            Q399=makeQuery(id+"F15.opPattern","COPY",BODY,{"derivedFrom":makeQuery(id+"F13.opExtrude","SWEPT_BODY",BODY,{"disambiguationData":[OSD([sQuery(id+"F11.wireOp",EDGE,"E11.0.1.0")])]}),"instanceName":"10"});
            var Q400;
            Q400=makeQuery(id+"F15.opPattern","COPY",BODY,{"derivedFrom":makeQuery(id+"F8.opExtrude","SWEPT_BODY",BODY,{"disambiguationData":[OSD([sQuery(id+"F5.wireOp",EDGE,"E5.0.4.0")])]}),"instanceName":"25"});
            var Q401;
            Q401=makeQuery(id+"F15.opPattern","COPY",BODY,{"derivedFrom":makeQuery(id+"F13.opExtrude","SWEPT_BODY",BODY,{"disambiguationData":[OSD([sQuery(id+"F11.wireOp",EDGE,"E11.0.3.0")])]}),"instanceName":"10"});
            var Q402;
            Q402=makeQuery(id+"F1.opExtrude","SWEPT_BODY",BODY,{"disambiguationData":[OSD([sQuery(id+"F0.wireOp",EDGE,"E0"),sQuery(id+"F0.wireOp",EDGE,"E1")])]});
            var Q403;
            Q403=makeQuery(id+"F15.opPattern","COPY",BODY,{"derivedFrom":makeQuery(id+"F13.opExtrude","SWEPT_BODY",BODY,{"disambiguationData":[OSD([sQuery(id+"F11.wireOp",EDGE,"E11.0.2.0")])]}),"instanceName":"10"});
            var Q404;
            Q404=makeQuery(id+"F15.opPattern","COPY",BODY,{"derivedFrom":makeQuery(id+"F13.opExtrude","SWEPT_BODY",BODY,{"disambiguationData":[OSD([sQuery(id+"F11.wireOp",EDGE,"E10.0.3.0")])]}),"instanceName":"11"});
            var Q405;
            Q405=makeQuery(id+"F15.opPattern","COPY",BODY,{"derivedFrom":makeQuery(id+"F13.opExtrude","SWEPT_BODY",BODY,{"disambiguationData":[OSD([sQuery(id+"F11.wireOp",EDGE,"E10.0.2.0")])]}),"instanceName":"11"});
            var Q406;
            Q406=makeQuery(id+"F15.opPattern","COPY",BODY,{"derivedFrom":makeQuery(id+"F13.opExtrude","SWEPT_BODY",BODY,{"disambiguationData":[OSD([sQuery(id+"F11.wireOp",EDGE,"E10.0.1.0")])]}),"instanceName":"11"});
            var Q407;
            Q407=makeQuery(id+"F15.opPattern","COPY",BODY,{"derivedFrom":makeQuery(id+"F13.opExtrude","SWEPT_BODY",BODY,{"disambiguationData":[OSD([sQuery(id+"F11.wireOp",EDGE,"E8")])]}),"instanceName":"11"});
            var Q408;
            Q408=makeQuery(id+"F15.opPattern","COPY",BODY,{"derivedFrom":makeQuery(id+"F13.opExtrude","SWEPT_BODY",BODY,{"disambiguationData":[OSD([sQuery(id+"F11.wireOp",EDGE,"E9")])]}),"instanceName":"11"});
            var Q409;
            Q409=makeQuery(id+"F15.opPattern","COPY",BODY,{"derivedFrom":makeQuery(id+"F13.opExtrude","SWEPT_BODY",BODY,{"disambiguationData":[OSD([sQuery(id+"F11.wireOp",EDGE,"E11.0.1.0")])]}),"instanceName":"11"});
            var Q410;
            Q410=makeQuery(id+"F15.opPattern","COPY",BODY,{"derivedFrom":makeQuery(id+"F13.opExtrude","SWEPT_BODY",BODY,{"disambiguationData":[OSD([sQuery(id+"F11.wireOp",EDGE,"E11.0.2.0")])]}),"instanceName":"11"});
            var Q411;
            Q411=makeQuery(id+"F15.opPattern","COPY",BODY,{"derivedFrom":makeQuery(id+"F13.opExtrude","SWEPT_BODY",BODY,{"disambiguationData":[OSD([sQuery(id+"F11.wireOp",EDGE,"E11.0.3.0")])]}),"instanceName":"11"});
            var Q412;
            Q412=makeQuery(id+"F15.opPattern","COPY",BODY,{"derivedFrom":makeQuery(id+"F13.opExtrude","SWEPT_BODY",BODY,{"disambiguationData":[OSD([sQuery(id+"F11.wireOp",EDGE,"E11.0.3.0")])]}),"instanceName":"12"});
            var Q413;
            Q413=makeQuery(id+"F15.opPattern","COPY",BODY,{"derivedFrom":makeQuery(id+"F13.opExtrude","SWEPT_BODY",BODY,{"disambiguationData":[OSD([sQuery(id+"F11.wireOp",EDGE,"E10.0.3.0")])]}),"instanceName":"12"});
            var Q414;
            Q414=makeQuery(id+"F15.opPattern","COPY",BODY,{"derivedFrom":makeQuery(id+"F13.opExtrude","SWEPT_BODY",BODY,{"disambiguationData":[OSD([sQuery(id+"F11.wireOp",EDGE,"E10.0.2.0")])]}),"instanceName":"12"});
            var Q415;
            Q415=makeQuery(id+"F15.opPattern","COPY",BODY,{"derivedFrom":makeQuery(id+"F13.opExtrude","SWEPT_BODY",BODY,{"disambiguationData":[OSD([sQuery(id+"F11.wireOp",EDGE,"E10.0.3.0")])]}),"instanceName":"12"});
            var Q416;
            Q416=makeQuery(id+"F15.opPattern","COPY",BODY,{"derivedFrom":makeQuery(id+"F13.opExtrude","SWEPT_BODY",BODY,{"disambiguationData":[OSD([sQuery(id+"F11.wireOp",EDGE,"E10.0.1.0")])]}),"instanceName":"12"});
            var Q417;
            Q417=makeQuery(id+"F15.opPattern","COPY",BODY,{"derivedFrom":makeQuery(id+"F13.opExtrude","SWEPT_BODY",BODY,{"disambiguationData":[OSD([sQuery(id+"F11.wireOp",EDGE,"E8")])]}),"instanceName":"12"});
            var Q418;
            Q418=makeQuery(id+"F15.opPattern","COPY",BODY,{"derivedFrom":makeQuery(id+"F13.opExtrude","SWEPT_BODY",BODY,{"disambiguationData":[OSD([sQuery(id+"F11.wireOp",EDGE,"E9")])]}),"instanceName":"12"});
            var Q419;
            Q419=makeQuery(id+"F15.opPattern","COPY",BODY,{"derivedFrom":makeQuery(id+"F13.opExtrude","SWEPT_BODY",BODY,{"disambiguationData":[OSD([sQuery(id+"F11.wireOp",EDGE,"E11.0.1.0")])]}),"instanceName":"12"});
            var Q420;
            Q420=makeQuery(id+"F15.opPattern","COPY",BODY,{"derivedFrom":makeQuery(id+"F13.opExtrude","SWEPT_BODY",BODY,{"disambiguationData":[OSD([sQuery(id+"F11.wireOp",EDGE,"E11.0.2.0")])]}),"instanceName":"12"});
            var Q421;
            Q421=makeQuery(id+"F15.opPattern","COPY",BODY,{"derivedFrom":makeQuery(id+"F8.opExtrude","SWEPT_BODY",BODY,{"disambiguationData":[OSD([sQuery(id+"F5.wireOp",EDGE,"E5.0.3.0")])]}),"instanceName":"5"});
            var Q422;
            Q422=makeQuery(id+"F15.opPattern","COPY",BODY,{"derivedFrom":makeQuery(id+"F8.opExtrude","SWEPT_BODY",BODY,{"disambiguationData":[OSD([sQuery(id+"F5.wireOp",EDGE,"E5.0.2.0")])]}),"instanceName":"5"});
            var Q423;
            Q423=makeQuery(id+"F15.opPattern","COPY",BODY,{"derivedFrom":makeQuery(id+"F8.opExtrude","SWEPT_BODY",BODY,{"disambiguationData":[OSD([sQuery(id+"F5.wireOp",EDGE,"E4")])]}),"instanceName":"5"});
            var Q424;
            Q424=makeQuery(id+"F15.opPattern","COPY",BODY,{"derivedFrom":makeQuery(id+"F8.opExtrude","SWEPT_BODY",BODY,{"disambiguationData":[OSD([sQuery(id+"F5.wireOp",EDGE,"E6.0.1.0")])]}),"instanceName":"5"});
            var Q425;
            Q425=makeQuery(id+"F15.opPattern","COPY",BODY,{"derivedFrom":makeQuery(id+"F8.opExtrude","SWEPT_BODY",BODY,{"disambiguationData":[OSD([sQuery(id+"F5.wireOp",EDGE,"E6.0.2.0")])]}),"instanceName":"5"});
            var Q426;
            Q426=makeQuery(id+"F15.opPattern","COPY",BODY,{"derivedFrom":makeQuery(id+"F8.opExtrude","SWEPT_BODY",BODY,{"disambiguationData":[OSD([sQuery(id+"F5.wireOp",EDGE,"E6.0.3.0")])]}),"instanceName":"5"});
            var Q427;
            Q427=makeQuery(id+"F15.opPattern","COPY",BODY,{"derivedFrom":makeQuery(id+"F8.opExtrude","SWEPT_BODY",BODY,{"disambiguationData":[OSD([sQuery(id+"F5.wireOp",EDGE,"E6.0.4.0")])]}),"instanceName":"5"});
            var Q428;
            Q428=makeQuery(id+"F15.opPattern","COPY",BODY,{"derivedFrom":makeQuery(id+"F8.opExtrude","SWEPT_BODY",BODY,{"disambiguationData":[OSD([sQuery(id+"F5.wireOp",EDGE,"E5.0.3.0")])]}),"instanceName":"6"});
            var Q429;
            Q429=makeQuery(id+"F15.opPattern","COPY",BODY,{"derivedFrom":makeQuery(id+"F8.opExtrude","SWEPT_BODY",BODY,{"disambiguationData":[OSD([sQuery(id+"F5.wireOp",EDGE,"E5.0.2.0")])]}),"instanceName":"6"});
            var Q430;
            Q430=makeQuery(id+"F15.opPattern","COPY",BODY,{"derivedFrom":makeQuery(id+"F8.opExtrude","SWEPT_BODY",BODY,{"disambiguationData":[OSD([sQuery(id+"F5.wireOp",EDGE,"E5.0.1.0")])]}),"instanceName":"6"});
            var Q431;
            Q431=makeQuery(id+"F15.opPattern","COPY",BODY,{"derivedFrom":makeQuery(id+"F8.opExtrude","SWEPT_BODY",BODY,{"disambiguationData":[OSD([sQuery(id+"F5.wireOp",EDGE,"E6.0.1.0")])]}),"instanceName":"6"});
            var Q432;
            Q432=makeQuery(id+"F15.opPattern","COPY",BODY,{"derivedFrom":makeQuery(id+"F8.opExtrude","SWEPT_BODY",BODY,{"disambiguationData":[OSD([sQuery(id+"F5.wireOp",EDGE,"E4")])]}),"instanceName":"6"});
            var Q433;
            Q433=makeQuery(id+"F15.opPattern","COPY",BODY,{"derivedFrom":makeQuery(id+"F8.opExtrude","SWEPT_BODY",BODY,{"disambiguationData":[OSD([sQuery(id+"F5.wireOp",EDGE,"E6.0.2.0")])]}),"instanceName":"6"});
            var Q434;
            Q434=makeQuery(id+"F15.opPattern","COPY",BODY,{"derivedFrom":makeQuery(id+"F8.opExtrude","SWEPT_BODY",BODY,{"disambiguationData":[OSD([sQuery(id+"F5.wireOp",EDGE,"E6.0.3.0")])]}),"instanceName":"6"});
            var Q435;
            Q435=makeQuery(id+"F15.opPattern","COPY",BODY,{"derivedFrom":makeQuery(id+"F8.opExtrude","SWEPT_BODY",BODY,{"disambiguationData":[OSD([sQuery(id+"F5.wireOp",EDGE,"E5.0.4.0")])]}),"instanceName":"7"});
            var Q436;
            Q436=makeQuery(id+"F15.opPattern","COPY",BODY,{"derivedFrom":makeQuery(id+"F8.opExtrude","SWEPT_BODY",BODY,{"disambiguationData":[OSD([sQuery(id+"F5.wireOp",EDGE,"E5.0.3.0")])]}),"instanceName":"7"});
            var Q437;
            Q437=makeQuery(id+"F15.opPattern","COPY",BODY,{"derivedFrom":makeQuery(id+"F8.opExtrude","SWEPT_BODY",BODY,{"disambiguationData":[OSD([sQuery(id+"F5.wireOp",EDGE,"E5.0.2.0")])]}),"instanceName":"7"});
            var Q438;
            Q438=makeQuery(id+"F15.opPattern","COPY",BODY,{"derivedFrom":makeQuery(id+"F8.opExtrude","SWEPT_BODY",BODY,{"disambiguationData":[OSD([sQuery(id+"F5.wireOp",EDGE,"E5.0.1.0")])]}),"instanceName":"7"});
            var Q439;
            Q439=makeQuery(id+"F15.opPattern","COPY",BODY,{"derivedFrom":makeQuery(id+"F8.opExtrude","SWEPT_BODY",BODY,{"disambiguationData":[OSD([sQuery(id+"F5.wireOp",EDGE,"E4")])]}),"instanceName":"7"});
            var Q440;
            Q440=makeQuery(id+"F15.opPattern","COPY",BODY,{"derivedFrom":makeQuery(id+"F8.opExtrude","SWEPT_BODY",BODY,{"disambiguationData":[OSD([sQuery(id+"F5.wireOp",EDGE,"E6.0.1.0")])]}),"instanceName":"7"});
            var Q441;
            Q441=makeQuery(id+"F15.opPattern","COPY",BODY,{"derivedFrom":makeQuery(id+"F8.opExtrude","SWEPT_BODY",BODY,{"disambiguationData":[OSD([sQuery(id+"F5.wireOp",EDGE,"E6.0.2.0")])]}),"instanceName":"7"});
            var Q442;
            Q442=makeQuery(id+"F15.opPattern","COPY",BODY,{"derivedFrom":makeQuery(id+"F8.opExtrude","SWEPT_BODY",BODY,{"disambiguationData":[OSD([sQuery(id+"F5.wireOp",EDGE,"E6.0.3.0")])]}),"instanceName":"7"});
            var Q443;
            Q443=makeQuery(id+"F15.opPattern","COPY",BODY,{"derivedFrom":makeQuery(id+"F8.opExtrude","SWEPT_BODY",BODY,{"disambiguationData":[OSD([sQuery(id+"F5.wireOp",EDGE,"E6.0.4.0")])]}),"instanceName":"7"});
            var Q444;
            Q444=makeQuery(id+"F15.opPattern","COPY",BODY,{"derivedFrom":makeQuery(id+"F8.opExtrude","SWEPT_BODY",BODY,{"disambiguationData":[OSD([sQuery(id+"F5.wireOp",EDGE,"E5.0.3.0")])]}),"instanceName":"8"});
            var Q445;
            Q445=makeQuery(id+"F15.opPattern","COPY",BODY,{"derivedFrom":makeQuery(id+"F8.opExtrude","SWEPT_BODY",BODY,{"disambiguationData":[OSD([sQuery(id+"F5.wireOp",EDGE,"E5.0.2.0")])]}),"instanceName":"8"});
            var Q446;
            Q446=makeQuery(id+"F15.opPattern","COPY",BODY,{"derivedFrom":makeQuery(id+"F8.opExtrude","SWEPT_BODY",BODY,{"disambiguationData":[OSD([sQuery(id+"F5.wireOp",EDGE,"E4")])]}),"instanceName":"8"});
            var Q447;
            Q447=makeQuery(id+"F15.opPattern","COPY",BODY,{"derivedFrom":makeQuery(id+"F8.opExtrude","SWEPT_BODY",BODY,{"disambiguationData":[OSD([sQuery(id+"F5.wireOp",EDGE,"E5.0.1.0")])]}),"instanceName":"8"});
            var Q448;
            Q448=makeQuery(id+"F15.opPattern","COPY",BODY,{"derivedFrom":makeQuery(id+"F8.opExtrude","SWEPT_BODY",BODY,{"disambiguationData":[OSD([sQuery(id+"F5.wireOp",EDGE,"E6.0.1.0")])]}),"instanceName":"8"});
            var Q449;
            Q449=makeQuery(id+"F15.opPattern","COPY",BODY,{"derivedFrom":makeQuery(id+"F8.opExtrude","SWEPT_BODY",BODY,{"disambiguationData":[OSD([sQuery(id+"F5.wireOp",EDGE,"E6.0.2.0")])]}),"instanceName":"8"});
            var Q450;
            Q450=makeQuery(id+"F15.opPattern","COPY",BODY,{"derivedFrom":makeQuery(id+"F8.opExtrude","SWEPT_BODY",BODY,{"disambiguationData":[OSD([sQuery(id+"F5.wireOp",EDGE,"E6.0.3.0")])]}),"instanceName":"8"});
            var Q451;
            Q451=makeQuery(id+"F15.opPattern","COPY",BODY,{"derivedFrom":makeQuery(id+"F8.opExtrude","SWEPT_BODY",BODY,{"disambiguationData":[OSD([sQuery(id+"F5.wireOp",EDGE,"E6.0.4.0")])]}),"instanceName":"8"});
            var Q452;
            Q452=makeQuery(id+"F15.opPattern","COPY",BODY,{"derivedFrom":makeQuery(id+"F8.opExtrude","SWEPT_BODY",BODY,{"disambiguationData":[OSD([sQuery(id+"F5.wireOp",EDGE,"E5.0.4.0")])]}),"instanceName":"8"});
            var Q453;
            Q453=makeQuery(id+"F15.opPattern","COPY",BODY,{"derivedFrom":makeQuery(id+"F8.opExtrude","SWEPT_BODY",BODY,{"disambiguationData":[OSD([sQuery(id+"F5.wireOp",EDGE,"E5.0.4.0")])]}),"instanceName":"9"});
            var Q454;
            Q454=makeQuery(id+"F15.opPattern","COPY",BODY,{"derivedFrom":makeQuery(id+"F8.opExtrude","SWEPT_BODY",BODY,{"disambiguationData":[OSD([sQuery(id+"F5.wireOp",EDGE,"E5.0.3.0")])]}),"instanceName":"9"});
            var Q455;
            Q455=makeQuery(id+"F15.opPattern","COPY",BODY,{"derivedFrom":makeQuery(id+"F8.opExtrude","SWEPT_BODY",BODY,{"disambiguationData":[OSD([sQuery(id+"F5.wireOp",EDGE,"E5.0.2.0")])]}),"instanceName":"9"});
            var Q456;
            Q456=makeQuery(id+"F15.opPattern","COPY",BODY,{"derivedFrom":makeQuery(id+"F8.opExtrude","SWEPT_BODY",BODY,{"disambiguationData":[OSD([sQuery(id+"F5.wireOp",EDGE,"E5.0.1.0")])]}),"instanceName":"9"});
            var Q457;
            Q457=makeQuery(id+"F15.opPattern","COPY",BODY,{"derivedFrom":makeQuery(id+"F8.opExtrude","SWEPT_BODY",BODY,{"disambiguationData":[OSD([sQuery(id+"F5.wireOp",EDGE,"E4")])]}),"instanceName":"9"});
            var Q458;
            Q458=makeQuery(id+"F15.opPattern","COPY",BODY,{"derivedFrom":makeQuery(id+"F8.opExtrude","SWEPT_BODY",BODY,{"disambiguationData":[OSD([sQuery(id+"F5.wireOp",EDGE,"E6.0.1.0")])]}),"instanceName":"9"});
            var Q459;
            Q459=makeQuery(id+"F15.opPattern","COPY",BODY,{"derivedFrom":makeQuery(id+"F8.opExtrude","SWEPT_BODY",BODY,{"disambiguationData":[OSD([sQuery(id+"F5.wireOp",EDGE,"E6.0.2.0")])]}),"instanceName":"9"});
            var Q460;
            Q460=makeQuery(id+"F15.opPattern","COPY",BODY,{"derivedFrom":makeQuery(id+"F8.opExtrude","SWEPT_BODY",BODY,{"disambiguationData":[OSD([sQuery(id+"F5.wireOp",EDGE,"E6.0.3.0")])]}),"instanceName":"9"});
            var Q461;
            Q461=makeQuery(id+"F15.opPattern","COPY",BODY,{"derivedFrom":makeQuery(id+"F8.opExtrude","SWEPT_BODY",BODY,{"disambiguationData":[OSD([sQuery(id+"F5.wireOp",EDGE,"E6.0.4.0")])]}),"instanceName":"9"});
            var Q462;
            Q462=makeQuery(id+"F15.opPattern","COPY",BODY,{"derivedFrom":makeQuery(id+"F8.opExtrude","SWEPT_BODY",BODY,{"disambiguationData":[OSD([sQuery(id+"F5.wireOp",EDGE,"E5.0.4.0")])]}),"instanceName":"10"});
            var Q463;
            Q463=makeQuery(id+"F15.opPattern","COPY",BODY,{"derivedFrom":makeQuery(id+"F8.opExtrude","SWEPT_BODY",BODY,{"disambiguationData":[OSD([sQuery(id+"F5.wireOp",EDGE,"E5.0.3.0")])]}),"instanceName":"10"});
            var Q464;
            Q464=makeQuery(id+"F15.opPattern","COPY",BODY,{"derivedFrom":makeQuery(id+"F8.opExtrude","SWEPT_BODY",BODY,{"disambiguationData":[OSD([sQuery(id+"F5.wireOp",EDGE,"E5.0.2.0")])]}),"instanceName":"10"});
            var Q465;
            Q465=makeQuery(id+"F15.opPattern","COPY",BODY,{"derivedFrom":makeQuery(id+"F8.opExtrude","SWEPT_BODY",BODY,{"disambiguationData":[OSD([sQuery(id+"F5.wireOp",EDGE,"E5.0.1.0")])]}),"instanceName":"10"});
            var Q466;
            Q466=makeQuery(id+"F15.opPattern","COPY",BODY,{"derivedFrom":makeQuery(id+"F8.opExtrude","SWEPT_BODY",BODY,{"disambiguationData":[OSD([sQuery(id+"F5.wireOp",EDGE,"E4")])]}),"instanceName":"10"});
            var Q467;
            Q467=makeQuery(id+"F15.opPattern","COPY",BODY,{"derivedFrom":makeQuery(id+"F8.opExtrude","SWEPT_BODY",BODY,{"disambiguationData":[OSD([sQuery(id+"F5.wireOp",EDGE,"E6.0.1.0")])]}),"instanceName":"10"});
            var Q468;
            Q468=makeQuery(id+"F15.opPattern","COPY",BODY,{"derivedFrom":makeQuery(id+"F8.opExtrude","SWEPT_BODY",BODY,{"disambiguationData":[OSD([sQuery(id+"F5.wireOp",EDGE,"E6.0.2.0")])]}),"instanceName":"10"});
            var Q469;
            Q469=makeQuery(id+"F15.opPattern","COPY",BODY,{"derivedFrom":makeQuery(id+"F8.opExtrude","SWEPT_BODY",BODY,{"disambiguationData":[OSD([sQuery(id+"F5.wireOp",EDGE,"E6.0.3.0")])]}),"instanceName":"10"});
            var Q470;
            Q470=makeQuery(id+"F15.opPattern","COPY",BODY,{"derivedFrom":makeQuery(id+"F8.opExtrude","SWEPT_BODY",BODY,{"disambiguationData":[OSD([sQuery(id+"F5.wireOp",EDGE,"E6.0.4.0")])]}),"instanceName":"10"});
            var Q471;
            Q471=makeQuery(id+"F15.opPattern","COPY",BODY,{"derivedFrom":makeQuery(id+"F8.opExtrude","SWEPT_BODY",BODY,{"disambiguationData":[OSD([sQuery(id+"F5.wireOp",EDGE,"E6.0.4.0")])]}),"instanceName":"11"});
            var Q472;
            Q472=makeQuery(id+"F15.opPattern","COPY",BODY,{"derivedFrom":makeQuery(id+"F8.opExtrude","SWEPT_BODY",BODY,{"disambiguationData":[OSD([sQuery(id+"F5.wireOp",EDGE,"E6.0.3.0")])]}),"instanceName":"11"});
            var Q473;
            Q473=makeQuery(id+"F15.opPattern","COPY",BODY,{"derivedFrom":makeQuery(id+"F8.opExtrude","SWEPT_BODY",BODY,{"disambiguationData":[OSD([sQuery(id+"F5.wireOp",EDGE,"E6.0.2.0")])]}),"instanceName":"11"});
            var Q474;
            Q474=makeQuery(id+"F15.opPattern","COPY",BODY,{"derivedFrom":makeQuery(id+"F8.opExtrude","SWEPT_BODY",BODY,{"disambiguationData":[OSD([sQuery(id+"F5.wireOp",EDGE,"E6.0.1.0")])]}),"instanceName":"11"});
            var Q475;
            Q475=makeQuery(id+"F15.opPattern","COPY",BODY,{"derivedFrom":makeQuery(id+"F8.opExtrude","SWEPT_BODY",BODY,{"disambiguationData":[OSD([sQuery(id+"F5.wireOp",EDGE,"E4")])]}),"instanceName":"11"});
            var Q476;
            Q476=makeQuery(id+"F15.opPattern","COPY",BODY,{"derivedFrom":makeQuery(id+"F8.opExtrude","SWEPT_BODY",BODY,{"disambiguationData":[OSD([sQuery(id+"F5.wireOp",EDGE,"E5.0.3.0")])]}),"instanceName":"11"});
            var Q477;
            Q477=makeQuery(id+"F15.opPattern","COPY",BODY,{"derivedFrom":makeQuery(id+"F8.opExtrude","SWEPT_BODY",BODY,{"disambiguationData":[OSD([sQuery(id+"F5.wireOp",EDGE,"E5.0.4.0")])]}),"instanceName":"11"});
            var Q478;
            Q478=makeQuery(id+"F15.opPattern","COPY",BODY,{"derivedFrom":makeQuery(id+"F8.opExtrude","SWEPT_BODY",BODY,{"disambiguationData":[OSD([sQuery(id+"F5.wireOp",EDGE,"E5.0.2.0")])]}),"instanceName":"11"});
            var Q479;
            Q479=makeQuery(id+"F15.opPattern","COPY",BODY,{"derivedFrom":makeQuery(id+"F8.opExtrude","SWEPT_BODY",BODY,{"disambiguationData":[OSD([sQuery(id+"F5.wireOp",EDGE,"E5.0.1.0")])]}),"instanceName":"11"});
            var Q480;
            Q480=makeQuery(id+"F15.opPattern","COPY",BODY,{"derivedFrom":makeQuery(id+"F8.opExtrude","SWEPT_BODY",BODY,{"disambiguationData":[OSD([sQuery(id+"F5.wireOp",EDGE,"E5.0.4.0")])]}),"instanceName":"12"});
            var Q481;
            Q481=makeQuery(id+"F15.opPattern","COPY",BODY,{"derivedFrom":makeQuery(id+"F8.opExtrude","SWEPT_BODY",BODY,{"disambiguationData":[OSD([sQuery(id+"F5.wireOp",EDGE,"E5.0.3.0")])]}),"instanceName":"12"});
            var Q482;
            Q482=makeQuery(id+"F15.opPattern","COPY",BODY,{"derivedFrom":makeQuery(id+"F8.opExtrude","SWEPT_BODY",BODY,{"disambiguationData":[OSD([sQuery(id+"F5.wireOp",EDGE,"E5.0.2.0")])]}),"instanceName":"12"});
            var Q483;
            Q483=makeQuery(id+"F15.opPattern","COPY",BODY,{"derivedFrom":makeQuery(id+"F8.opExtrude","SWEPT_BODY",BODY,{"disambiguationData":[OSD([sQuery(id+"F5.wireOp",EDGE,"E5.0.1.0")])]}),"instanceName":"12"});
            var Q484;
            Q484=makeQuery(id+"F15.opPattern","COPY",BODY,{"derivedFrom":makeQuery(id+"F8.opExtrude","SWEPT_BODY",BODY,{"disambiguationData":[OSD([sQuery(id+"F5.wireOp",EDGE,"E4")])]}),"instanceName":"12"});
            var Q485;
            Q485=makeQuery(id+"F15.opPattern","COPY",BODY,{"derivedFrom":makeQuery(id+"F8.opExtrude","SWEPT_BODY",BODY,{"disambiguationData":[OSD([sQuery(id+"F5.wireOp",EDGE,"E6.0.1.0")])]}),"instanceName":"12"});
            var Q486;
            Q486=makeQuery(id+"F15.opPattern","COPY",BODY,{"derivedFrom":makeQuery(id+"F8.opExtrude","SWEPT_BODY",BODY,{"disambiguationData":[OSD([sQuery(id+"F5.wireOp",EDGE,"E6.0.2.0")])]}),"instanceName":"12"});
            var Q487;
            Q487=makeQuery(id+"F15.opPattern","COPY",BODY,{"derivedFrom":makeQuery(id+"F8.opExtrude","SWEPT_BODY",BODY,{"disambiguationData":[OSD([sQuery(id+"F5.wireOp",EDGE,"E6.0.4.0")])]}),"instanceName":"12"});
            var Q488;
            Q488=makeQuery(id+"F15.opPattern","COPY",BODY,{"derivedFrom":makeQuery(id+"F8.opExtrude","SWEPT_BODY",BODY,{"disambiguationData":[OSD([sQuery(id+"F5.wireOp",EDGE,"E6.0.3.0")])]}),"instanceName":"12"});
            var Q489;
            Q489=makeQuery(id+"F15.opPattern","COPY",BODY,{"derivedFrom":makeQuery(id+"F8.opExtrude","SWEPT_BODY",BODY,{"disambiguationData":[OSD([sQuery(id+"F5.wireOp",EDGE,"E5.0.4.0")])]}),"instanceName":"13"});
            var Q490;
            Q490=makeQuery(id+"F15.opPattern","COPY",BODY,{"derivedFrom":makeQuery(id+"F8.opExtrude","SWEPT_BODY",BODY,{"disambiguationData":[OSD([sQuery(id+"F5.wireOp",EDGE,"E5.0.4.0")])]}),"instanceName":"13"});
            var Q491;
            Q491=makeQuery(id+"F15.opPattern","COPY",BODY,{"derivedFrom":makeQuery(id+"F8.opExtrude","SWEPT_BODY",BODY,{"disambiguationData":[OSD([sQuery(id+"F5.wireOp",EDGE,"E5.0.3.0")])]}),"instanceName":"13"});
            var Q492;
            Q492=makeQuery(id+"F15.opPattern","COPY",BODY,{"derivedFrom":makeQuery(id+"F8.opExtrude","SWEPT_BODY",BODY,{"disambiguationData":[OSD([sQuery(id+"F5.wireOp",EDGE,"E5.0.3.0")])]}),"instanceName":"13"});
            var Q493;
            Q493=makeQuery(id+"F15.opPattern","COPY",BODY,{"derivedFrom":makeQuery(id+"F8.opExtrude","SWEPT_BODY",BODY,{"disambiguationData":[OSD([sQuery(id+"F5.wireOp",EDGE,"E5.0.2.0")])]}),"instanceName":"13"});
            var Q494;
            Q494=makeQuery(id+"F15.opPattern","COPY",BODY,{"derivedFrom":makeQuery(id+"F8.opExtrude","SWEPT_BODY",BODY,{"disambiguationData":[OSD([sQuery(id+"F5.wireOp",EDGE,"E5.0.1.0")])]}),"instanceName":"13"});
            var Q495;
            Q495=makeQuery(id+"F15.opPattern","COPY",BODY,{"derivedFrom":makeQuery(id+"F8.opExtrude","SWEPT_BODY",BODY,{"disambiguationData":[OSD([sQuery(id+"F5.wireOp",EDGE,"E4")])]}),"instanceName":"13"});
            var Q496;
            Q496=makeQuery(id+"F13.opExtrude","SWEPT_BODY",BODY,{"disambiguationData":[OSD([sQuery(id+"F11.wireOp",EDGE,"E11.0.3.0")])]});
            var Q497;
            Q497=makeQuery(id+"F13.opExtrude","SWEPT_BODY",BODY,{"disambiguationData":[OSD([sQuery(id+"F11.wireOp",EDGE,"E11.0.2.0")])]});
            var Q498;
            Q498=makeQuery(id+"F15.opPattern","COPY",BODY,{"derivedFrom":makeQuery(id+"F8.opExtrude","SWEPT_BODY",BODY,{"disambiguationData":[OSD([sQuery(id+"F5.wireOp",EDGE,"E5.0.2.0")])]}),"instanceName":"13"});
            var Q499;
            Q499=makeQuery(id+"F13.opExtrude","SWEPT_BODY",BODY,{"disambiguationData":[OSD([sQuery(id+"F11.wireOp",EDGE,"E11.0.1.0")])]});
            var Q500;
            Q500=makeQuery(id+"F13.opExtrude","SWEPT_BODY",BODY,{"disambiguationData":[OSD([sQuery(id+"F11.wireOp",EDGE,"E9")])]});
            var Q501;
            Q501=makeQuery(id+"F13.opExtrude","SWEPT_BODY",BODY,{"disambiguationData":[OSD([sQuery(id+"F11.wireOp",EDGE,"E8")])]});
            var Q502;
            Q502=makeQuery(id+"F13.opExtrude","SWEPT_BODY",BODY,{"disambiguationData":[OSD([sQuery(id+"F11.wireOp",EDGE,"E10.0.1.0")])]});
            var Q503;
            Q503=makeQuery(id+"F13.opExtrude","SWEPT_BODY",BODY,{"disambiguationData":[OSD([sQuery(id+"F11.wireOp",EDGE,"E10.0.2.0")])]});
            var Q504;
            Q504=makeQuery(id+"F13.opExtrude","SWEPT_BODY",BODY,{"disambiguationData":[OSD([sQuery(id+"F11.wireOp",EDGE,"E10.0.3.0")])]});
            var Q505;
            Q505=makeQuery(id+"F15.opPattern","COPY",BODY,{"derivedFrom":makeQuery(id+"F13.opExtrude","SWEPT_BODY",BODY,{"disambiguationData":[OSD([sQuery(id+"F11.wireOp",EDGE,"E8")])]}),"instanceName":"1"});
            var Q506;
            Q506=makeQuery(id+"F1.opExtrude","SWEPT_BODY",BODY,{"disambiguationData":[OSD([sQuery(id+"F0.wireOp",EDGE,"E0"),sQuery(id+"F0.wireOp",EDGE,"E1")])]});
            var Q507;
            Q507=makeQuery(id+"F15.opPattern","COPY",BODY,{"derivedFrom":makeQuery(id+"F8.opExtrude","SWEPT_BODY",BODY,{"disambiguationData":[OSD([sQuery(id+"F5.wireOp",EDGE,"E5.0.1.0")])]}),"instanceName":"13"});
            var Q508;
            Q508=makeQuery(id+"F15.opPattern","COPY",BODY,{"derivedFrom":makeQuery(id+"F13.opExtrude","SWEPT_BODY",BODY,{"disambiguationData":[OSD([sQuery(id+"F11.wireOp",EDGE,"E11.0.3.0")])]}),"instanceName":"12"});
            var Q509;
            Q509=makeQuery(id+"F15.opPattern","COPY",BODY,{"derivedFrom":makeQuery(id+"F13.opExtrude","SWEPT_BODY",BODY,{"disambiguationData":[OSD([sQuery(id+"F11.wireOp",EDGE,"E11.0.2.0")])]}),"instanceName":"12"});
            var Q510;
            Q510=makeQuery(id+"F15.opPattern","COPY",BODY,{"derivedFrom":makeQuery(id+"F13.opExtrude","SWEPT_BODY",BODY,{"disambiguationData":[OSD([sQuery(id+"F11.wireOp",EDGE,"E11.0.1.0")])]}),"instanceName":"12"});
            var Q511;
            Q511=makeQuery(id+"F15.opPattern","COPY",BODY,{"derivedFrom":makeQuery(id+"F13.opExtrude","SWEPT_BODY",BODY,{"disambiguationData":[OSD([sQuery(id+"F11.wireOp",EDGE,"E10.0.2.0")])]}),"instanceName":"12"});
            var Q512;
            Q512=makeQuery(id+"F15.opPattern","COPY",BODY,{"derivedFrom":makeQuery(id+"F13.opExtrude","SWEPT_BODY",BODY,{"disambiguationData":[OSD([sQuery(id+"F11.wireOp",EDGE,"E10.0.1.0")])]}),"instanceName":"12"});
            var Q513;
            Q513=makeQuery(id+"F15.opPattern","COPY",BODY,{"derivedFrom":makeQuery(id+"F13.opExtrude","SWEPT_BODY",BODY,{"disambiguationData":[OSD([sQuery(id+"F11.wireOp",EDGE,"E9")])]}),"instanceName":"12"});
            var Q514;
            Q514=makeQuery(id+"F15.opPattern","COPY",BODY,{"derivedFrom":makeQuery(id+"F13.opExtrude","SWEPT_BODY",BODY,{"disambiguationData":[OSD([sQuery(id+"F11.wireOp",EDGE,"E8")])]}),"instanceName":"12"});
            var Q515;
            Q515=makeQuery(id+"F15.opPattern","COPY",BODY,{"derivedFrom":makeQuery(id+"F8.opExtrude","SWEPT_BODY",BODY,{"disambiguationData":[OSD([sQuery(id+"F5.wireOp",EDGE,"E4")])]}),"instanceName":"13"});
            var Q516;
            Q516=makeQuery(id+"F15.opPattern","COPY",BODY,{"derivedFrom":makeQuery(id+"F13.opExtrude","SWEPT_BODY",BODY,{"disambiguationData":[OSD([sQuery(id+"F11.wireOp",EDGE,"E10.0.3.0")])]}),"instanceName":"12"});
            var Q517;
            Q517=makeQuery(id+"F15.opPattern","COPY",BODY,{"derivedFrom":makeQuery(id+"F8.opExtrude","SWEPT_BODY",BODY,{"disambiguationData":[OSD([sQuery(id+"F5.wireOp",EDGE,"E6.0.4.0")])]}),"instanceName":"12"});
            var Q518;
            Q518=makeQuery(id+"F15.opPattern","COPY",BODY,{"derivedFrom":makeQuery(id+"F8.opExtrude","SWEPT_BODY",BODY,{"disambiguationData":[OSD([sQuery(id+"F5.wireOp",EDGE,"E6.0.3.0")])]}),"instanceName":"12"});
            var Q519;
            Q519=makeQuery(id+"F15.opPattern","COPY",BODY,{"derivedFrom":makeQuery(id+"F8.opExtrude","SWEPT_BODY",BODY,{"disambiguationData":[OSD([sQuery(id+"F5.wireOp",EDGE,"E6.0.2.0")])]}),"instanceName":"12"});
            var Q520;
            Q520=makeQuery(id+"F15.opPattern","COPY",BODY,{"derivedFrom":makeQuery(id+"F8.opExtrude","SWEPT_BODY",BODY,{"disambiguationData":[OSD([sQuery(id+"F5.wireOp",EDGE,"E6.0.1.0")])]}),"instanceName":"12"});
            var Q521;
            Q521=makeQuery(id+"F15.opPattern","COPY",BODY,{"derivedFrom":makeQuery(id+"F8.opExtrude","SWEPT_BODY",BODY,{"disambiguationData":[OSD([sQuery(id+"F5.wireOp",EDGE,"E5.0.4.0")])]}),"instanceName":"12"});
            var Q522;
            Q522=makeQuery(id+"F15.opPattern","COPY",BODY,{"derivedFrom":makeQuery(id+"F8.opExtrude","SWEPT_BODY",BODY,{"disambiguationData":[OSD([sQuery(id+"F5.wireOp",EDGE,"E5.0.3.0")])]}),"instanceName":"12"});
            var Q523;
            Q523=makeQuery(id+"F15.opPattern","COPY",BODY,{"derivedFrom":makeQuery(id+"F8.opExtrude","SWEPT_BODY",BODY,{"disambiguationData":[OSD([sQuery(id+"F5.wireOp",EDGE,"E5.0.2.0")])]}),"instanceName":"12"});
            var Q524;
            Q524=makeQuery(id+"F15.opPattern","COPY",BODY,{"derivedFrom":makeQuery(id+"F8.opExtrude","SWEPT_BODY",BODY,{"disambiguationData":[OSD([sQuery(id+"F5.wireOp",EDGE,"E5.0.1.0")])]}),"instanceName":"12"});
            var Q525;
            Q525=makeQuery(id+"F15.opPattern","COPY",BODY,{"derivedFrom":makeQuery(id+"F8.opExtrude","SWEPT_BODY",BODY,{"disambiguationData":[OSD([sQuery(id+"F5.wireOp",EDGE,"E4")])]}),"instanceName":"12"});
            var Q526;
            Q526=makeQuery(id+"F15.opPattern","COPY",BODY,{"derivedFrom":makeQuery(id+"F13.opExtrude","SWEPT_BODY",BODY,{"disambiguationData":[OSD([sQuery(id+"F11.wireOp",EDGE,"E11.0.3.0")])]}),"instanceName":"11"});
            var Q527;
            Q527=makeQuery(id+"F15.opPattern","COPY",BODY,{"derivedFrom":makeQuery(id+"F13.opExtrude","SWEPT_BODY",BODY,{"disambiguationData":[OSD([sQuery(id+"F11.wireOp",EDGE,"E11.0.2.0")])]}),"instanceName":"11"});
            var Q528;
            Q528=makeQuery(id+"F15.opPattern","COPY",BODY,{"derivedFrom":makeQuery(id+"F13.opExtrude","SWEPT_BODY",BODY,{"disambiguationData":[OSD([sQuery(id+"F11.wireOp",EDGE,"E11.0.1.0")])]}),"instanceName":"11"});
            var Q529;
            Q529=makeQuery(id+"F15.opPattern","COPY",BODY,{"derivedFrom":makeQuery(id+"F13.opExtrude","SWEPT_BODY",BODY,{"disambiguationData":[OSD([sQuery(id+"F11.wireOp",EDGE,"E10.0.3.0")])]}),"instanceName":"11"});
            var Q530;
            Q530=makeQuery(id+"F15.opPattern","COPY",BODY,{"derivedFrom":makeQuery(id+"F13.opExtrude","SWEPT_BODY",BODY,{"disambiguationData":[OSD([sQuery(id+"F11.wireOp",EDGE,"E10.0.2.0")])]}),"instanceName":"11"});
            var Q531;
            Q531=makeQuery(id+"F15.opPattern","COPY",BODY,{"derivedFrom":makeQuery(id+"F13.opExtrude","SWEPT_BODY",BODY,{"disambiguationData":[OSD([sQuery(id+"F11.wireOp",EDGE,"E10.0.1.0")])]}),"instanceName":"11"});
            var Q532;
            Q532=makeQuery(id+"F15.opPattern","COPY",BODY,{"derivedFrom":makeQuery(id+"F13.opExtrude","SWEPT_BODY",BODY,{"disambiguationData":[OSD([sQuery(id+"F11.wireOp",EDGE,"E9")])]}),"instanceName":"11"});
            var Q533;
            Q533=makeQuery(id+"F15.opPattern","COPY",BODY,{"derivedFrom":makeQuery(id+"F13.opExtrude","SWEPT_BODY",BODY,{"disambiguationData":[OSD([sQuery(id+"F11.wireOp",EDGE,"E8")])]}),"instanceName":"11"});
            var Q534;
            Q534=makeQuery(id+"F15.opPattern","COPY",BODY,{"derivedFrom":makeQuery(id+"F8.opExtrude","SWEPT_BODY",BODY,{"disambiguationData":[OSD([sQuery(id+"F5.wireOp",EDGE,"E6.0.4.0")])]}),"instanceName":"11"});
            var Q535;
            Q535=makeQuery(id+"F15.opPattern","COPY",BODY,{"derivedFrom":makeQuery(id+"F8.opExtrude","SWEPT_BODY",BODY,{"disambiguationData":[OSD([sQuery(id+"F5.wireOp",EDGE,"E6.0.3.0")])]}),"instanceName":"11"});
            var Q536;
            Q536=makeQuery(id+"F15.opPattern","COPY",BODY,{"derivedFrom":makeQuery(id+"F8.opExtrude","SWEPT_BODY",BODY,{"disambiguationData":[OSD([sQuery(id+"F5.wireOp",EDGE,"E6.0.2.0")])]}),"instanceName":"11"});
            var Q537;
            Q537=makeQuery(id+"F15.opPattern","COPY",BODY,{"derivedFrom":makeQuery(id+"F8.opExtrude","SWEPT_BODY",BODY,{"disambiguationData":[OSD([sQuery(id+"F5.wireOp",EDGE,"E6.0.1.0")])]}),"instanceName":"11"});
            var Q538;
            Q538=makeQuery(id+"F15.opPattern","COPY",BODY,{"derivedFrom":makeQuery(id+"F8.opExtrude","SWEPT_BODY",BODY,{"disambiguationData":[OSD([sQuery(id+"F5.wireOp",EDGE,"E5.0.4.0")])]}),"instanceName":"11"});
            var Q539;
            Q539=makeQuery(id+"F15.opPattern","COPY",BODY,{"derivedFrom":makeQuery(id+"F8.opExtrude","SWEPT_BODY",BODY,{"disambiguationData":[OSD([sQuery(id+"F5.wireOp",EDGE,"E5.0.3.0")])]}),"instanceName":"11"});
            var Q540;
            Q540=makeQuery(id+"F15.opPattern","COPY",BODY,{"derivedFrom":makeQuery(id+"F8.opExtrude","SWEPT_BODY",BODY,{"disambiguationData":[OSD([sQuery(id+"F5.wireOp",EDGE,"E5.0.2.0")])]}),"instanceName":"11"});
            var Q541;
            Q541=makeQuery(id+"F15.opPattern","COPY",BODY,{"derivedFrom":makeQuery(id+"F8.opExtrude","SWEPT_BODY",BODY,{"disambiguationData":[OSD([sQuery(id+"F5.wireOp",EDGE,"E5.0.1.0")])]}),"instanceName":"11"});
            var Q542;
            Q542=makeQuery(id+"F15.opPattern","COPY",BODY,{"derivedFrom":makeQuery(id+"F8.opExtrude","SWEPT_BODY",BODY,{"disambiguationData":[OSD([sQuery(id+"F5.wireOp",EDGE,"E4")])]}),"instanceName":"11"});
            var Q543;
            Q543=makeQuery(id+"F15.opPattern","COPY",BODY,{"derivedFrom":makeQuery(id+"F13.opExtrude","SWEPT_BODY",BODY,{"disambiguationData":[OSD([sQuery(id+"F11.wireOp",EDGE,"E11.0.3.0")])]}),"instanceName":"10"});
            var Q544;
            Q544=makeQuery(id+"F15.opPattern","COPY",BODY,{"derivedFrom":makeQuery(id+"F13.opExtrude","SWEPT_BODY",BODY,{"disambiguationData":[OSD([sQuery(id+"F11.wireOp",EDGE,"E11.0.2.0")])]}),"instanceName":"10"});
            var Q545;
            Q545=makeQuery(id+"F15.opPattern","COPY",BODY,{"derivedFrom":makeQuery(id+"F13.opExtrude","SWEPT_BODY",BODY,{"disambiguationData":[OSD([sQuery(id+"F11.wireOp",EDGE,"E11.0.1.0")])]}),"instanceName":"10"});
            var Q546;
            Q546=makeQuery(id+"F15.opPattern","COPY",BODY,{"derivedFrom":makeQuery(id+"F13.opExtrude","SWEPT_BODY",BODY,{"disambiguationData":[OSD([sQuery(id+"F11.wireOp",EDGE,"E10.0.3.0")])]}),"instanceName":"10"});
            var Q547;
            Q547=makeQuery(id+"F15.opPattern","COPY",BODY,{"derivedFrom":makeQuery(id+"F13.opExtrude","SWEPT_BODY",BODY,{"disambiguationData":[OSD([sQuery(id+"F11.wireOp",EDGE,"E10.0.1.0")])]}),"instanceName":"10"});
            var Q548;
            Q548=makeQuery(id+"F15.opPattern","COPY",BODY,{"derivedFrom":makeQuery(id+"F13.opExtrude","SWEPT_BODY",BODY,{"disambiguationData":[OSD([sQuery(id+"F11.wireOp",EDGE,"E9")])]}),"instanceName":"10"});
            var Q549;
            Q549=makeQuery(id+"F15.opPattern","COPY",BODY,{"derivedFrom":makeQuery(id+"F8.opExtrude","SWEPT_BODY",BODY,{"disambiguationData":[OSD([sQuery(id+"F5.wireOp",EDGE,"E6.0.4.0")])]}),"instanceName":"10"});
            var Q550;
            Q550=makeQuery(id+"F15.opPattern","COPY",BODY,{"derivedFrom":makeQuery(id+"F8.opExtrude","SWEPT_BODY",BODY,{"disambiguationData":[OSD([sQuery(id+"F5.wireOp",EDGE,"E6.0.3.0")])]}),"instanceName":"10"});
            var Q551;
            Q551=makeQuery(id+"F15.opPattern","COPY",BODY,{"derivedFrom":makeQuery(id+"F13.opExtrude","SWEPT_BODY",BODY,{"disambiguationData":[OSD([sQuery(id+"F11.wireOp",EDGE,"E8")])]}),"instanceName":"10"});
            var Q552;
            Q552=makeQuery(id+"F15.opPattern","COPY",BODY,{"derivedFrom":makeQuery(id+"F13.opExtrude","SWEPT_BODY",BODY,{"disambiguationData":[OSD([sQuery(id+"F11.wireOp",EDGE,"E10.0.2.0")])]}),"instanceName":"10"});
            var Q553;
            Q553=makeQuery(id+"F15.opPattern","COPY",BODY,{"derivedFrom":makeQuery(id+"F8.opExtrude","SWEPT_BODY",BODY,{"disambiguationData":[OSD([sQuery(id+"F5.wireOp",EDGE,"E6.0.2.0")])]}),"instanceName":"10"});
            var Q554;
            Q554=makeQuery(id+"F15.opPattern","COPY",BODY,{"derivedFrom":makeQuery(id+"F8.opExtrude","SWEPT_BODY",BODY,{"disambiguationData":[OSD([sQuery(id+"F5.wireOp",EDGE,"E6.0.1.0")])]}),"instanceName":"10"});
            var Q555;
            Q555=makeQuery(id+"F15.opPattern","COPY",BODY,{"derivedFrom":makeQuery(id+"F8.opExtrude","SWEPT_BODY",BODY,{"disambiguationData":[OSD([sQuery(id+"F5.wireOp",EDGE,"E5.0.4.0")])]}),"instanceName":"10"});
            var Q556;
            Q556=makeQuery(id+"F15.opPattern","COPY",BODY,{"derivedFrom":makeQuery(id+"F8.opExtrude","SWEPT_BODY",BODY,{"disambiguationData":[OSD([sQuery(id+"F5.wireOp",EDGE,"E5.0.3.0")])]}),"instanceName":"10"});
            var Q557;
            Q557=makeQuery(id+"F15.opPattern","COPY",BODY,{"derivedFrom":makeQuery(id+"F8.opExtrude","SWEPT_BODY",BODY,{"disambiguationData":[OSD([sQuery(id+"F5.wireOp",EDGE,"E5.0.2.0")])]}),"instanceName":"10"});
            var Q558;
            Q558=makeQuery(id+"F15.opPattern","COPY",BODY,{"derivedFrom":makeQuery(id+"F8.opExtrude","SWEPT_BODY",BODY,{"disambiguationData":[OSD([sQuery(id+"F5.wireOp",EDGE,"E5.0.1.0")])]}),"instanceName":"10"});
            var Q559;
            Q559=makeQuery(id+"F15.opPattern","COPY",BODY,{"derivedFrom":makeQuery(id+"F8.opExtrude","SWEPT_BODY",BODY,{"disambiguationData":[OSD([sQuery(id+"F5.wireOp",EDGE,"E4")])]}),"instanceName":"10"});
            var Q560;
            Q560=makeQuery(id+"F15.opPattern","COPY",BODY,{"derivedFrom":makeQuery(id+"F13.opExtrude","SWEPT_BODY",BODY,{"disambiguationData":[OSD([sQuery(id+"F11.wireOp",EDGE,"E11.0.3.0")])]}),"instanceName":"9"});
            var Q561;
            Q561=makeQuery(id+"F15.opPattern","COPY",BODY,{"derivedFrom":makeQuery(id+"F13.opExtrude","SWEPT_BODY",BODY,{"disambiguationData":[OSD([sQuery(id+"F11.wireOp",EDGE,"E11.0.2.0")])]}),"instanceName":"9"});
            var Q562;
            Q562=makeQuery(id+"F15.opPattern","COPY",BODY,{"derivedFrom":makeQuery(id+"F13.opExtrude","SWEPT_BODY",BODY,{"disambiguationData":[OSD([sQuery(id+"F11.wireOp",EDGE,"E11.0.1.0")])]}),"instanceName":"9"});
            var Q563;
            Q563=makeQuery(id+"F15.opPattern","COPY",BODY,{"derivedFrom":makeQuery(id+"F13.opExtrude","SWEPT_BODY",BODY,{"disambiguationData":[OSD([sQuery(id+"F11.wireOp",EDGE,"E10.0.3.0")])]}),"instanceName":"9"});
            var Q564;
            Q564=makeQuery(id+"F15.opPattern","COPY",BODY,{"derivedFrom":makeQuery(id+"F13.opExtrude","SWEPT_BODY",BODY,{"disambiguationData":[OSD([sQuery(id+"F11.wireOp",EDGE,"E10.0.2.0")])]}),"instanceName":"9"});
            var Q565;
            Q565=makeQuery(id+"F15.opPattern","COPY",BODY,{"derivedFrom":makeQuery(id+"F13.opExtrude","SWEPT_BODY",BODY,{"disambiguationData":[OSD([sQuery(id+"F11.wireOp",EDGE,"E10.0.1.0")])]}),"instanceName":"9"});
            var Q566;
            Q566=makeQuery(id+"F15.opPattern","COPY",BODY,{"derivedFrom":makeQuery(id+"F13.opExtrude","SWEPT_BODY",BODY,{"disambiguationData":[OSD([sQuery(id+"F11.wireOp",EDGE,"E9")])]}),"instanceName":"9"});
            var Q567;
            Q567=makeQuery(id+"F15.opPattern","COPY",BODY,{"derivedFrom":makeQuery(id+"F13.opExtrude","SWEPT_BODY",BODY,{"disambiguationData":[OSD([sQuery(id+"F11.wireOp",EDGE,"E8")])]}),"instanceName":"9"});
            var Q568;
            Q568=makeQuery(id+"F15.opPattern","COPY",BODY,{"derivedFrom":makeQuery(id+"F8.opExtrude","SWEPT_BODY",BODY,{"disambiguationData":[OSD([sQuery(id+"F5.wireOp",EDGE,"E6.0.4.0")])]}),"instanceName":"9"});
            var Q569;
            Q569=makeQuery(id+"F15.opPattern","COPY",BODY,{"derivedFrom":makeQuery(id+"F8.opExtrude","SWEPT_BODY",BODY,{"disambiguationData":[OSD([sQuery(id+"F5.wireOp",EDGE,"E6.0.3.0")])]}),"instanceName":"9"});
            var Q570;
            Q570=makeQuery(id+"F15.opPattern","COPY",BODY,{"derivedFrom":makeQuery(id+"F8.opExtrude","SWEPT_BODY",BODY,{"disambiguationData":[OSD([sQuery(id+"F5.wireOp",EDGE,"E6.0.2.0")])]}),"instanceName":"9"});
            var Q571;
            Q571=makeQuery(id+"F15.opPattern","COPY",BODY,{"derivedFrom":makeQuery(id+"F8.opExtrude","SWEPT_BODY",BODY,{"disambiguationData":[OSD([sQuery(id+"F5.wireOp",EDGE,"E6.0.1.0")])]}),"instanceName":"9"});
            var Q572;
            Q572=makeQuery(id+"F15.opPattern","COPY",BODY,{"derivedFrom":makeQuery(id+"F8.opExtrude","SWEPT_BODY",BODY,{"disambiguationData":[OSD([sQuery(id+"F5.wireOp",EDGE,"E5.0.4.0")])]}),"instanceName":"9"});
            var Q573;
            Q573=makeQuery(id+"F15.opPattern","COPY",BODY,{"derivedFrom":makeQuery(id+"F8.opExtrude","SWEPT_BODY",BODY,{"disambiguationData":[OSD([sQuery(id+"F5.wireOp",EDGE,"E4")])]}),"instanceName":"9"});
            var Q574;
            Q574=makeQuery(id+"F15.opPattern","COPY",BODY,{"derivedFrom":makeQuery(id+"F13.opExtrude","SWEPT_BODY",BODY,{"disambiguationData":[OSD([sQuery(id+"F11.wireOp",EDGE,"E11.0.3.0")])]}),"instanceName":"8"});
            var Q575;
            Q575=makeQuery(id+"F15.opPattern","COPY",BODY,{"derivedFrom":makeQuery(id+"F13.opExtrude","SWEPT_BODY",BODY,{"disambiguationData":[OSD([sQuery(id+"F11.wireOp",EDGE,"E11.0.2.0")])]}),"instanceName":"8"});
            var Q576;
            Q576=makeQuery(id+"F15.opPattern","COPY",BODY,{"derivedFrom":makeQuery(id+"F8.opExtrude","SWEPT_BODY",BODY,{"disambiguationData":[OSD([sQuery(id+"F5.wireOp",EDGE,"E5.0.4.0")])]}),"instanceName":"8"});
            var Q577;
            Q577=makeQuery(id+"F15.opPattern","COPY",BODY,{"derivedFrom":makeQuery(id+"F8.opExtrude","SWEPT_BODY",BODY,{"disambiguationData":[OSD([sQuery(id+"F5.wireOp",EDGE,"E4")])]}),"instanceName":"8"});
            var Q578;
            Q578=makeQuery(id+"F15.opPattern","COPY",BODY,{"derivedFrom":makeQuery(id+"F8.opExtrude","SWEPT_BODY",BODY,{"disambiguationData":[OSD([sQuery(id+"F5.wireOp",EDGE,"E5.0.1.0")])]}),"instanceName":"9"});
            var Q579;
            Q579=makeQuery(id+"F15.opPattern","COPY",BODY,{"derivedFrom":makeQuery(id+"F8.opExtrude","SWEPT_BODY",BODY,{"disambiguationData":[OSD([sQuery(id+"F5.wireOp",EDGE,"E5.0.2.0")])]}),"instanceName":"9"});
            var Q580;
            Q580=makeQuery(id+"F15.opPattern","COPY",BODY,{"derivedFrom":makeQuery(id+"F8.opExtrude","SWEPT_BODY",BODY,{"disambiguationData":[OSD([sQuery(id+"F5.wireOp",EDGE,"E5.0.3.0")])]}),"instanceName":"9"});
            var Q581;
            Q581=makeQuery(id+"F15.opPattern","COPY",BODY,{"derivedFrom":makeQuery(id+"F13.opExtrude","SWEPT_BODY",BODY,{"disambiguationData":[OSD([sQuery(id+"F11.wireOp",EDGE,"E11.0.1.0")])]}),"instanceName":"8"});
            var Q582;
            Q582=makeQuery(id+"F15.opPattern","COPY",BODY,{"derivedFrom":makeQuery(id+"F13.opExtrude","SWEPT_BODY",BODY,{"disambiguationData":[OSD([sQuery(id+"F11.wireOp",EDGE,"E10.0.3.0")])]}),"instanceName":"8"});
            var Q583;
            Q583=makeQuery(id+"F15.opPattern","COPY",BODY,{"derivedFrom":makeQuery(id+"F13.opExtrude","SWEPT_BODY",BODY,{"disambiguationData":[OSD([sQuery(id+"F11.wireOp",EDGE,"E10.0.2.0")])]}),"instanceName":"8"});
            var Q584;
            Q584=makeQuery(id+"F15.opPattern","COPY",BODY,{"derivedFrom":makeQuery(id+"F13.opExtrude","SWEPT_BODY",BODY,{"disambiguationData":[OSD([sQuery(id+"F11.wireOp",EDGE,"E10.0.1.0")])]}),"instanceName":"8"});
            var Q585;
            Q585=makeQuery(id+"F15.opPattern","COPY",BODY,{"derivedFrom":makeQuery(id+"F13.opExtrude","SWEPT_BODY",BODY,{"disambiguationData":[OSD([sQuery(id+"F11.wireOp",EDGE,"E9")])]}),"instanceName":"8"});
            var Q586;
            Q586=makeQuery(id+"F15.opPattern","COPY",BODY,{"derivedFrom":makeQuery(id+"F13.opExtrude","SWEPT_BODY",BODY,{"disambiguationData":[OSD([sQuery(id+"F11.wireOp",EDGE,"E8")])]}),"instanceName":"8"});
            var Q587;
            Q587=makeQuery(id+"F15.opPattern","COPY",BODY,{"derivedFrom":makeQuery(id+"F8.opExtrude","SWEPT_BODY",BODY,{"disambiguationData":[OSD([sQuery(id+"F5.wireOp",EDGE,"E6.0.4.0")])]}),"instanceName":"8"});
            var Q588;
            Q588=makeQuery(id+"F15.opPattern","COPY",BODY,{"derivedFrom":makeQuery(id+"F8.opExtrude","SWEPT_BODY",BODY,{"disambiguationData":[OSD([sQuery(id+"F5.wireOp",EDGE,"E6.0.3.0")])]}),"instanceName":"8"});
            var Q589;
            Q589=makeQuery(id+"F15.opPattern","COPY",BODY,{"derivedFrom":makeQuery(id+"F8.opExtrude","SWEPT_BODY",BODY,{"disambiguationData":[OSD([sQuery(id+"F5.wireOp",EDGE,"E6.0.2.0")])]}),"instanceName":"8"});
            var Q590;
            Q590=makeQuery(id+"F15.opPattern","COPY",BODY,{"derivedFrom":makeQuery(id+"F8.opExtrude","SWEPT_BODY",BODY,{"disambiguationData":[OSD([sQuery(id+"F5.wireOp",EDGE,"E6.0.1.0")])]}),"instanceName":"8"});
            var Q591;
            Q591=makeQuery(id+"F15.opPattern","COPY",BODY,{"derivedFrom":makeQuery(id+"F8.opExtrude","SWEPT_BODY",BODY,{"disambiguationData":[OSD([sQuery(id+"F5.wireOp",EDGE,"E5.0.3.0")])]}),"instanceName":"8"});
            var Q592;
            Q592=makeQuery(id+"F15.opPattern","COPY",BODY,{"derivedFrom":makeQuery(id+"F8.opExtrude","SWEPT_BODY",BODY,{"disambiguationData":[OSD([sQuery(id+"F5.wireOp",EDGE,"E5.0.2.0")])]}),"instanceName":"8"});
            var Q593;
            Q593=makeQuery(id+"F15.opPattern","COPY",BODY,{"derivedFrom":makeQuery(id+"F8.opExtrude","SWEPT_BODY",BODY,{"disambiguationData":[OSD([sQuery(id+"F5.wireOp",EDGE,"E5.0.1.0")])]}),"instanceName":"8"});
            var Q594;
            Q594=makeQuery(id+"F15.opPattern","COPY",BODY,{"derivedFrom":makeQuery(id+"F13.opExtrude","SWEPT_BODY",BODY,{"disambiguationData":[OSD([sQuery(id+"F11.wireOp",EDGE,"E11.0.3.0")])]}),"instanceName":"7"});
            var Q595;
            Q595=makeQuery(id+"F15.opPattern","COPY",BODY,{"derivedFrom":makeQuery(id+"F13.opExtrude","SWEPT_BODY",BODY,{"disambiguationData":[OSD([sQuery(id+"F11.wireOp",EDGE,"E11.0.2.0")])]}),"instanceName":"7"});
            var Q596;
            Q596=makeQuery(id+"F15.opPattern","COPY",BODY,{"derivedFrom":makeQuery(id+"F13.opExtrude","SWEPT_BODY",BODY,{"disambiguationData":[OSD([sQuery(id+"F11.wireOp",EDGE,"E11.0.1.0")])]}),"instanceName":"7"});
            var Q597;
            Q597=makeQuery(id+"F15.opPattern","COPY",BODY,{"derivedFrom":makeQuery(id+"F13.opExtrude","SWEPT_BODY",BODY,{"disambiguationData":[OSD([sQuery(id+"F11.wireOp",EDGE,"E10.0.3.0")])]}),"instanceName":"7"});
            var Q598;
            Q598=makeQuery(id+"F15.opPattern","COPY",BODY,{"derivedFrom":makeQuery(id+"F13.opExtrude","SWEPT_BODY",BODY,{"disambiguationData":[OSD([sQuery(id+"F11.wireOp",EDGE,"E10.0.2.0")])]}),"instanceName":"7"});
            var Q599;
            Q599=makeQuery(id+"F15.opPattern","COPY",BODY,{"derivedFrom":makeQuery(id+"F13.opExtrude","SWEPT_BODY",BODY,{"disambiguationData":[OSD([sQuery(id+"F11.wireOp",EDGE,"E10.0.1.0")])]}),"instanceName":"7"});
            var Q600;
            Q600=makeQuery(id+"F15.opPattern","COPY",BODY,{"derivedFrom":makeQuery(id+"F13.opExtrude","SWEPT_BODY",BODY,{"disambiguationData":[OSD([sQuery(id+"F11.wireOp",EDGE,"E9")])]}),"instanceName":"7"});
            var Q601;
            Q601=makeQuery(id+"F15.opPattern","COPY",BODY,{"derivedFrom":makeQuery(id+"F13.opExtrude","SWEPT_BODY",BODY,{"disambiguationData":[OSD([sQuery(id+"F11.wireOp",EDGE,"E8")])]}),"instanceName":"7"});
            var Q602;
            Q602=makeQuery(id+"F15.opPattern","COPY",BODY,{"derivedFrom":makeQuery(id+"F8.opExtrude","SWEPT_BODY",BODY,{"disambiguationData":[OSD([sQuery(id+"F5.wireOp",EDGE,"E6.0.4.0")])]}),"instanceName":"7"});
            var Q603;
            Q603=makeQuery(id+"F15.opPattern","COPY",BODY,{"derivedFrom":makeQuery(id+"F8.opExtrude","SWEPT_BODY",BODY,{"disambiguationData":[OSD([sQuery(id+"F5.wireOp",EDGE,"E6.0.3.0")])]}),"instanceName":"7"});
            var Q604;
            Q604=makeQuery(id+"F15.opPattern","COPY",BODY,{"derivedFrom":makeQuery(id+"F8.opExtrude","SWEPT_BODY",BODY,{"disambiguationData":[OSD([sQuery(id+"F5.wireOp",EDGE,"E6.0.2.0")])]}),"instanceName":"7"});
            var Q605;
            Q605=makeQuery(id+"F15.opPattern","COPY",BODY,{"derivedFrom":makeQuery(id+"F8.opExtrude","SWEPT_BODY",BODY,{"disambiguationData":[OSD([sQuery(id+"F5.wireOp",EDGE,"E6.0.1.0")])]}),"instanceName":"7"});
            var Q606;
            Q606=makeQuery(id+"F15.opPattern","COPY",BODY,{"derivedFrom":makeQuery(id+"F8.opExtrude","SWEPT_BODY",BODY,{"disambiguationData":[OSD([sQuery(id+"F5.wireOp",EDGE,"E5.0.4.0")])]}),"instanceName":"7"});
            var Q607;
            Q607=makeQuery(id+"F15.opPattern","COPY",BODY,{"derivedFrom":makeQuery(id+"F8.opExtrude","SWEPT_BODY",BODY,{"disambiguationData":[OSD([sQuery(id+"F5.wireOp",EDGE,"E5.0.3.0")])]}),"instanceName":"7"});
            var Q608;
            Q608=makeQuery(id+"F15.opPattern","COPY",BODY,{"derivedFrom":makeQuery(id+"F8.opExtrude","SWEPT_BODY",BODY,{"disambiguationData":[OSD([sQuery(id+"F5.wireOp",EDGE,"E5.0.2.0")])]}),"instanceName":"7"});
            var Q609;
            Q609=makeQuery(id+"F15.opPattern","COPY",BODY,{"derivedFrom":makeQuery(id+"F8.opExtrude","SWEPT_BODY",BODY,{"disambiguationData":[OSD([sQuery(id+"F5.wireOp",EDGE,"E5.0.1.0")])]}),"instanceName":"7"});
            var Q610;
            Q610=makeQuery(id+"F15.opPattern","COPY",BODY,{"derivedFrom":makeQuery(id+"F8.opExtrude","SWEPT_BODY",BODY,{"disambiguationData":[OSD([sQuery(id+"F5.wireOp",EDGE,"E4")])]}),"instanceName":"7"});
            var Q611;
            Q611=makeQuery(id+"F15.opPattern","COPY",BODY,{"derivedFrom":makeQuery(id+"F13.opExtrude","SWEPT_BODY",BODY,{"disambiguationData":[OSD([sQuery(id+"F11.wireOp",EDGE,"E11.0.3.0")])]}),"instanceName":"6"});
            var Q612;
            Q612=makeQuery(id+"F15.opPattern","COPY",BODY,{"derivedFrom":makeQuery(id+"F13.opExtrude","SWEPT_BODY",BODY,{"disambiguationData":[OSD([sQuery(id+"F11.wireOp",EDGE,"E11.0.2.0")])]}),"instanceName":"6"});
            var Q613;
            Q613=makeQuery(id+"F15.opPattern","COPY",BODY,{"derivedFrom":makeQuery(id+"F13.opExtrude","SWEPT_BODY",BODY,{"disambiguationData":[OSD([sQuery(id+"F11.wireOp",EDGE,"E11.0.1.0")])]}),"instanceName":"6"});
            var Q614;
            Q614=makeQuery(id+"F15.opPattern","COPY",BODY,{"derivedFrom":makeQuery(id+"F13.opExtrude","SWEPT_BODY",BODY,{"disambiguationData":[OSD([sQuery(id+"F11.wireOp",EDGE,"E10.0.3.0")])]}),"instanceName":"6"});
            var Q615;
            Q615=makeQuery(id+"F15.opPattern","COPY",BODY,{"derivedFrom":makeQuery(id+"F13.opExtrude","SWEPT_BODY",BODY,{"disambiguationData":[OSD([sQuery(id+"F11.wireOp",EDGE,"E8")])]}),"instanceName":"6"});
            var Q616;
            Q616=makeQuery(id+"F15.opPattern","COPY",BODY,{"derivedFrom":makeQuery(id+"F13.opExtrude","SWEPT_BODY",BODY,{"disambiguationData":[OSD([sQuery(id+"F11.wireOp",EDGE,"E9")])]}),"instanceName":"6"});
            var Q617;
            Q617=makeQuery(id+"F15.opPattern","COPY",BODY,{"derivedFrom":makeQuery(id+"F13.opExtrude","SWEPT_BODY",BODY,{"disambiguationData":[OSD([sQuery(id+"F11.wireOp",EDGE,"E10.0.1.0")])]}),"instanceName":"6"});
            var Q618;
            Q618=makeQuery(id+"F15.opPattern","COPY",BODY,{"derivedFrom":makeQuery(id+"F13.opExtrude","SWEPT_BODY",BODY,{"disambiguationData":[OSD([sQuery(id+"F11.wireOp",EDGE,"E10.0.2.0")])]}),"instanceName":"6"});
            var Q619;
            Q619=makeQuery(id+"F15.opPattern","COPY",BODY,{"derivedFrom":makeQuery(id+"F8.opExtrude","SWEPT_BODY",BODY,{"disambiguationData":[OSD([sQuery(id+"F5.wireOp",EDGE,"E6.0.3.0")])]}),"instanceName":"6"});
            var Q620;
            Q620=makeQuery(id+"F15.opPattern","COPY",BODY,{"derivedFrom":makeQuery(id+"F8.opExtrude","SWEPT_BODY",BODY,{"disambiguationData":[OSD([sQuery(id+"F5.wireOp",EDGE,"E6.0.2.0")])]}),"instanceName":"6"});
            var Q621;
            Q621=makeQuery(id+"F15.opPattern","COPY",BODY,{"derivedFrom":makeQuery(id+"F8.opExtrude","SWEPT_BODY",BODY,{"disambiguationData":[OSD([sQuery(id+"F5.wireOp",EDGE,"E6.0.1.0")])]}),"instanceName":"6"});
            var Q622;
            Q622=makeQuery(id+"F15.opPattern","COPY",BODY,{"derivedFrom":makeQuery(id+"F8.opExtrude","SWEPT_BODY",BODY,{"disambiguationData":[OSD([sQuery(id+"F5.wireOp",EDGE,"E5.0.3.0")])]}),"instanceName":"6"});
            var Q623;
            Q623=makeQuery(id+"F15.opPattern","COPY",BODY,{"derivedFrom":makeQuery(id+"F8.opExtrude","SWEPT_BODY",BODY,{"disambiguationData":[OSD([sQuery(id+"F5.wireOp",EDGE,"E5.0.2.0")])]}),"instanceName":"6"});
            var Q624;
            Q624=makeQuery(id+"F15.opPattern","COPY",BODY,{"derivedFrom":makeQuery(id+"F8.opExtrude","SWEPT_BODY",BODY,{"disambiguationData":[OSD([sQuery(id+"F5.wireOp",EDGE,"E5.0.1.0")])]}),"instanceName":"6"});
            var Q625;
            Q625=makeQuery(id+"F15.opPattern","COPY",BODY,{"derivedFrom":makeQuery(id+"F13.opExtrude","SWEPT_BODY",BODY,{"disambiguationData":[OSD([sQuery(id+"F11.wireOp",EDGE,"E11.0.2.0")])]}),"instanceName":"5"});
            var Q626;
            Q626=makeQuery(id+"F15.opPattern","COPY",BODY,{"derivedFrom":makeQuery(id+"F13.opExtrude","SWEPT_BODY",BODY,{"disambiguationData":[OSD([sQuery(id+"F11.wireOp",EDGE,"E11.0.3.0")])]}),"instanceName":"5"});
            var Q627;
            Q627=makeQuery(id+"F15.opPattern","COPY",BODY,{"derivedFrom":makeQuery(id+"F13.opExtrude","SWEPT_BODY",BODY,{"disambiguationData":[OSD([sQuery(id+"F11.wireOp",EDGE,"E10.0.3.0")])]}),"instanceName":"5"});
            var Q628;
            Q628=makeQuery(id+"F15.opPattern","COPY",BODY,{"derivedFrom":makeQuery(id+"F13.opExtrude","SWEPT_BODY",BODY,{"disambiguationData":[OSD([sQuery(id+"F11.wireOp",EDGE,"E10.0.2.0")])]}),"instanceName":"5"});
            var Q629;
            Q629=makeQuery(id+"F15.opPattern","COPY",BODY,{"derivedFrom":makeQuery(id+"F13.opExtrude","SWEPT_BODY",BODY,{"disambiguationData":[OSD([sQuery(id+"F11.wireOp",EDGE,"E10.0.1.0")])]}),"instanceName":"5"});
            var Q630;
            Q630=makeQuery(id+"F15.opPattern","COPY",BODY,{"derivedFrom":makeQuery(id+"F13.opExtrude","SWEPT_BODY",BODY,{"disambiguationData":[OSD([sQuery(id+"F11.wireOp",EDGE,"E9")])]}),"instanceName":"5"});
            var Q631;
            Q631=makeQuery(id+"F15.opPattern","COPY",BODY,{"derivedFrom":makeQuery(id+"F13.opExtrude","SWEPT_BODY",BODY,{"disambiguationData":[OSD([sQuery(id+"F11.wireOp",EDGE,"E8")])]}),"instanceName":"5"});
            var Q632;
            Q632=makeQuery(id+"F15.opPattern","COPY",BODY,{"derivedFrom":makeQuery(id+"F8.opExtrude","SWEPT_BODY",BODY,{"disambiguationData":[OSD([sQuery(id+"F5.wireOp",EDGE,"E6.0.4.0")])]}),"instanceName":"5"});
            var Q633;
            Q633=makeQuery(id+"F15.opPattern","COPY",BODY,{"derivedFrom":makeQuery(id+"F8.opExtrude","SWEPT_BODY",BODY,{"disambiguationData":[OSD([sQuery(id+"F5.wireOp",EDGE,"E6.0.3.0")])]}),"instanceName":"5"});
            var Q634;
            Q634=makeQuery(id+"F15.opPattern","COPY",BODY,{"derivedFrom":makeQuery(id+"F8.opExtrude","SWEPT_BODY",BODY,{"disambiguationData":[OSD([sQuery(id+"F5.wireOp",EDGE,"E6.0.2.0")])]}),"instanceName":"5"});
            var Q635;
            Q635=makeQuery(id+"F15.opPattern","COPY",BODY,{"derivedFrom":makeQuery(id+"F8.opExtrude","SWEPT_BODY",BODY,{"disambiguationData":[OSD([sQuery(id+"F5.wireOp",EDGE,"E6.0.1.0")])]}),"instanceName":"5"});
            var Q636;
            Q636=makeQuery(id+"F15.opPattern","COPY",BODY,{"derivedFrom":makeQuery(id+"F8.opExtrude","SWEPT_BODY",BODY,{"disambiguationData":[OSD([sQuery(id+"F5.wireOp",EDGE,"E5.0.2.0")])]}),"instanceName":"5"});
            var Q637;
            Q637=makeQuery(id+"F15.opPattern","COPY",BODY,{"derivedFrom":makeQuery(id+"F8.opExtrude","SWEPT_BODY",BODY,{"disambiguationData":[OSD([sQuery(id+"F5.wireOp",EDGE,"E5.0.3.0")])]}),"instanceName":"5"});
            var Q638;
            Q638=makeQuery(id+"F15.opPattern","COPY",BODY,{"derivedFrom":makeQuery(id+"F13.opExtrude","SWEPT_BODY",BODY,{"disambiguationData":[OSD([sQuery(id+"F11.wireOp",EDGE,"E11.0.1.0")])]}),"instanceName":"3"});
            var Q639;
            Q639=makeQuery(id+"F15.opPattern","COPY",BODY,{"derivedFrom":makeQuery(id+"F13.opExtrude","SWEPT_BODY",BODY,{"disambiguationData":[OSD([sQuery(id+"F11.wireOp",EDGE,"E11.0.3.0")])]}),"instanceName":"3"});
            var Q640;
            Q640=makeQuery(id+"F3.opExtrude","SWEPT_BODY",BODY,{"disambiguationData":[OSD([sQuery(id+"F2.wireOp",EDGE,"E2.0"),sQuery(id+"F2.wireOp",EDGE,"E3")])]});
            booleanBodies(context, id + "F16", {"operationType" : BooleanOperationType.SUBTRACTION, "tools" : qUnion([Q0, Q1, Q2, Q3, Q4, Q5, Q6, Q7, Q8, Q9, Q10, Q11, Q12, Q13, Q14, Q15, Q16, Q17, Q18, Q19, Q20, Q21, Q22, Q23, Q24, Q25, Q26, Q27, Q28, Q29, Q30, Q31, Q32, Q33, Q34, Q35, Q36, Q37, Q38, Q39, Q40, Q41, Q42, Q43, Q44, Q45, Q46, Q47, Q48, Q49, Q50, Q51, Q52, Q53, Q54, Q55, Q56, Q57, Q58, Q59, Q60, Q61, Q62, Q63, Q64, Q65, Q66, Q67, Q68, Q69, Q70, Q71, Q72, Q73, Q74, Q75, Q76, Q77, Q78, Q79, Q80, Q81, Q82, Q83, Q84, Q85, Q86, Q87, Q88, Q89, Q90, Q91, Q92, Q93, Q94, Q95, Q96, Q97, Q98, Q99, Q100, Q101, Q102, Q103, Q104, Q105, Q106, Q107, Q108, Q109, Q110, Q111, Q112, Q113, Q114, Q115, Q116, Q117, Q118, Q119, Q120, Q121, Q122, Q123, Q124, Q125, Q126, Q127, Q128, Q129, Q130, Q131, Q132, Q133, Q134, Q135, Q136, Q137, Q138, Q139, Q140, Q141, Q142, Q143, Q144, Q145, Q146, Q147, Q148, Q149, Q150, Q151, Q152, Q153, Q154, Q155, Q156, Q157, Q158, Q159, Q160, Q161, Q162, Q163, Q164, Q165, Q166, Q167, Q168, Q169, Q170, Q171, Q172, Q173, Q174, Q175, Q176, Q177, Q178, Q179, Q180, Q181, Q182, Q183, Q184, Q185, Q186, Q187, Q188, Q189, Q190, Q191, Q192, Q193, Q194, Q195, Q196, Q197, Q198, Q199, Q200, Q201, Q202, Q203, Q204, Q205, Q206, Q207, Q208, Q209, Q210, Q211, Q212, Q213, Q214, Q215, Q216, Q217, Q218, Q219, Q220, Q221, Q222, Q223, Q224, Q225, Q226, Q227, Q228, Q229, Q230, Q231, Q232, Q233, Q234, Q235, Q236, Q237, Q238, Q239, Q240, Q241, Q242, Q243, Q244, Q245, Q246, Q247, Q248, Q249, Q250, Q251, Q252, Q253, Q254, Q255, Q256, Q257, Q258, Q259, Q260, Q261, Q262, Q263, Q264, Q265, Q266, Q267, Q268, Q269, Q270, Q271, Q272, Q273, Q274, Q275, Q276, Q277, Q278, Q279, Q280, Q281, Q282, Q283, Q284, Q285, Q286, Q287, Q288, Q289, Q290, Q291, Q292, Q293, Q294, Q295, Q296, Q297, Q298, Q299, Q300, Q301, Q302, Q303, Q304, Q305, Q306, Q307, Q308, Q309, Q310, Q311, Q312, Q313, Q314, Q315, Q316, Q317, Q318, Q319, Q320, Q321, Q322, Q323, Q324, Q325, Q326, Q327, Q328, Q329, Q330, Q331, Q332, Q333, Q334, Q335, Q336, Q337, Q338, Q339, Q340, Q341, Q342, Q343, Q344, Q345, Q346, Q347, Q348, Q349, Q350, Q351, Q352, Q353, Q354, Q355, Q356, Q357, Q358, Q359, Q360, Q361, Q362, Q363, Q364, Q365, Q366, Q367, Q368, Q369, Q370, Q371, Q372, Q373, Q374, Q375, Q376, Q377, Q378, Q379, Q380, Q381, Q382, Q383, Q384, Q385, Q386, Q387, Q388, Q389, Q390, Q391, Q392, Q393, Q394, Q395, Q396, Q397, Q398, Q399, Q400, Q401, Q402, Q403, Q404, Q405, Q406, Q407, Q408, Q409, Q410, Q411, Q412, Q413, Q414, Q415, Q416, Q417, Q418, Q419, Q420, Q421, Q422, Q423, Q424, Q425, Q426, Q427, Q428, Q429, Q430, Q431, Q432, Q433, Q434, Q435, Q436, Q437, Q438, Q439, Q440, Q441, Q442, Q443, Q444, Q445, Q446, Q447, Q448, Q449, Q450, Q451, Q452, Q453, Q454, Q455, Q456, Q457, Q458, Q459, Q460, Q461, Q462, Q463, Q464, Q465, Q466, Q467, Q468, Q469, Q470, Q471, Q472, Q473, Q474, Q475, Q476, Q477, Q478, Q479, Q480, Q481, Q482, Q483, Q484, Q485, Q486, Q487, Q488, Q489, Q490, Q491, Q492, Q493, Q494, Q495, Q496, Q497, Q498, Q499, Q500, Q501, Q502, Q503, Q504, Q505, Q506, Q507, Q508, Q509, Q510, Q511, Q512, Q513, Q514, Q515, Q516, Q517, Q518, Q519, Q520, Q521, Q522, Q523, Q524, Q525, Q526, Q527, Q528, Q529, Q530, Q531, Q532, Q533, Q534, Q535, Q536, Q537, Q538, Q539, Q540, Q541, Q542, Q543, Q544, Q545, Q546, Q547, Q548, Q549, Q550, Q551, Q552, Q553, Q554, Q555, Q556, Q557, Q558, Q559, Q560, Q561, Q562, Q563, Q564, Q565, Q566, Q567, Q568, Q569, Q570, Q571, Q572, Q573, Q574, Q575, Q576, Q577, Q578, Q579, Q580, Q581, Q582, Q583, Q584, Q585, Q586, Q587, Q588, Q589, Q590, Q591, Q592, Q593, Q594, Q595, Q596, Q597, Q598, Q599, Q600, Q601, Q602, Q603, Q604, Q605, Q606, Q607, Q608, Q609, Q610, Q611, Q612, Q613, Q614, Q615, Q616, Q617, Q618, Q619, Q620, Q621, Q622, Q623, Q624, Q625, Q626, Q627, Q628, Q629, Q630, Q631, Q632, Q633, Q634, Q635, Q636, Q637, Q638, Q639]), "targets" : qUnion([Q640]), "keepTools" : true});
        }
    });
